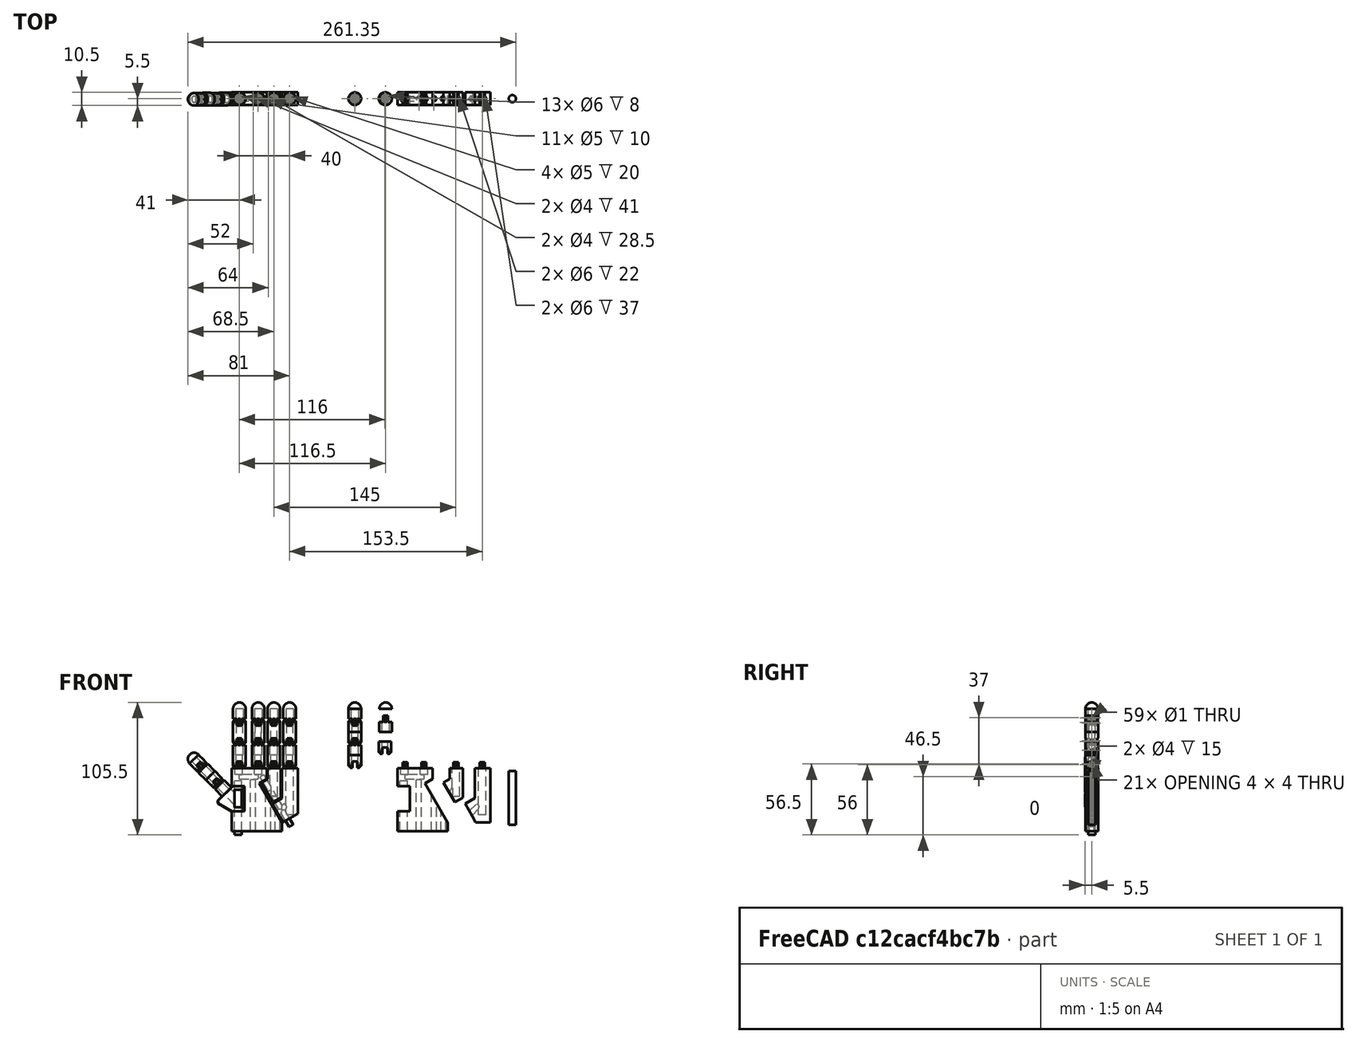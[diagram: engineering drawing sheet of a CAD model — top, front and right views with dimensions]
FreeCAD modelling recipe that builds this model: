
FCSTD DOCUMENT  (FreeCAD 0.19R)
Label: hand
License: All rights reserved
LicenseURL: http://en.wikipedia.org/wiki/All_rights_reserved
objects: Part::Cut×275, Part::Cylinder×259, Part::Box×139, Part::MultiFuse×82, TechDraw::DrawViewDimension×78, Part::Refine×60, Part::Sphere×50, Part::MultiCommon×43, TechDraw::DrawProjGroupItem×11, TechDraw::DrawProjGroup×11, Part::FeaturePython×5, App::DocumentObjectGroup×1, Part::Mirroring×1, TechDraw::DrawSVGTemplate×1, Part::Feature×1, TechDraw::DrawPage×1
note: 915 computed .brp shape members not serialized (recipe doc carries the construction recipe); baked Part::Feature solids carry a one-line shape summary decoded from their .brp

FEATURE [Part::Sphere] Sphere
  Angle1 = 0
  Angle2 = 90
  Angle3 = 360
  AttacherType = Attacher::AttachEngine3D
  Radius = 5
FEATURE [Part::Cylinder] Cylinder
  Angle = 360
  AttacherType = Attacher::AttachEngine3D
  Height = 10
  Placement = pos=(0,0,-10) rot=(0,0,1;0rad)
  Radius = 5
FEATURE [Part::Box] Box  label="Cube"
  AttacherType = Attacher::AttachEngine3D
  Height = 5
  Length = 4
  Placement = pos=(-2,-5,-10) rot=(0,0,1;0rad)
  Width = 10
FEATURE [Part::Cut] Cut
  Base = -> Cylinder
  Tool = -> Box
FEATURE [Part::Cylinder] Cylinder001
  Angle = 360
  AttacherType = Attacher::AttachEngine3D
  Height = 10
  Placement = pos=(0,0,-10) rot=(0,0,1;0rad)
  Radius = 2.5
FEATURE [Part::Cut] Cut001
  Base = -> Cut
  Tool = -> Cylinder001
FEATURE [Part::Cylinder] Cylinder002
  Angle = 360
  AttacherType = Attacher::AttachEngine3D
  Height = 10
  Placement = pos=(5,0,-7) rot=(0,1,0;4.71239rad)
  Radius = 0.5
FEATURE [Part::Cut] Cut002
  Base = -> Cut001
  Tool = -> Cylinder002
FEATURE [Part::Sphere] Sphere001
  Angle1 = -90
  Angle2 = 90
  Angle3 = 360
  AttacherType = Attacher::AttachEngine3D
  Placement = pos=(0,0,-5) rot=(0,0,1;0rad)
  Radius = 6
FEATURE [Part::MultiCommon] Common
  Shapes = -> [Cut002,Sphere001]
FEATURE [Part::Cylinder] Cylinder005
  Angle = 360
  AttacherType = Attacher::AttachEngine3D
  Height = 4
  Placement = pos=(18,0,-4) rot=(0,0,1;0rad)
  Radius = 5
FEATURE [Part::Cylinder] Cylinder006
  Angle = 360
  AttacherType = Attacher::AttachEngine3D
  Height = 10
  Placement = pos=(18,0,-6) rot=(0,0,1;0rad)
  Radius = 3
FEATURE [Part::Cut] Cut004
  Base = -> Cylinder005
  Placement = pos=(-18,0,0) rot=(0,0,1;0rad)
  Tool = -> Cylinder006
FEATURE [Part::MultiFuse] Fusion
  Shapes = -> [Common,Cut004]
FEATURE [Part::Refine] Fusion001
  Placement = pos=(0,0,-18.5) rot=(0,0,1;0rad)
  Source = -> Fusion
FEATURE [Part::Sphere] Sphere002
  Angle1 = -90
  Angle2 = 90
  Angle3 = 360
  AttacherType = Attacher::AttachEngine3D
  Placement = pos=(0,0,-5) rot=(0,0,1;0rad)
  Radius = 6
FEATURE [Part::Cylinder] Cylinder007
  Angle = 360
  AttacherType = Attacher::AttachEngine3D
  Height = 10
  Placement = pos=(0,0,-10) rot=(0,0,1;0rad)
  Radius = 2.5
FEATURE [Part::Box] Box001  label="Cube001"
  AttacherType = Attacher::AttachEngine3D
  Height = 5
  Length = 4
  Placement = pos=(-2,-5,-10) rot=(0,0,1;0rad)
  Width = 10
FEATURE [Part::Cylinder] Cylinder008
  Angle = 360
  AttacherType = Attacher::AttachEngine3D
  Height = 10
  Placement = pos=(0,0,-10) rot=(0,0,1;0rad)
  Radius = 5
FEATURE [Part::Cut] Cut005
  Base = -> Cylinder008
  Tool = -> Box001
FEATURE [Part::Cylinder] Cylinder009
  Angle = 360
  AttacherType = Attacher::AttachEngine3D
  Height = 10
  Placement = pos=(5,0,-7) rot=(0,-1,0;1.5708rad)
  Radius = 0.5
FEATURE [Part::Cylinder] Cylinder010
  Angle = 360
  AttacherType = Attacher::AttachEngine3D
  Height = 4
  Placement = pos=(18,0,-4) rot=(0,0,1;0rad)
  Radius = 5
FEATURE [Part::Cut] Cut008
  Base = -> Cut005
  Tool = -> Cylinder007
FEATURE [Part::Cut] Cut007
  Base = -> Cut008
  Tool = -> Cylinder009
FEATURE [Part::Cylinder] Cylinder011
  Angle = 360
  AttacherType = Attacher::AttachEngine3D
  Height = 10
  Placement = pos=(18,0,-6) rot=(0,0,1;0rad)
  Radius = 3
FEATURE [Part::Cut] Cut006
  Base = -> Cylinder010
  Placement = pos=(-18,0,0) rot=(0,0,1;0rad)
  Tool = -> Cylinder011
FEATURE [Part::MultiCommon] Common001
  Shapes = -> [Cut007,Sphere002]
FEATURE [Part::MultiFuse] Fusion003
  Shapes = -> [Common001,Cut006]
FEATURE [Part::Refine] Fusion002
  Placement = pos=(24,0,-26) rot=(0,0,1;0rad)
  Source = -> Fusion003
FEATURE [Part::Sphere] Sphere003
  Angle1 = 0
  Angle2 = 90
  Angle3 = 360
  AttacherType = Attacher::AttachEngine3D
  Placement = pos=(24.5,0,0) rot=(0,0,1;0rad)
  Radius = 5
FEATURE [Part::Cylinder] Cylinder012
  Angle = 360
  AttacherType = Attacher::AttachEngine3D
  Height = 10
  Placement = pos=(0,-50,-7) rot=(0,0,1;0rad)
  Radius = 5
FEATURE [Part::Sphere] Sphere004
  Angle1 = 0
  Angle2 = 90
  Angle3 = 360
  AttacherType = Attacher::AttachEngine3D
  Placement = pos=(0,-50,0) rot=(0,0,1;0rad)
  Radius = 5
FEATURE [Part::MultiCommon] Common002
  Shapes = -> [Cylinder012,Sphere004]
FEATURE [Part::Cylinder] Cylinder013
  Angle = 360
  AttacherType = Attacher::AttachEngine3D
  Height = 10
  Placement = pos=(0,-50,-10) rot=(0,0,1;0rad)
  Radius = 5
FEATURE [Part::MultiFuse] Fusion004
  Shapes = -> [Common002,Cylinder013]
FEATURE [Part::Box] Box002  label="Cube002"
  AttacherType = Attacher::AttachEngine3D
  Height = 10
  Length = 10
  Placement = pos=(2,-55,-2) rot=(0,0,1;0rad)
  Width = 10
FEATURE [Part::Box] Box003  label="Cube003"
  AttacherType = Attacher::AttachEngine3D
  Height = 10
  Length = 10
  Placement = pos=(-12,-55,-2) rot=(0,0,1;0rad)
  Width = 10
FEATURE [Part::Box] Box004  label="Cube004"
  AttacherType = Attacher::AttachEngine3D
  Height = 10
  Length = 2
  Placement = pos=(-1,-55,-2) rot=(0,0,1;0rad)
  Width = 10
FEATURE [Part::Cut] Cut009
  Base = -> Fusion004
  Tool = -> Box002
FEATURE [Part::Cut] Cut010
  Base = -> Cut009
  Tool = -> Box004
FEATURE [Part::Cut] Cut011
  Base = -> Cut010
  Tool = -> Box003
FEATURE [Part::Cylinder] Cylinder014
  Angle = 360
  AttacherType = Attacher::AttachEngine3D
  Height = 4
  Placement = pos=(-2,-50,1) rot=(0,1,0;1.5708rad)
  Radius = 2
FEATURE [Part::Cylinder] Cylinder015
  Angle = 360
  AttacherType = Attacher::AttachEngine3D
  Height = 10
  Placement = pos=(0,-50,-12) rot=(0,0,1;0rad)
  Radius = 3
FEATURE [Part::Cut] Cut012
  Base = -> Cut011
  Tool = -> Cylinder015
FEATURE [Part::MultiFuse] Fusion005
  Shapes = -> [Cut012,Cylinder014]
FEATURE [Part::Refine] Fusion005001
  Placement = pos=(0,50,-8.5) rot=(0,0,1;0rad)
  Source = -> Fusion005
FEATURE [Part::Cylinder] Cylinder016
  Angle = 360
  AttacherType = Attacher::AttachEngine3D
  Height = 10
  Placement = pos=(-5,0,-7) rot=(0,1,0;1.5708rad)
  Radius = 0.5
FEATURE [Part::Cut] Cut013
  Base = -> Fusion005001
  Placement = pos=(0,0,-18.5) rot=(0,0,1;0rad)
  Tool = -> Cylinder016
FEATURE [Part::Box] Box005  label="Cube005"
  AttacherType = Attacher::AttachEngine3D
  Height = 10
  Length = 2
  Placement = pos=(-1,-55,-2) rot=(0,0,1;0rad)
  Width = 10
FEATURE [Part::Cylinder] Cylinder018
  Angle = 360
  AttacherType = Attacher::AttachEngine3D
  Height = 4
  Placement = pos=(-2,-50,1) rot=(0,1,0;1.5708rad)
  Radius = 2
FEATURE [Part::Cylinder] Cylinder019
  Angle = 360
  AttacherType = Attacher::AttachEngine3D
  Height = 10
  Placement = pos=(0,-50,-7) rot=(0,0,1;0rad)
  Radius = 5
FEATURE [Part::Sphere] Sphere005
  Angle1 = 0
  Angle2 = 90
  Angle3 = 360
  AttacherType = Attacher::AttachEngine3D
  Placement = pos=(0,-50,0) rot=(0,0,1;0rad)
  Radius = 5
FEATURE [Part::MultiCommon] Common003
  Shapes = -> [Cylinder019,Sphere005]
FEATURE [Part::Cylinder] Cylinder020
  Angle = 360
  AttacherType = Attacher::AttachEngine3D
  Height = 10
  Placement = pos=(0,-50,-10) rot=(0,0,1;0rad)
  Radius = 5
FEATURE [Part::MultiFuse] Fusion005003
  Shapes = -> [Common003,Cylinder020]
FEATURE [Part::Box] Box006  label="Cube006"
  AttacherType = Attacher::AttachEngine3D
  Height = 10
  Length = 10
  Placement = pos=(2,-55,-2) rot=(0,0,1;0rad)
  Width = 10
FEATURE [Part::Box] Box007  label="Cube007"
  AttacherType = Attacher::AttachEngine3D
  Height = 10
  Length = 10
  Placement = pos=(-12,-55,-2) rot=(0,0,1;0rad)
  Width = 10
FEATURE [Part::Cut] Cut015
  Base = -> Fusion005003
  Tool = -> Box006
FEATURE [Part::Cylinder] Cylinder021
  Angle = 360
  AttacherType = Attacher::AttachEngine3D
  Height = 10
  Placement = pos=(-5,0,-7) rot=(0,1,0;1.5708rad)
  Radius = 0.5
FEATURE [Part::Cut] Cut017
  Base = -> Cut015
  Tool = -> Box005
FEATURE [Part::Cut] Cut018
  Base = -> Cut017
  Tool = -> Box007
FEATURE [Part::Cylinder] Cylinder022
  Angle = 360
  AttacherType = Attacher::AttachEngine3D
  Height = 10
  Placement = pos=(0,-50,-12) rot=(0,0,1;0rad)
  Radius = 3
FEATURE [Part::Cut] Cut014
  Base = -> Cut018
  Tool = -> Cylinder022
FEATURE [Part::MultiFuse] Fusion005002
  Shapes = -> [Cut014,Cylinder018]
FEATURE [Part::Refine] Fusion005004
  Placement = pos=(0,50,-8.5) rot=(0,0,1;0rad)
  Source = -> Fusion005002
FEATURE [Part::Cut] Cut016
  Base = -> Fusion005004
  Placement = pos=(24.5,0,0) rot=(0,0,1;0rad)
  Tool = -> Cylinder021
FEATURE [Part::Box] Box008  label="Cube008"
  AttacherType = Attacher::AttachEngine3D
  Height = 10
  Length = 2
  Placement = pos=(-1,-55,-2) rot=(0,0,1;0rad)
  Width = 10
FEATURE [Part::Cylinder] Cylinder023
  Angle = 360
  AttacherType = Attacher::AttachEngine3D
  Height = 4
  Placement = pos=(-2,-50,1) rot=(0,1,0;1.5708rad)
  Radius = 2
FEATURE [Part::Cylinder] Cylinder024
  Angle = 360
  AttacherType = Attacher::AttachEngine3D
  Height = 10
  Placement = pos=(0,-50,-7) rot=(0,0,1;0rad)
  Radius = 5
FEATURE [Part::Sphere] Sphere006
  Angle1 = 0
  Angle2 = 90
  Angle3 = 360
  AttacherType = Attacher::AttachEngine3D
  Placement = pos=(0,-50,0) rot=(0,0,1;0rad)
  Radius = 5
FEATURE [Part::MultiCommon] Common004
  Shapes = -> [Cylinder024,Sphere006]
FEATURE [Part::Cylinder] Cylinder025
  Angle = 360
  AttacherType = Attacher::AttachEngine3D
  Height = 10
  Placement = pos=(0,-50,-10) rot=(0,0,1;0rad)
  Radius = 5
FEATURE [Part::MultiFuse] Fusion005006
  Shapes = -> [Common004,Cylinder025]
FEATURE [Part::Box] Box009  label="Cube009"
  AttacherType = Attacher::AttachEngine3D
  Height = 10
  Length = 10
  Placement = pos=(2,-55,-2) rot=(0,0,1;0rad)
  Width = 10
FEATURE [Part::Box] Box010  label="Cube010"
  AttacherType = Attacher::AttachEngine3D
  Height = 10
  Length = 10
  Placement = pos=(-12,-55,-2) rot=(0,0,1;0rad)
  Width = 10
FEATURE [Part::Cut] Cut020
  Base = -> Fusion005006
  Tool = -> Box009
FEATURE [Part::Cylinder] Cylinder026
  Angle = 360
  AttacherType = Attacher::AttachEngine3D
  Height = 10
  Placement = pos=(-5,0,-7) rot=(0,1,0;1.5708rad)
  Radius = 0.5
FEATURE [Part::Cut] Cut022
  Base = -> Cut020
  Tool = -> Box008
FEATURE [Part::Cut] Cut023
  Base = -> Cut022
  Tool = -> Box010
FEATURE [Part::Cylinder] Cylinder027
  Angle = 360
  AttacherType = Attacher::AttachEngine3D
  Height = 10
  Placement = pos=(0,-50,-12) rot=(0,0,1;0rad)
  Radius = 3
FEATURE [Part::Cut] Cut019
  Base = -> Cut023
  Tool = -> Cylinder027
FEATURE [Part::MultiFuse] Fusion005005
  Shapes = -> [Cut019,Cylinder023]
FEATURE [Part::Refine] Fusion005007
  Placement = pos=(0,50,-8.5) rot=(0,0,1;0rad)
  Source = -> Fusion005005
FEATURE [Part::Cut] Cut021
  Base = -> Fusion005007
  Placement = pos=(0,-2.3e-15,-18.5) rot=(1,0,0;3.14159rad)
  Tool = -> Cylinder026
FEATURE [Part::Cylinder] Cylinder028
  Angle = 360
  AttacherType = Attacher::AttachEngine3D
  Height = 10
  Placement = pos=(0,0,-10) rot=(0,0,1;0rad)
  Radius = 5
FEATURE [Part::Box] Box011  label="Cube011"
  AttacherType = Attacher::AttachEngine3D
  Height = 5
  Length = 4
  Placement = pos=(-2,-5,-10) rot=(0,0,1;0rad)
  Width = 10
FEATURE [Part::Cut] Cut024
  Base = -> Cylinder028
  Tool = -> Box011
FEATURE [Part::Cylinder] Cylinder029
  Angle = 360
  AttacherType = Attacher::AttachEngine3D
  Height = 10
  Placement = pos=(0,0,-10) rot=(0,0,1;0rad)
  Radius = 2.5
FEATURE [Part::Cut] Cut025
  Base = -> Cut024
  Tool = -> Cylinder029
FEATURE [Part::Cylinder] Cylinder030
  Angle = 360
  AttacherType = Attacher::AttachEngine3D
  Height = 10
  Placement = pos=(5,0,-7) rot=(0,-1,0;1.5708rad)
  Radius = 0.5
FEATURE [Part::Cut] Cut026
  Base = -> Cut025
  Tool = -> Cylinder030
FEATURE [Part::Sphere] Sphere007
  Angle1 = -90
  Angle2 = 90
  Angle3 = 360
  AttacherType = Attacher::AttachEngine3D
  Placement = pos=(0,0,-5) rot=(0,0,1;0rad)
  Radius = 6
FEATURE [Part::MultiCommon] Common005
  Shapes = -> [Cut026,Sphere007]
FEATURE [Part::Cylinder] Cylinder031
  Angle = 360
  AttacherType = Attacher::AttachEngine3D
  Height = 4
  Placement = pos=(18,0,-4) rot=(0,0,1;0rad)
  Radius = 5
FEATURE [Part::Cylinder] Cylinder032
  Angle = 360
  AttacherType = Attacher::AttachEngine3D
  Height = 10
  Placement = pos=(18,0,-6) rot=(0,0,1;0rad)
  Radius = 3
FEATURE [Part::Cut] Cut027
  Base = -> Cylinder031
  Placement = pos=(-18,0,0) rot=(0,0,1;0rad)
  Tool = -> Cylinder032
FEATURE [Part::MultiFuse] Fusion005008
  Shapes = -> [Common005,Cut027]
FEATURE [Part::Refine] Fusion005009
  Placement = pos=(0,2e-15,-18.5) rot=(1,0,0;3.14159rad)
  Source = -> Fusion005008
FEATURE [Part::Cylinder] Cylinder033
  Angle = 360
  AttacherType = Attacher::AttachEngine3D
  Height = 10
  Placement = pos=(0,0,-10) rot=(0,0,1;0rad)
  Radius = 5
FEATURE [Part::Box] Box012  label="Cube012"
  AttacherType = Attacher::AttachEngine3D
  Height = 5
  Length = 4
  Placement = pos=(-2,-5,-10) rot=(0,0,1;0rad)
  Width = 10
FEATURE [Part::Cut] Cut028
  Base = -> Cylinder033
  Tool = -> Box012
FEATURE [Part::Cylinder] Cylinder034
  Angle = 360
  AttacherType = Attacher::AttachEngine3D
  Height = 10
  Placement = pos=(0,0,-10) rot=(0,0,1;0rad)
  Radius = 2.5
FEATURE [Part::Cut] Cut029
  Base = -> Cut028
  Tool = -> Cylinder034
FEATURE [Part::Cylinder] Cylinder035
  Angle = 360
  AttacherType = Attacher::AttachEngine3D
  Height = 10
  Placement = pos=(5,0,-7) rot=(0,-1,0;1.5708rad)
  Radius = 0.5
FEATURE [Part::Cut] Cut030
  Base = -> Cut029
  Tool = -> Cylinder035
FEATURE [Part::Sphere] Sphere008
  Angle1 = -90
  Angle2 = 90
  Angle3 = 360
  AttacherType = Attacher::AttachEngine3D
  Placement = pos=(0,0,-5) rot=(0,0,1;0rad)
  Radius = 6
FEATURE [Part::MultiCommon] Common006
  Shapes = -> [Cut030,Sphere008]
FEATURE [Part::Cylinder] Cylinder036
  Angle = 360
  AttacherType = Attacher::AttachEngine3D
  Height = 4
  Placement = pos=(18,0,-4) rot=(0,0,1;0rad)
  Radius = 5
FEATURE [Part::Cylinder] Cylinder037
  Angle = 360
  AttacherType = Attacher::AttachEngine3D
  Height = 10
  Placement = pos=(18,0,-6) rot=(0,0,1;0rad)
  Radius = 3
FEATURE [Part::Cut] Cut031
  Base = -> Cylinder036
  Placement = pos=(-18,0,0) rot=(0,0,1;0rad)
  Tool = -> Cylinder037
FEATURE [Part::MultiFuse] Fusion005010
  Shapes = -> [Common006,Cut031]
FEATURE [Part::Refine] Fusion005011
  Placement = pos=(0,0,-37) rot=(0,0,1;0rad)
  Source = -> Fusion005010
FEATURE [App::DocumentObjectGroup] Group  label="dedo"
  Group = -> [Sphere,Cut021,Fusion001,Fusion005009,Cut013,Fusion005011]
FEATURE [Part::Box] Box013  label="Cube013"
  AttacherType = Attacher::AttachEngine3D
  Height = 10
  Length = 2
  Placement = pos=(-1,-55,-2) rot=(0,0,1;0rad)
  Width = 10
FEATURE [Part::Cylinder] Cylinder038
  Angle = 360
  AttacherType = Attacher::AttachEngine3D
  Height = 4
  Placement = pos=(-2,-50,1) rot=(0,1,0;1.5708rad)
  Radius = 2
FEATURE [Part::Sphere] Sphere009
  Angle1 = 0
  Angle2 = 90
  Angle3 = 360
  AttacherType = Attacher::AttachEngine3D
  Radius = 5
FEATURE [Part::Cylinder] Cylinder039
  Angle = 360
  AttacherType = Attacher::AttachEngine3D
  Height = 10
  Placement = pos=(0,0,-10) rot=(0,0,1;0rad)
  Radius = 5
FEATURE [Part::Box] Box014  label="Cube014"
  AttacherType = Attacher::AttachEngine3D
  Height = 5
  Length = 4
  Placement = pos=(-2,-5,-10) rot=(0,0,1;0rad)
  Width = 10
FEATURE [Part::Cut] Cut032
  Base = -> Cylinder039
  Tool = -> Box014
FEATURE [Part::Cylinder] Cylinder040
  Angle = 360
  AttacherType = Attacher::AttachEngine3D
  Height = 10
  Placement = pos=(0,0,-10) rot=(0,0,1;0rad)
  Radius = 2.5
FEATURE [Part::Cut] Cut033
  Base = -> Cut032
  Tool = -> Cylinder040
FEATURE [Part::Cylinder] Cylinder041
  Angle = 360
  AttacherType = Attacher::AttachEngine3D
  Height = 10
  Placement = pos=(5,0,-7) rot=(0,-1,0;1.5708rad)
  Radius = 0.5
FEATURE [Part::Cut] Cut034
  Base = -> Cut033
  Tool = -> Cylinder041
FEATURE [Part::Sphere] Sphere010
  Angle1 = -90
  Angle2 = 90
  Angle3 = 360
  AttacherType = Attacher::AttachEngine3D
  Placement = pos=(0,0,-5) rot=(0,0,1;0rad)
  Radius = 6
FEATURE [Part::MultiCommon] Common007
  Shapes = -> [Cut034,Sphere010]
FEATURE [Part::Cylinder] Cylinder042
  Angle = 360
  AttacherType = Attacher::AttachEngine3D
  Height = 4
  Placement = pos=(18,0,-4) rot=(0,0,1;0rad)
  Radius = 5
FEATURE [Part::Cylinder] Cylinder043
  Angle = 360
  AttacherType = Attacher::AttachEngine3D
  Height = 10
  Placement = pos=(18,0,-6) rot=(0,0,1;0rad)
  Radius = 3
FEATURE [Part::Cut] Cut035
  Base = -> Cylinder042
  Placement = pos=(-18,0,0) rot=(0,0,1;0rad)
  Tool = -> Cylinder043
FEATURE [Part::MultiFuse] Fusion005013
  Shapes = -> [Common007,Cut035]
FEATURE [Part::Refine] Fusion005014
  Placement = pos=(0,0,-18.5) rot=(0,0,1;0rad)
  Source = -> Fusion005013
FEATURE [Part::Cylinder] Cylinder044
  Angle = 360
  AttacherType = Attacher::AttachEngine3D
  Height = 10
  Placement = pos=(0,-50,-7) rot=(0,0,1;0rad)
  Radius = 5
FEATURE [Part::Sphere] Sphere011
  Angle1 = 0
  Angle2 = 90
  Angle3 = 360
  AttacherType = Attacher::AttachEngine3D
  Placement = pos=(0,-50,0) rot=(0,0,1;0rad)
  Radius = 5
FEATURE [Part::MultiCommon] Common008
  Shapes = -> [Cylinder044,Sphere011]
FEATURE [Part::Cylinder] Cylinder045
  Angle = 360
  AttacherType = Attacher::AttachEngine3D
  Height = 10
  Placement = pos=(0,-50,-10) rot=(0,0,1;0rad)
  Radius = 5
FEATURE [Part::MultiFuse] Fusion005015
  Shapes = -> [Common008,Cylinder045]
FEATURE [Part::Box] Box015  label="Cube015"
  AttacherType = Attacher::AttachEngine3D
  Height = 10
  Length = 10
  Placement = pos=(2,-55,-2) rot=(0,0,1;0rad)
  Width = 10
FEATURE [Part::Box] Box016  label="Cube016"
  AttacherType = Attacher::AttachEngine3D
  Height = 10
  Length = 10
  Placement = pos=(-12,-55,-2) rot=(0,0,1;0rad)
  Width = 10
FEATURE [Part::Cut] Cut037
  Base = -> Fusion005015
  Tool = -> Box015
FEATURE [Part::Cylinder] Cylinder046
  Angle = 360
  AttacherType = Attacher::AttachEngine3D
  Height = 10
  Placement = pos=(-5,0,-7) rot=(0,1,0;1.5708rad)
  Radius = 0.5
FEATURE [Part::Cut] Cut039
  Base = -> Cut037
  Tool = -> Box013
FEATURE [Part::Cut] Cut040
  Base = -> Cut039
  Tool = -> Box016
FEATURE [Part::Cylinder] Cylinder047
  Angle = 360
  AttacherType = Attacher::AttachEngine3D
  Height = 10
  Placement = pos=(0,-50,-12) rot=(0,0,1;0rad)
  Radius = 3
FEATURE [Part::Cut] Cut036
  Base = -> Cut040
  Tool = -> Cylinder047
FEATURE [Part::MultiFuse] Fusion005012
  Shapes = -> [Cut036,Cylinder038]
FEATURE [Part::Refine] Fusion005016
  Placement = pos=(0,50,-8.5) rot=(0,0,1;0rad)
  Source = -> Fusion005012
FEATURE [Part::Cut] Cut038
  Base = -> Fusion005016
  Placement = pos=(0,0,-18.5) rot=(0,0,1;0rad)
  Tool = -> Cylinder046
FEATURE [Part::Cylinder] Cylinder048
  Angle = 360
  AttacherType = Attacher::AttachEngine3D
  Height = 10
  Placement = pos=(0,0,-10) rot=(0,0,1;0rad)
  Radius = 2.5
FEATURE [Part::Sphere] Sphere012
  Angle1 = 0
  Angle2 = 90
  Angle3 = 360
  AttacherType = Attacher::AttachEngine3D
  Placement = pos=(0,-50,0) rot=(0,0,1;0rad)
  Radius = 5
FEATURE [Part::Cylinder] Cylinder049
  Angle = 360
  AttacherType = Attacher::AttachEngine3D
  Height = 10
  Placement = pos=(0,0,-10) rot=(0,0,1;0rad)
  Radius = 5
FEATURE [Part::Sphere] Sphere013
  Angle1 = -90
  Angle2 = 90
  Angle3 = 360
  AttacherType = Attacher::AttachEngine3D
  Placement = pos=(0,0,-5) rot=(0,0,1;0rad)
  Radius = 6
FEATURE [Part::Cylinder] Cylinder050
  Angle = 360
  AttacherType = Attacher::AttachEngine3D
  Height = 4
  Placement = pos=(18,0,-4) rot=(0,0,1;0rad)
  Radius = 5
FEATURE [Part::Cylinder] Cylinder051
  Angle = 360
  AttacherType = Attacher::AttachEngine3D
  Height = 10
  Placement = pos=(0,-50,-7) rot=(0,0,1;0rad)
  Radius = 5
FEATURE [Part::Cylinder] Cylinder052
  Angle = 360
  AttacherType = Attacher::AttachEngine3D
  Height = 4
  Placement = pos=(-2,-50,1) rot=(0,1,0;1.5708rad)
  Radius = 2
FEATURE [Part::Box] Box017  label="Cube017"
  AttacherType = Attacher::AttachEngine3D
  Height = 10
  Length = 10
  Placement = pos=(2,-55,-2) rot=(0,0,1;0rad)
  Width = 10
FEATURE [Part::Box] Box018  label="Cube018"
  AttacherType = Attacher::AttachEngine3D
  Height = 10
  Length = 10
  Placement = pos=(-12,-55,-2) rot=(0,0,1;0rad)
  Width = 10
FEATURE [Part::Box] Box019  label="Cube019"
  AttacherType = Attacher::AttachEngine3D
  Height = 10
  Length = 2
  Placement = pos=(-1,-55,-2) rot=(0,0,1;0rad)
  Width = 10
FEATURE [Part::MultiCommon] Common010
  Shapes = -> [Cylinder051,Sphere012]
FEATURE [Part::Cylinder] Cylinder053
  Angle = 360
  AttacherType = Attacher::AttachEngine3D
  Height = 10
  Placement = pos=(0,-50,-10) rot=(0,0,1;0rad)
  Radius = 5
FEATURE [Part::MultiFuse] Fusion005018
  Shapes = -> [Common010,Cylinder053]
FEATURE [Part::Cut] Cut044
  Base = -> Fusion005018
  Tool = -> Box017
FEATURE [Part::Cylinder] Cylinder054
  Angle = 360
  AttacherType = Attacher::AttachEngine3D
  Height = 10
  Placement = pos=(-5,0,-7) rot=(0,1,0;1.5708rad)
  Radius = 0.5
FEATURE [Part::Cut] Cut046
  Base = -> Cut044
  Tool = -> Box019
FEATURE [Part::Cut] Cut047
  Base = -> Cut046
  Tool = -> Box018
FEATURE [Part::Cylinder] Cylinder055
  Angle = 360
  AttacherType = Attacher::AttachEngine3D
  Height = 10
  Placement = pos=(0,-50,-12) rot=(0,0,1;0rad)
  Radius = 3
FEATURE [Part::Cut] Cut043
  Base = -> Cut047
  Tool = -> Cylinder055
FEATURE [Part::MultiFuse] Fusion005017
  Shapes = -> [Cut043,Cylinder052]
FEATURE [Part::Refine] Fusion005019
  Placement = pos=(0,50,-8.5) rot=(0,0,1;0rad)
  Source = -> Fusion005017
FEATURE [Part::Cut] Cut045
  Base = -> Fusion005019
  Placement = pos=(0,-2e-15,-18.5) rot=(1,0,0;3.14159rad)
  Tool = -> Cylinder054
FEATURE [Part::Cylinder] Cylinder056
  Angle = 360
  AttacherType = Attacher::AttachEngine3D
  Height = 10
  Placement = pos=(5,0,-7) rot=(0,-1,0;1.5708rad)
  Radius = 0.5
FEATURE [Part::Cylinder] Cylinder057
  Angle = 360
  AttacherType = Attacher::AttachEngine3D
  Height = 10
  Placement = pos=(5,0,-7) rot=(0,-1,0;1.5708rad)
  Radius = 0.5
FEATURE [Part::Box] Box020  label="Cube020"
  AttacherType = Attacher::AttachEngine3D
  Height = 5
  Length = 4
  Placement = pos=(-2,-5,-10) rot=(0,0,1;0rad)
  Width = 10
FEATURE [Part::Cylinder] Cylinder058
  Angle = 360
  AttacherType = Attacher::AttachEngine3D
  Height = 10
  Placement = pos=(0,0,-10) rot=(0,0,1;0rad)
  Radius = 5
FEATURE [Part::Cut] Cut048
  Base = -> Cylinder058
  Tool = -> Box020
FEATURE [Part::Cut] Cut051
  Base = -> Cut048
  Tool = -> Cylinder048
FEATURE [Part::Cut] Cut042
  Base = -> Cut051
  Tool = -> Cylinder057
FEATURE [Part::MultiCommon] Common009
  Shapes = -> [Cut042,Sphere013]
FEATURE [Part::Cylinder] Cylinder059
  Angle = 360
  AttacherType = Attacher::AttachEngine3D
  Height = 10
  Placement = pos=(18,0,-6) rot=(0,0,1;0rad)
  Radius = 3
FEATURE [Part::Cut] Cut052
  Base = -> Cylinder050
  Placement = pos=(-18,0,0) rot=(0,0,1;0rad)
  Tool = -> Cylinder059
FEATURE [Part::MultiFuse] Fusion005020
  Shapes = -> [Common009,Cut052]
FEATURE [Part::Refine] Fusion005021
  Placement = pos=(0,2e-15,-18.5) rot=(1,0,0;3.14159rad)
  Source = -> Fusion005020
FEATURE [Part::Box] Box021  label="Cube021"
  AttacherType = Attacher::AttachEngine3D
  Height = 5
  Length = 4
  Placement = pos=(-2,-5,-10) rot=(0,0,1;0rad)
  Width = 10
FEATURE [Part::Cut] Cut041
  Base = -> Cylinder049
  Tool = -> Box021
FEATURE [Part::Sphere] Sphere014
  Angle1 = -90
  Angle2 = 90
  Angle3 = 360
  AttacherType = Attacher::AttachEngine3D
  Placement = pos=(0,0,-5) rot=(0,0,1;0rad)
  Radius = 6
FEATURE [Part::Cylinder] Cylinder060
  Angle = 360
  AttacherType = Attacher::AttachEngine3D
  Height = 4
  Placement = pos=(18,0,-4) rot=(0,0,1;0rad)
  Radius = 5
FEATURE [Part::Cylinder] Cylinder061
  Angle = 360
  AttacherType = Attacher::AttachEngine3D
  Height = 10
  Placement = pos=(18,0,-6) rot=(0,0,1;0rad)
  Radius = 3
FEATURE [Part::Cut] Cut053
  Base = -> Cylinder060
  Placement = pos=(-18,0,0) rot=(0,0,1;0rad)
  Tool = -> Cylinder061
FEATURE [Part::Cylinder] Cylinder062
  Angle = 360
  AttacherType = Attacher::AttachEngine3D
  Height = 10
  Placement = pos=(0,0,-10) rot=(0,0,1;0rad)
  Radius = 2.5
FEATURE [Part::Cut] Cut049
  Base = -> Cut041
  Tool = -> Cylinder062
FEATURE [Part::Cut] Cut050
  Base = -> Cut049
  Tool = -> Cylinder056
FEATURE [Part::MultiCommon] Common011
  Shapes = -> [Cut050,Sphere014]
FEATURE [Part::MultiFuse] Fusion005022
  Shapes = -> [Common011,Cut053]
FEATURE [Part::Refine] Fusion005023
  Placement = pos=(0,0,-37) rot=(0,0,1;0rad)
  Source = -> Fusion005022
FEATURE [Part::FeaturePython] Connect  # WARN: FeaturePython — macro-defined, semantics opaque (R4)
  Objects = -> [Sphere009,Fusion005014,Cut038,Cut045,Fusion005021,Fusion005023]
  Placement = pos=(-77,0,0) rot=(0,0,1;0rad)
  Tolerance = 0
FEATURE [Part::Sphere] Sphere015
  Angle1 = -90
  Angle2 = 90
  Angle3 = 360
  AttacherType = Attacher::AttachEngine3D
  Placement = pos=(0,0,-5) rot=(0,0,1;0rad)
  Radius = 6
FEATURE [Part::Cylinder] Cylinder063
  Angle = 360
  AttacherType = Attacher::AttachEngine3D
  Height = 10
  Placement = pos=(-5,0,-7) rot=(0,1,0;1.5708rad)
  Radius = 0.5
FEATURE [Part::Cylinder] Cylinder064
  Angle = 360
  AttacherType = Attacher::AttachEngine3D
  Height = 10
  Placement = pos=(0,0,-10) rot=(0,0,1;0rad)
  Radius = 2.5
FEATURE [Part::Cylinder] Cylinder065
  Angle = 360
  AttacherType = Attacher::AttachEngine3D
  Height = 4
  Placement = pos=(-2,-50,1) rot=(0,1,0;1.5708rad)
  Radius = 2
FEATURE [Part::Cylinder] Cylinder066
  Angle = 360
  AttacherType = Attacher::AttachEngine3D
  Height = 10
  Placement = pos=(5,0,-7) rot=(0,-1,0;1.5708rad)
  Radius = 0.5
FEATURE [Part::Cylinder] Cylinder067
  Angle = 360
  AttacherType = Attacher::AttachEngine3D
  Height = 10
  Placement = pos=(18,0,-6) rot=(0,0,1;0rad)
  Radius = 3
FEATURE [Part::Sphere] Sphere016
  Angle1 = -90
  Angle2 = 90
  Angle3 = 360
  AttacherType = Attacher::AttachEngine3D
  Placement = pos=(0,0,-5) rot=(0,0,1;0rad)
  Radius = 6
FEATURE [Part::Cylinder] Cylinder068
  Angle = 360
  AttacherType = Attacher::AttachEngine3D
  Height = 4
  Placement = pos=(-2,-50,1) rot=(0,1,0;1.5708rad)
  Radius = 2
FEATURE [Part::Box] Box022  label="Cube022"
  AttacherType = Attacher::AttachEngine3D
  Height = 10
  Length = 10
  Placement = pos=(2,-55,-2) rot=(0,0,1;0rad)
  Width = 10
FEATURE [Part::Sphere] Sphere017
  Angle1 = 0
  Angle2 = 90
  Angle3 = 360
  AttacherType = Attacher::AttachEngine3D
  Placement = pos=(0,-50,0) rot=(0,0,1;0rad)
  Radius = 5
FEATURE [Part::Sphere] Sphere018
  Angle1 = 0
  Angle2 = 90
  Angle3 = 360
  AttacherType = Attacher::AttachEngine3D
  Radius = 5
FEATURE [Part::Sphere] Sphere019
  Angle1 = 0
  Angle2 = 90
  Angle3 = 360
  AttacherType = Attacher::AttachEngine3D
  Placement = pos=(0,-50,0) rot=(0,0,1;0rad)
  Radius = 5
FEATURE [Part::Box] Box023  label="Cube023"
  AttacherType = Attacher::AttachEngine3D
  Height = 10
  Length = 2
  Placement = pos=(-1,-55,-2) rot=(0,0,1;0rad)
  Width = 10
FEATURE [Part::Cylinder] Cylinder069
  Angle = 360
  AttacherType = Attacher::AttachEngine3D
  Height = 10
  Placement = pos=(0,-50,-12) rot=(0,0,1;0rad)
  Radius = 3
FEATURE [Part::Cylinder] Cylinder070
  Angle = 360
  AttacherType = Attacher::AttachEngine3D
  Height = 4
  Placement = pos=(18,0,-4) rot=(0,0,1;0rad)
  Radius = 5
FEATURE [Part::Box] Box024  label="Cube024"
  AttacherType = Attacher::AttachEngine3D
  Height = 10
  Length = 10
  Placement = pos=(2,-55,-2) rot=(0,0,1;0rad)
  Width = 10
FEATURE [Part::Cylinder] Cylinder071
  Angle = 360
  AttacherType = Attacher::AttachEngine3D
  Height = 4
  Placement = pos=(18,0,-4) rot=(0,0,1;0rad)
  Radius = 5
FEATURE [Part::Box] Box025  label="Cube025"
  AttacherType = Attacher::AttachEngine3D
  Height = 5
  Length = 4
  Placement = pos=(-2,-5,-10) rot=(0,0,1;0rad)
  Width = 10
FEATURE [Part::Cylinder] Cylinder072
  Angle = 360
  AttacherType = Attacher::AttachEngine3D
  Height = 10
  Placement = pos=(0,-50,-7) rot=(0,0,1;0rad)
  Radius = 5
FEATURE [Part::Cylinder] Cylinder073
  Angle = 360
  AttacherType = Attacher::AttachEngine3D
  Height = 10
  Placement = pos=(0,0,-10) rot=(0,0,1;0rad)
  Radius = 5
FEATURE [Part::Cylinder] Cylinder074
  Angle = 360
  AttacherType = Attacher::AttachEngine3D
  Height = 10
  Placement = pos=(0,0,-10) rot=(0,0,1;0rad)
  Radius = 5
FEATURE [Part::Cut] Cut063
  Base = -> Cylinder074
  Tool = -> Box025
FEATURE [Part::Cut] Cut064
  Base = -> Cylinder071
  Placement = pos=(-18,0,0) rot=(0,0,1;0rad)
  Tool = -> Cylinder067
FEATURE [Part::MultiCommon] Common014
  Shapes = -> [Cylinder072,Sphere017]
FEATURE [Part::Box] Box026  label="Cube026"
  AttacherType = Attacher::AttachEngine3D
  Height = 10
  Length = 10
  Placement = pos=(-12,-55,-2) rot=(0,0,1;0rad)
  Width = 10
FEATURE [Part::Cylinder] Cylinder075
  Angle = 360
  AttacherType = Attacher::AttachEngine3D
  Height = 10
  Placement = pos=(0,0,-10) rot=(0,0,1;0rad)
  Radius = 2.5
FEATURE [Part::Cut] Cut062
  Base = -> Cut063
  Tool = -> Cylinder075
FEATURE [Part::Cut] Cut056
  Base = -> Cut062
  Tool = -> Cylinder066
FEATURE [Part::MultiCommon] Common012
  Shapes = -> [Cut056,Sphere016]
FEATURE [Part::MultiFuse] Fusion005030
  Shapes = -> [Common012,Cut064]
FEATURE [Part::Refine] Fusion005028
  Placement = pos=(0,0,-18.5) rot=(0,0,1;0rad)
  Source = -> Fusion005030
FEATURE [Part::Cylinder] Cylinder076
  Angle = 360
  AttacherType = Attacher::AttachEngine3D
  Height = 10
  Placement = pos=(0,-50,-10) rot=(0,0,1;0rad)
  Radius = 5
FEATURE [Part::MultiFuse] Fusion005024
  Shapes = -> [Common014,Cylinder076]
FEATURE [Part::Cut] Cut061
  Base = -> Fusion005024
  Tool = -> Box024
FEATURE [Part::Cut] Cut059
  Base = -> Cut061
  Tool = -> Box023
FEATURE [Part::Cut] Cut058
  Base = -> Cut059
  Tool = -> Box026
FEATURE [Part::Cut] Cut055
  Base = -> Cut058
  Tool = -> Cylinder069
FEATURE [Part::MultiFuse] Fusion005027
  Shapes = -> [Cut055,Cylinder065]
FEATURE [Part::Refine] Fusion005029
  Placement = pos=(0,50,-8.5) rot=(0,0,1;0rad)
  Source = -> Fusion005027
FEATURE [Part::Cut] Cut060
  Base = -> Fusion005029
  Placement = pos=(0,0,-18.5) rot=(0,0,1;0rad)
  Tool = -> Cylinder063
FEATURE [Part::Cylinder] Cylinder077
  Angle = 360
  AttacherType = Attacher::AttachEngine3D
  Height = 10
  Placement = pos=(0,-50,-7) rot=(0,0,1;0rad)
  Radius = 5
FEATURE [Part::Box] Box027  label="Cube027"
  AttacherType = Attacher::AttachEngine3D
  Height = 10
  Length = 10
  Placement = pos=(-12,-55,-2) rot=(0,0,1;0rad)
  Width = 10
FEATURE [Part::Box] Box028  label="Cube028"
  AttacherType = Attacher::AttachEngine3D
  Height = 10
  Length = 2
  Placement = pos=(-1,-55,-2) rot=(0,0,1;0rad)
  Width = 10
FEATURE [Part::MultiCommon] Common015
  Shapes = -> [Cylinder077,Sphere019]
FEATURE [Part::Cylinder] Cylinder078
  Angle = 360
  AttacherType = Attacher::AttachEngine3D
  Height = 10
  Placement = pos=(0,-50,-10) rot=(0,0,1;0rad)
  Radius = 5
FEATURE [Part::MultiFuse] Fusion005026
  Shapes = -> [Common015,Cylinder078]
FEATURE [Part::Cut] Cut066
  Base = -> Fusion005026
  Tool = -> Box022
FEATURE [Part::Cylinder] Cylinder079
  Angle = 360
  AttacherType = Attacher::AttachEngine3D
  Height = 10
  Placement = pos=(-5,0,-7) rot=(0,1,0;1.5708rad)
  Radius = 0.5
FEATURE [Part::Cut] Cut068
  Base = -> Cut066
  Tool = -> Box028
FEATURE [Part::Cut] Cut069
  Base = -> Cut068
  Tool = -> Box027
FEATURE [Part::Cylinder] Cylinder080
  Angle = 360
  AttacherType = Attacher::AttachEngine3D
  Height = 10
  Placement = pos=(0,-50,-12) rot=(0,0,1;0rad)
  Radius = 3
FEATURE [Part::Cut] Cut065
  Base = -> Cut069
  Tool = -> Cylinder080
FEATURE [Part::MultiFuse] Fusion005025
  Shapes = -> [Cut065,Cylinder068]
FEATURE [Part::Refine] Fusion005031
  Placement = pos=(0,50,-8.5) rot=(0,0,1;0rad)
  Source = -> Fusion005025
FEATURE [Part::Cut] Cut067
  Base = -> Fusion005031
  Placement = pos=(0,-2e-15,-18.5) rot=(1,0,0;3.14159rad)
  Tool = -> Cylinder079
FEATURE [Part::Cylinder] Cylinder081
  Angle = 360
  AttacherType = Attacher::AttachEngine3D
  Height = 10
  Placement = pos=(5,0,-7) rot=(0,-1,0;1.5708rad)
  Radius = 0.5
FEATURE [Part::Cylinder] Cylinder082
  Angle = 360
  AttacherType = Attacher::AttachEngine3D
  Height = 10
  Placement = pos=(5,0,-7) rot=(0,-1,0;1.5708rad)
  Radius = 0.5
FEATURE [Part::Box] Box029  label="Cube029"
  AttacherType = Attacher::AttachEngine3D
  Height = 5
  Length = 4
  Placement = pos=(-2,-5,-10) rot=(0,0,1;0rad)
  Width = 10
FEATURE [Part::Cylinder] Cylinder083
  Angle = 360
  AttacherType = Attacher::AttachEngine3D
  Height = 10
  Placement = pos=(0,0,-10) rot=(0,0,1;0rad)
  Radius = 5
FEATURE [Part::Cut] Cut070
  Base = -> Cylinder083
  Tool = -> Box029
FEATURE [Part::Cut] Cut073
  Base = -> Cut070
  Tool = -> Cylinder064
FEATURE [Part::Cut] Cut054
  Base = -> Cut073
  Tool = -> Cylinder082
FEATURE [Part::MultiCommon] Common013
  Shapes = -> [Cut054,Sphere015]
FEATURE [Part::Cylinder] Cylinder084
  Angle = 360
  AttacherType = Attacher::AttachEngine3D
  Height = 10
  Placement = pos=(18,0,-6) rot=(0,0,1;0rad)
  Radius = 3
FEATURE [Part::Cut] Cut074
  Base = -> Cylinder070
  Placement = pos=(-18,0,0) rot=(0,0,1;0rad)
  Tool = -> Cylinder084
FEATURE [Part::MultiFuse] Fusion005032
  Shapes = -> [Common013,Cut074]
FEATURE [Part::Refine] Fusion005033
  Placement = pos=(0,2e-15,-18.5) rot=(1,0,0;3.14159rad)
  Source = -> Fusion005032
FEATURE [Part::Box] Box030  label="Cube030"
  AttacherType = Attacher::AttachEngine3D
  Height = 5
  Length = 4
  Placement = pos=(-2,-5,-10) rot=(0,0,1;0rad)
  Width = 10
FEATURE [Part::Cut] Cut057
  Base = -> Cylinder073
  Tool = -> Box030
FEATURE [Part::Sphere] Sphere020
  Angle1 = -90
  Angle2 = 90
  Angle3 = 360
  AttacherType = Attacher::AttachEngine3D
  Placement = pos=(0,0,-5) rot=(0,0,1;0rad)
  Radius = 6
FEATURE [Part::Cylinder] Cylinder085
  Angle = 360
  AttacherType = Attacher::AttachEngine3D
  Height = 4
  Placement = pos=(18,0,-4) rot=(0,0,1;0rad)
  Radius = 5
FEATURE [Part::Cylinder] Cylinder086
  Angle = 360
  AttacherType = Attacher::AttachEngine3D
  Height = 10
  Placement = pos=(18,0,-6) rot=(0,0,1;0rad)
  Radius = 3
FEATURE [Part::Cut] Cut075
  Base = -> Cylinder085
  Placement = pos=(-18,0,0) rot=(0,0,1;0rad)
  Tool = -> Cylinder086
FEATURE [Part::Cylinder] Cylinder087
  Angle = 360
  AttacherType = Attacher::AttachEngine3D
  Height = 10
  Placement = pos=(0,0,-10) rot=(0,0,1;0rad)
  Radius = 2.5
FEATURE [Part::Cut] Cut071
  Base = -> Cut057
  Tool = -> Cylinder087
FEATURE [Part::Cut] Cut072
  Base = -> Cut071
  Tool = -> Cylinder081
FEATURE [Part::MultiCommon] Common016
  Shapes = -> [Cut072,Sphere020]
FEATURE [Part::MultiFuse] Fusion005034
  Shapes = -> [Common016,Cut075]
FEATURE [Part::Refine] Fusion005035
  Placement = pos=(0,0,-37) rot=(0,0,1;0rad)
  Source = -> Fusion005034
FEATURE [Part::FeaturePython] Connect001  # WARN: FeaturePython — macro-defined, semantics opaque (R4)
  Objects = -> [Sphere018,Fusion005028,Cut060,Cut067,Fusion005033,Fusion005035]
  Placement = pos=(-92,0,0) rot=(0,0,1;0rad)
  Tolerance = 0
FEATURE [Part::Sphere] Sphere021
  Angle1 = 0
  Angle2 = 90
  Angle3 = 360
  AttacherType = Attacher::AttachEngine3D
  Placement = pos=(0,-50,0) rot=(0,0,1;0rad)
  Radius = 5
FEATURE [Part::Box] Box031  label="Cube031"
  AttacherType = Attacher::AttachEngine3D
  Height = 10
  Length = 2
  Placement = pos=(-1,-55,-2) rot=(0,0,1;0rad)
  Width = 10
FEATURE [Part::Cylinder] Cylinder088
  Angle = 360
  AttacherType = Attacher::AttachEngine3D
  Height = 10
  Placement = pos=(0,-50,-12) rot=(0,0,1;0rad)
  Radius = 3
FEATURE [Part::Cylinder] Cylinder089
  Angle = 360
  AttacherType = Attacher::AttachEngine3D
  Height = 4
  Placement = pos=(18,0,-4) rot=(0,0,1;0rad)
  Radius = 5
FEATURE [Part::Box] Box032  label="Cube032"
  AttacherType = Attacher::AttachEngine3D
  Height = 10
  Length = 10
  Placement = pos=(2,-55,-2) rot=(0,0,1;0rad)
  Width = 10
FEATURE [Part::Cylinder] Cylinder090
  Angle = 360
  AttacherType = Attacher::AttachEngine3D
  Height = 4
  Placement = pos=(18,0,-4) rot=(0,0,1;0rad)
  Radius = 5
FEATURE [Part::Box] Box033  label="Cube033"
  AttacherType = Attacher::AttachEngine3D
  Height = 5
  Length = 4
  Placement = pos=(-2,-5,-10) rot=(0,0,1;0rad)
  Width = 10
FEATURE [Part::Cylinder] Cylinder091
  Angle = 360
  AttacherType = Attacher::AttachEngine3D
  Height = 10
  Placement = pos=(0,-50,-7) rot=(0,0,1;0rad)
  Radius = 5
FEATURE [Part::Cylinder] Cylinder092
  Angle = 360
  AttacherType = Attacher::AttachEngine3D
  Height = 10
  Placement = pos=(0,0,-10) rot=(0,0,1;0rad)
  Radius = 5
FEATURE [Part::Cylinder] Cylinder093
  Angle = 360
  AttacherType = Attacher::AttachEngine3D
  Height = 10
  Placement = pos=(0,0,-10) rot=(0,0,1;0rad)
  Radius = 5
FEATURE [Part::Cut] Cut083
  Base = -> Cylinder093
  Tool = -> Box033
FEATURE [Part::Box] Box034  label="Cube034"
  AttacherType = Attacher::AttachEngine3D
  Height = 10
  Length = 10
  Placement = pos=(-12,-55,-2) rot=(0,0,1;0rad)
  Width = 10
FEATURE [Part::Cylinder] Cylinder094
  Angle = 360
  AttacherType = Attacher::AttachEngine3D
  Height = 10
  Placement = pos=(0,0,-10) rot=(0,0,1;0rad)
  Radius = 2.5
FEATURE [Part::Cut] Cut082
  Base = -> Cut083
  Tool = -> Cylinder094
FEATURE [Part::Cylinder] Cylinder095
  Angle = 360
  AttacherType = Attacher::AttachEngine3D
  Height = 10
  Placement = pos=(18,0,-6) rot=(0,0,1;0rad)
  Radius = 3
FEATURE [Part::Cut] Cut084
  Base = -> Cylinder090
  Placement = pos=(-18,0,0) rot=(0,0,1;0rad)
  Tool = -> Cylinder095
FEATURE [Part::Sphere] Sphere022
  Angle1 = -90
  Angle2 = 90
  Angle3 = 360
  AttacherType = Attacher::AttachEngine3D
  Placement = pos=(0,0,-5) rot=(0,0,1;0rad)
  Radius = 6
FEATURE [Part::Box] Box035  label="Cube035"
  AttacherType = Attacher::AttachEngine3D
  Height = 10
  Length = 10
  Placement = pos=(2,-55,-2) rot=(0,0,1;0rad)
  Width = 10
FEATURE [Part::Cylinder] Cylinder096
  Angle = 360
  AttacherType = Attacher::AttachEngine3D
  Height = 10
  Placement = pos=(5,0,-7) rot=(0,-1,0;1.5708rad)
  Radius = 0.5
FEATURE [Part::Cut] Cut076
  Base = -> Cut082
  Tool = -> Cylinder096
FEATURE [Part::Cylinder] Cylinder097
  Angle = 360
  AttacherType = Attacher::AttachEngine3D
  Height = 10
  Placement = pos=(-5,0,-7) rot=(0,1,0;1.5708rad)
  Radius = 0.5
FEATURE [Part::Cylinder] Cylinder098
  Angle = 360
  AttacherType = Attacher::AttachEngine3D
  Height = 4
  Placement = pos=(-2,-50,1) rot=(0,1,0;1.5708rad)
  Radius = 2
FEATURE [Part::Sphere] Sphere023
  Angle1 = -90
  Angle2 = 90
  Angle3 = 360
  AttacherType = Attacher::AttachEngine3D
  Placement = pos=(0,0,-5) rot=(0,0,1;0rad)
  Radius = 6
FEATURE [Part::Sphere] Sphere024
  Angle1 = 0
  Angle2 = 90
  Angle3 = 360
  AttacherType = Attacher::AttachEngine3D
  Placement = pos=(0,-50,0) rot=(0,0,1;0rad)
  Radius = 5
FEATURE [Part::MultiCommon] Common017
  Shapes = -> [Cylinder091,Sphere024]
FEATURE [Part::Sphere] Sphere025
  Angle1 = 0
  Angle2 = 90
  Angle3 = 360
  AttacherType = Attacher::AttachEngine3D
  Radius = 5
FEATURE [Part::Cylinder] Cylinder099
  Angle = 360
  AttacherType = Attacher::AttachEngine3D
  Height = 4
  Placement = pos=(-2,-50,1) rot=(0,1,0;1.5708rad)
  Radius = 2
FEATURE [Part::MultiCommon] Common019
  Shapes = -> [Cut076,Sphere023]
FEATURE [Part::MultiFuse] Fusion005040
  Shapes = -> [Common019,Cut084]
FEATURE [Part::Refine] Fusion005038
  Placement = pos=(0,0,-18.5) rot=(0,0,1;0rad)
  Source = -> Fusion005040
FEATURE [Part::Cylinder] Cylinder100
  Angle = 360
  AttacherType = Attacher::AttachEngine3D
  Height = 10
  Placement = pos=(0,0,-10) rot=(0,0,1;0rad)
  Radius = 2.5
FEATURE [Part::Cylinder] Cylinder101
  Angle = 360
  AttacherType = Attacher::AttachEngine3D
  Height = 10
  Placement = pos=(0,-50,-10) rot=(0,0,1;0rad)
  Radius = 5
FEATURE [Part::MultiFuse] Fusion005041
  Shapes = -> [Common017,Cylinder101]
FEATURE [Part::Cut] Cut081
  Base = -> Fusion005041
  Tool = -> Box032
FEATURE [Part::Cut] Cut079
  Base = -> Cut081
  Tool = -> Box031
FEATURE [Part::Cut] Cut078
  Base = -> Cut079
  Tool = -> Box034
FEATURE [Part::Cut] Cut086
  Base = -> Cut078
  Tool = -> Cylinder088
FEATURE [Part::MultiFuse] Fusion005037
  Shapes = -> [Cut086,Cylinder099]
FEATURE [Part::Refine] Fusion005039
  Placement = pos=(0,50,-8.5) rot=(0,0,1;0rad)
  Source = -> Fusion005037
FEATURE [Part::Cut] Cut080
  Base = -> Fusion005039
  Placement = pos=(0,0,-18.5) rot=(0,0,1;0rad)
  Tool = -> Cylinder097
FEATURE [Part::Cylinder] Cylinder102
  Angle = 360
  AttacherType = Attacher::AttachEngine3D
  Height = 10
  Placement = pos=(0,-50,-7) rot=(0,0,1;0rad)
  Radius = 5
FEATURE [Part::Box] Box036  label="Cube036"
  AttacherType = Attacher::AttachEngine3D
  Height = 10
  Length = 10
  Placement = pos=(-12,-55,-2) rot=(0,0,1;0rad)
  Width = 10
FEATURE [Part::Box] Box037  label="Cube037"
  AttacherType = Attacher::AttachEngine3D
  Height = 10
  Length = 2
  Placement = pos=(-1,-55,-2) rot=(0,0,1;0rad)
  Width = 10
FEATURE [Part::MultiCommon] Common020
  Shapes = -> [Cylinder102,Sphere021]
FEATURE [Part::Cylinder] Cylinder103
  Angle = 360
  AttacherType = Attacher::AttachEngine3D
  Height = 10
  Placement = pos=(0,-50,-10) rot=(0,0,1;0rad)
  Radius = 5
FEATURE [Part::MultiFuse] Fusion005042
  Shapes = -> [Common020,Cylinder103]
FEATURE [Part::Cut] Cut088
  Base = -> Fusion005042
  Tool = -> Box035
FEATURE [Part::Cylinder] Cylinder104
  Angle = 360
  AttacherType = Attacher::AttachEngine3D
  Height = 10
  Placement = pos=(-5,0,-7) rot=(0,1,0;1.5708rad)
  Radius = 0.5
FEATURE [Part::Cut] Cut090
  Base = -> Cut088
  Tool = -> Box037
FEATURE [Part::Cut] Cut091
  Base = -> Cut090
  Tool = -> Box036
FEATURE [Part::Cylinder] Cylinder105
  Angle = 360
  AttacherType = Attacher::AttachEngine3D
  Height = 10
  Placement = pos=(0,-50,-12) rot=(0,0,1;0rad)
  Radius = 3
FEATURE [Part::Cut] Cut087
  Base = -> Cut091
  Tool = -> Cylinder105
FEATURE [Part::MultiFuse] Fusion005043
  Shapes = -> [Cut087,Cylinder098]
FEATURE [Part::Refine] Fusion005036
  Placement = pos=(0,50,-8.5) rot=(0,0,1;0rad)
  Source = -> Fusion005043
FEATURE [Part::Cut] Cut089
  Base = -> Fusion005036
  Placement = pos=(0,-2e-15,-18.5) rot=(1,0,0;3.14159rad)
  Tool = -> Cylinder104
FEATURE [Part::Cylinder] Cylinder106
  Angle = 360
  AttacherType = Attacher::AttachEngine3D
  Height = 10
  Placement = pos=(5,0,-7) rot=(0,-1,0;1.5708rad)
  Radius = 0.5
FEATURE [Part::Cylinder] Cylinder107
  Angle = 360
  AttacherType = Attacher::AttachEngine3D
  Height = 10
  Placement = pos=(5,0,-7) rot=(0,-1,0;1.5708rad)
  Radius = 0.5
FEATURE [Part::Box] Box038  label="Cube038"
  AttacherType = Attacher::AttachEngine3D
  Height = 5
  Length = 4
  Placement = pos=(-2,-5,-10) rot=(0,0,1;0rad)
  Width = 10
FEATURE [Part::Cylinder] Cylinder108
  Angle = 360
  AttacherType = Attacher::AttachEngine3D
  Height = 10
  Placement = pos=(0,0,-10) rot=(0,0,1;0rad)
  Radius = 5
FEATURE [Part::Cut] Cut092
  Base = -> Cylinder108
  Tool = -> Box038
FEATURE [Part::Cut] Cut095
  Base = -> Cut092
  Tool = -> Cylinder100
FEATURE [Part::Cut] Cut085
  Base = -> Cut095
  Tool = -> Cylinder107
FEATURE [Part::MultiCommon] Common018
  Shapes = -> [Cut085,Sphere022]
FEATURE [Part::Cylinder] Cylinder109
  Angle = 360
  AttacherType = Attacher::AttachEngine3D
  Height = 10
  Placement = pos=(18,0,-6) rot=(0,0,1;0rad)
  Radius = 3
FEATURE [Part::Cut] Cut096
  Base = -> Cylinder089
  Placement = pos=(-18,0,0) rot=(0,0,1;0rad)
  Tool = -> Cylinder109
FEATURE [Part::MultiFuse] Fusion005044
  Shapes = -> [Common018,Cut096]
FEATURE [Part::Refine] Fusion005045
  Placement = pos=(0,2e-15,-18.5) rot=(1,0,0;3.14159rad)
  Source = -> Fusion005044
FEATURE [Part::Box] Box039  label="Cube039"
  AttacherType = Attacher::AttachEngine3D
  Height = 5
  Length = 4
  Placement = pos=(-2,-5,-10) rot=(0,0,1;0rad)
  Width = 10
FEATURE [Part::Cut] Cut077
  Base = -> Cylinder092
  Tool = -> Box039
FEATURE [Part::Sphere] Sphere026
  Angle1 = -90
  Angle2 = 90
  Angle3 = 360
  AttacherType = Attacher::AttachEngine3D
  Placement = pos=(0,0,-5) rot=(0,0,1;0rad)
  Radius = 6
FEATURE [Part::Cylinder] Cylinder110
  Angle = 360
  AttacherType = Attacher::AttachEngine3D
  Height = 4
  Placement = pos=(18,0,-4) rot=(0,0,1;0rad)
  Radius = 5
FEATURE [Part::Cylinder] Cylinder111
  Angle = 360
  AttacherType = Attacher::AttachEngine3D
  Height = 10
  Placement = pos=(18,0,-6) rot=(0,0,1;0rad)
  Radius = 3
FEATURE [Part::Cut] Cut097
  Base = -> Cylinder110
  Placement = pos=(-18,0,0) rot=(0,0,1;0rad)
  Tool = -> Cylinder111
FEATURE [Part::Cylinder] Cylinder112
  Angle = 360
  AttacherType = Attacher::AttachEngine3D
  Height = 10
  Placement = pos=(0,0,-10) rot=(0,0,1;0rad)
  Radius = 2.5
FEATURE [Part::Cut] Cut093
  Base = -> Cut077
  Tool = -> Cylinder112
FEATURE [Part::Cut] Cut094
  Base = -> Cut093
  Tool = -> Cylinder106
FEATURE [Part::MultiCommon] Common021
  Shapes = -> [Cut094,Sphere026]
FEATURE [Part::MultiFuse] Fusion005046
  Shapes = -> [Common021,Cut097]
FEATURE [Part::Refine] Fusion005047
  Placement = pos=(0,0,-37) rot=(0,0,1;0rad)
  Source = -> Fusion005046
FEATURE [Part::FeaturePython] Connect002  # WARN: FeaturePython — macro-defined, semantics opaque (R4)
  Objects = -> [Sphere025,Fusion005038,Cut080,Cut089,Fusion005045,Fusion005047]
  Placement = pos=(-52,0,0) rot=(0,0,1;0rad)
  Tolerance = 0
FEATURE [Part::Sphere] Sphere027
  Angle1 = 0
  Angle2 = 90
  Angle3 = 360
  AttacherType = Attacher::AttachEngine3D
  Placement = pos=(0,-50,0) rot=(0,0,1;0rad)
  Radius = 5
FEATURE [Part::Box] Box040  label="Cube040"
  AttacherType = Attacher::AttachEngine3D
  Height = 10
  Length = 2
  Placement = pos=(-1,-55,-2) rot=(0,0,1;0rad)
  Width = 10
FEATURE [Part::Cylinder] Cylinder113
  Angle = 360
  AttacherType = Attacher::AttachEngine3D
  Height = 10
  Placement = pos=(0,-50,-12) rot=(0,0,1;0rad)
  Radius = 3
FEATURE [Part::Cylinder] Cylinder114
  Angle = 360
  AttacherType = Attacher::AttachEngine3D
  Height = 4
  Placement = pos=(18,0,-4) rot=(0,0,1;0rad)
  Radius = 5
FEATURE [Part::Box] Box041  label="Cube041"
  AttacherType = Attacher::AttachEngine3D
  Height = 10
  Length = 10
  Placement = pos=(2,-55,-2) rot=(0,0,1;0rad)
  Width = 10
FEATURE [Part::Cylinder] Cylinder115
  Angle = 360
  AttacherType = Attacher::AttachEngine3D
  Height = 4
  Placement = pos=(18,0,-4) rot=(0,0,1;0rad)
  Radius = 5
FEATURE [Part::Box] Box042  label="Cube042"
  AttacherType = Attacher::AttachEngine3D
  Height = 5
  Length = 4
  Placement = pos=(-2,-5,-10) rot=(0,0,1;0rad)
  Width = 10
FEATURE [Part::Cylinder] Cylinder116
  Angle = 360
  AttacherType = Attacher::AttachEngine3D
  Height = 10
  Placement = pos=(0,-50,-7) rot=(0,0,1;0rad)
  Radius = 5
FEATURE [Part::Cylinder] Cylinder117
  Angle = 360
  AttacherType = Attacher::AttachEngine3D
  Height = 10
  Placement = pos=(0,0,-10) rot=(0,0,1;0rad)
  Radius = 5
FEATURE [Part::Cylinder] Cylinder118
  Angle = 360
  AttacherType = Attacher::AttachEngine3D
  Height = 10
  Placement = pos=(0,0,-10) rot=(0,0,1;0rad)
  Radius = 5
FEATURE [Part::Cut] Cut105
  Base = -> Cylinder118
  Tool = -> Box042
FEATURE [Part::Box] Box043  label="Cube043"
  AttacherType = Attacher::AttachEngine3D
  Height = 10
  Length = 10
  Placement = pos=(-12,-55,-2) rot=(0,0,1;0rad)
  Width = 10
FEATURE [Part::Cylinder] Cylinder119
  Angle = 360
  AttacherType = Attacher::AttachEngine3D
  Height = 10
  Placement = pos=(0,0,-10) rot=(0,0,1;0rad)
  Radius = 2.5
FEATURE [Part::Cut] Cut104
  Base = -> Cut105
  Tool = -> Cylinder119
FEATURE [Part::Cylinder] Cylinder120
  Angle = 360
  AttacherType = Attacher::AttachEngine3D
  Height = 10
  Placement = pos=(18,0,-6) rot=(0,0,1;0rad)
  Radius = 3
FEATURE [Part::Cut] Cut106
  Base = -> Cylinder115
  Placement = pos=(-18,0,0) rot=(0,0,1;0rad)
  Tool = -> Cylinder120
FEATURE [Part::Sphere] Sphere028
  Angle1 = -90
  Angle2 = 90
  Angle3 = 360
  AttacherType = Attacher::AttachEngine3D
  Placement = pos=(0,0,-5) rot=(0,0,1;0rad)
  Radius = 6
FEATURE [Part::Box] Box044  label="Cube044"
  AttacherType = Attacher::AttachEngine3D
  Height = 10
  Length = 10
  Placement = pos=(2,-55,-2) rot=(0,0,1;0rad)
  Width = 10
FEATURE [Part::Cylinder] Cylinder121
  Angle = 360
  AttacherType = Attacher::AttachEngine3D
  Height = 10
  Placement = pos=(5,0,-7) rot=(0,-1,0;1.5708rad)
  Radius = 0.5
FEATURE [Part::Cut] Cut098
  Base = -> Cut104
  Tool = -> Cylinder121
FEATURE [Part::Cylinder] Cylinder122
  Angle = 360
  AttacherType = Attacher::AttachEngine3D
  Height = 10
  Placement = pos=(-5,0,-7) rot=(0,1,0;1.5708rad)
  Radius = 0.5
FEATURE [Part::Cylinder] Cylinder123
  Angle = 360
  AttacherType = Attacher::AttachEngine3D
  Height = 4
  Placement = pos=(-2,-50,1) rot=(0,1,0;1.5708rad)
  Radius = 2
FEATURE [Part::Sphere] Sphere029
  Angle1 = -90
  Angle2 = 90
  Angle3 = 360
  AttacherType = Attacher::AttachEngine3D
  Placement = pos=(0,0,-5) rot=(0,0,1;0rad)
  Radius = 6
FEATURE [Part::Sphere] Sphere030
  Angle1 = 0
  Angle2 = 90
  Angle3 = 360
  AttacherType = Attacher::AttachEngine3D
  Placement = pos=(0,-50,0) rot=(0,0,1;0rad)
  Radius = 5
FEATURE [Part::MultiCommon] Common022
  Shapes = -> [Cylinder116,Sphere030]
FEATURE [Part::Sphere] Sphere031
  Angle1 = 0
  Angle2 = 90
  Angle3 = 360
  AttacherType = Attacher::AttachEngine3D
  Radius = 5
FEATURE [Part::Cylinder] Cylinder124
  Angle = 360
  AttacherType = Attacher::AttachEngine3D
  Height = 4
  Placement = pos=(-2,-50,1) rot=(0,1,0;1.5708rad)
  Radius = 2
FEATURE [Part::MultiCommon] Common024
  Shapes = -> [Cut098,Sphere029]
FEATURE [Part::MultiFuse] Fusion005052
  Shapes = -> [Common024,Cut106]
FEATURE [Part::Refine] Fusion005050
  Placement = pos=(0,0,-18.5) rot=(0,0,1;0rad)
  Source = -> Fusion005052
FEATURE [Part::Cylinder] Cylinder125
  Angle = 360
  AttacherType = Attacher::AttachEngine3D
  Height = 10
  Placement = pos=(0,0,-10) rot=(0,0,1;0rad)
  Radius = 2.5
FEATURE [Part::Cylinder] Cylinder126
  Angle = 360
  AttacherType = Attacher::AttachEngine3D
  Height = 10
  Placement = pos=(0,-50,-10) rot=(0,0,1;0rad)
  Radius = 5
FEATURE [Part::MultiFuse] Fusion005053
  Shapes = -> [Common022,Cylinder126]
FEATURE [Part::Cut] Cut103
  Base = -> Fusion005053
  Tool = -> Box041
FEATURE [Part::Cut] Cut101
  Base = -> Cut103
  Tool = -> Box040
FEATURE [Part::Cut] Cut100
  Base = -> Cut101
  Tool = -> Box043
FEATURE [Part::Cut] Cut108
  Base = -> Cut100
  Tool = -> Cylinder113
FEATURE [Part::MultiFuse] Fusion005049
  Shapes = -> [Cut108,Cylinder124]
FEATURE [Part::Refine] Fusion005051
  Placement = pos=(0,50,-8.5) rot=(0,0,1;0rad)
  Source = -> Fusion005049
FEATURE [Part::Cut] Cut102
  Base = -> Fusion005051
  Placement = pos=(0,0,-18.5) rot=(0,0,1;0rad)
  Tool = -> Cylinder122
FEATURE [Part::Cylinder] Cylinder127
  Angle = 360
  AttacherType = Attacher::AttachEngine3D
  Height = 10
  Placement = pos=(0,-50,-7) rot=(0,0,1;0rad)
  Radius = 5
FEATURE [Part::Box] Box045  label="Cube045"
  AttacherType = Attacher::AttachEngine3D
  Height = 10
  Length = 10
  Placement = pos=(-12,-55,-2) rot=(0,0,1;0rad)
  Width = 10
FEATURE [Part::Box] Box046  label="Cube046"
  AttacherType = Attacher::AttachEngine3D
  Height = 10
  Length = 2
  Placement = pos=(-1,-55,-2) rot=(0,0,1;0rad)
  Width = 10
FEATURE [Part::MultiCommon] Common025
  Shapes = -> [Cylinder127,Sphere027]
FEATURE [Part::Cylinder] Cylinder128
  Angle = 360
  AttacherType = Attacher::AttachEngine3D
  Height = 10
  Placement = pos=(0,-50,-10) rot=(0,0,1;0rad)
  Radius = 5
FEATURE [Part::MultiFuse] Fusion005054
  Shapes = -> [Common025,Cylinder128]
FEATURE [Part::Cut] Cut110
  Base = -> Fusion005054
  Tool = -> Box044
FEATURE [Part::Cylinder] Cylinder129
  Angle = 360
  AttacherType = Attacher::AttachEngine3D
  Height = 10
  Placement = pos=(-5,0,-7) rot=(0,1,0;1.5708rad)
  Radius = 0.5
FEATURE [Part::Cut] Cut112
  Base = -> Cut110
  Tool = -> Box046
FEATURE [Part::Cut] Cut113
  Base = -> Cut112
  Tool = -> Box045
FEATURE [Part::Cylinder] Cylinder130
  Angle = 360
  AttacherType = Attacher::AttachEngine3D
  Height = 10
  Placement = pos=(0,-50,-12) rot=(0,0,1;0rad)
  Radius = 3
FEATURE [Part::Cut] Cut109
  Base = -> Cut113
  Tool = -> Cylinder130
FEATURE [Part::MultiFuse] Fusion005055
  Shapes = -> [Cut109,Cylinder123]
FEATURE [Part::Refine] Fusion005048
  Placement = pos=(0,50,-8.5) rot=(0,0,1;0rad)
  Source = -> Fusion005055
FEATURE [Part::Cut] Cut111
  Base = -> Fusion005048
  Placement = pos=(0,-2e-15,-18.5) rot=(1,0,0;3.14159rad)
  Tool = -> Cylinder129
FEATURE [Part::Cylinder] Cylinder131
  Angle = 360
  AttacherType = Attacher::AttachEngine3D
  Height = 10
  Placement = pos=(5,0,-7) rot=(0,-1,0;1.5708rad)
  Radius = 0.5
FEATURE [Part::Cylinder] Cylinder132
  Angle = 360
  AttacherType = Attacher::AttachEngine3D
  Height = 10
  Placement = pos=(5,0,-7) rot=(0,-1,0;1.5708rad)
  Radius = 0.5
FEATURE [Part::Box] Box047  label="Cube047"
  AttacherType = Attacher::AttachEngine3D
  Height = 5
  Length = 4
  Placement = pos=(-2,-5,-10) rot=(0,0,1;0rad)
  Width = 10
FEATURE [Part::Cylinder] Cylinder133
  Angle = 360
  AttacherType = Attacher::AttachEngine3D
  Height = 10
  Placement = pos=(0,0,-10) rot=(0,0,1;0rad)
  Radius = 5
FEATURE [Part::Cut] Cut114
  Base = -> Cylinder133
  Tool = -> Box047
FEATURE [Part::Cut] Cut117
  Base = -> Cut114
  Tool = -> Cylinder125
FEATURE [Part::Cut] Cut107
  Base = -> Cut117
  Tool = -> Cylinder132
FEATURE [Part::MultiCommon] Common023
  Shapes = -> [Cut107,Sphere028]
FEATURE [Part::Cylinder] Cylinder134
  Angle = 360
  AttacherType = Attacher::AttachEngine3D
  Height = 10
  Placement = pos=(18,0,-6) rot=(0,0,1;0rad)
  Radius = 3
FEATURE [Part::Cut] Cut118
  Base = -> Cylinder114
  Placement = pos=(-18,0,0) rot=(0,0,1;0rad)
  Tool = -> Cylinder134
FEATURE [Part::MultiFuse] Fusion005056
  Shapes = -> [Common023,Cut118]
FEATURE [Part::Refine] Fusion005057
  Placement = pos=(0,2e-15,-18.5) rot=(1,0,0;3.14159rad)
  Source = -> Fusion005056
FEATURE [Part::Box] Box048  label="Cube048"
  AttacherType = Attacher::AttachEngine3D
  Height = 5
  Length = 4
  Placement = pos=(-2,-5,-10) rot=(0,0,1;0rad)
  Width = 10
FEATURE [Part::Cut] Cut099
  Base = -> Cylinder117
  Tool = -> Box048
FEATURE [Part::Sphere] Sphere032
  Angle1 = -90
  Angle2 = 90
  Angle3 = 360
  AttacherType = Attacher::AttachEngine3D
  Placement = pos=(0,0,-5) rot=(0,0,1;0rad)
  Radius = 6
FEATURE [Part::Cylinder] Cylinder135
  Angle = 360
  AttacherType = Attacher::AttachEngine3D
  Height = 4
  Placement = pos=(18,0,-4) rot=(0,0,1;0rad)
  Radius = 5
FEATURE [Part::Cylinder] Cylinder136
  Angle = 360
  AttacherType = Attacher::AttachEngine3D
  Height = 10
  Placement = pos=(18,0,-6) rot=(0,0,1;0rad)
  Radius = 3
FEATURE [Part::Cut] Cut119
  Base = -> Cylinder135
  Placement = pos=(-18,0,0) rot=(0,0,1;0rad)
  Tool = -> Cylinder136
FEATURE [Part::Cylinder] Cylinder137
  Angle = 360
  AttacherType = Attacher::AttachEngine3D
  Height = 10
  Placement = pos=(0,0,-10) rot=(0,0,1;0rad)
  Radius = 2.5
FEATURE [Part::Cut] Cut115
  Base = -> Cut099
  Tool = -> Cylinder137
FEATURE [Part::Cut] Cut116
  Base = -> Cut115
  Tool = -> Cylinder131
FEATURE [Part::MultiCommon] Common026
  Shapes = -> [Cut116,Sphere032]
FEATURE [Part::MultiFuse] Fusion005058
  Shapes = -> [Common026,Cut119]
FEATURE [Part::Refine] Fusion005059
  Placement = pos=(0,0,-37) rot=(0,0,1;0rad)
  Source = -> Fusion005058
FEATURE [Part::FeaturePython] Connect003  # WARN: FeaturePython — macro-defined, semantics opaque (R4)
  Objects = -> [Sphere031,Fusion005050,Cut102,Cut111,Fusion005057,Fusion005059]
  Placement = pos=(-64.5,0,0) rot=(0,0,1;0rad)
  Tolerance = 0
FEATURE [Part::Box] Box049  label="Cube049"
  AttacherType = Attacher::AttachEngine3D
  Height = 20
  Length = 20
  Placement = pos=(0,0,-90.5) rot=(0,0,1;0rad)
  Width = 10
FEATURE [Part::Box] Box050  label="Cube050"
  AttacherType = Attacher::AttachEngine3D
  Height = 20
  Length = 20
  Placement = pos=(20.9492,0,-83.162) rot=(0,-1,0;0.785398rad)
  Width = 10
FEATURE [Part::Box] Box051  label="Cube051"
  AttacherType = Attacher::AttachEngine3D
  Height = 20
  Length = 20
  Placement = pos=(7.77579,0,-91.345) rot=(0,1,0;1.0472rad)
  Width = 10
FEATURE [Part::Cut] Cut120
  Base = -> Box049
  Tool = -> Box050
FEATURE [Part::Cut] Cut121
  Base = -> Cut120
  Tool = -> Box051
FEATURE [Part::Box] Box052  label="Cube052"
  AttacherType = Attacher::AttachEngine3D
  Height = 14
  Length = 10
  Placement = pos=(-3,0,-87.5) rot=(0,0,1;0rad)
  Width = 10
FEATURE [Part::Box] Box053  label="Cube053"
  AttacherType = Attacher::AttachEngine3D
  Height = 16
  Length = 7
  Placement = pos=(1.16726,2,-81.4896) rot=(0,1,0;0.785398rad)
  Width = 6
FEATURE [Part::Cut] Cut122
  Base = -> Cut121
  Tool = -> Box052
FEATURE [Part::Cut] Cut123
  Base = -> Cut122
  Tool = -> Box053
FEATURE [Part::Cylinder] Cylinder138
  Angle = 360
  AttacherType = Attacher::AttachEngine3D
  Height = 27
  Placement = pos=(4,5,-94) rot=(0,0,1;0rad)
  Radius = 3
FEATURE [Part::Cut] Cut124
  Base = -> Cut123
  Placement = pos=(12,0,10) rot=(0,0,1;0rad)
  Tool = -> Cylinder138
FEATURE [Part::Mirroring] Part__Mirroring  label="Cut124 (Mirror #1)"
  Base = (0.033699,1.2003,-70.5)
  Normal = (-0.999961,-0.00886039,1.19209e-07)
  Placement = pos=(-89,-4.5,10) rot=(0,0,1;0rad)
  Source = -> Cut124
FEATURE [Part::Box] Box054  label="Cube054"
  AttacherType = Attacher::AttachEngine3D
  Height = 10
  Length = 10
  Placement = pos=(-12,-55,-2) rot=(0,0,1;0rad)
  Width = 10
FEATURE [Part::Cylinder] Cylinder139
  Angle = 360
  AttacherType = Attacher::AttachEngine3D
  Height = 10
  Placement = pos=(0,-50,-7) rot=(0,0,1;0rad)
  Radius = 5
FEATURE [Part::Cylinder] Cylinder140
  Angle = 360
  AttacherType = Attacher::AttachEngine3D
  Height = 10
  Placement = pos=(-5,0,-7) rot=(0,1,0;1.5708rad)
  Radius = 0.5
FEATURE [Part::Box] Box055  label="Cube055"
  AttacherType = Attacher::AttachEngine3D
  Height = 10
  Length = 2
  Placement = pos=(-1,-55,-2) rot=(0,0,1;0rad)
  Width = 10
FEATURE [Part::Cylinder] Cylinder141
  Angle = 360
  AttacherType = Attacher::AttachEngine3D
  Height = 10
  Placement = pos=(0,-50,-10) rot=(0,0,1;0rad)
  Radius = 5
FEATURE [Part::Box] Box056  label="Cube056"
  AttacherType = Attacher::AttachEngine3D
  Height = 10
  Length = 10
  Placement = pos=(2,-55,-2) rot=(0,0,1;0rad)
  Width = 10
FEATURE [Part::Cylinder] Cylinder142
  Angle = 360
  AttacherType = Attacher::AttachEngine3D
  Height = 4
  Placement = pos=(-2,-50,1) rot=(0,1,0;1.5708rad)
  Radius = 2
FEATURE [Part::Cylinder] Cylinder143
  Angle = 360
  AttacherType = Attacher::AttachEngine3D
  Height = 10
  Placement = pos=(0,-50,-12) rot=(0,0,1;0rad)
  Radius = 3
FEATURE [Part::Sphere] Sphere033
  Angle1 = 0
  Angle2 = 90
  Angle3 = 360
  AttacherType = Attacher::AttachEngine3D
  Placement = pos=(0,-50,0) rot=(0,0,1;0rad)
  Radius = 5
FEATURE [Part::MultiCommon] Common027
  Shapes = -> [Cylinder139,Sphere033]
FEATURE [Part::MultiFuse] Fusion005061
  Shapes = -> [Common027,Cylinder141]
FEATURE [Part::Cut] Cut125
  Base = -> Fusion005061
  Tool = -> Box056
FEATURE [Part::Cut] Cut127
  Base = -> Cut125
  Tool = -> Box055
FEATURE [Part::Cut] Cut128
  Base = -> Cut127
  Tool = -> Box054
FEATURE [Part::Cut] Cut129
  Base = -> Cut128
  Tool = -> Cylinder143
FEATURE [Part::MultiFuse] Fusion005062
  Shapes = -> [Cut129,Cylinder142]
FEATURE [Part::Refine] Fusion005060
  Placement = pos=(0,50,-8.5) rot=(0,0,1;0rad)
  Source = -> Fusion005062
FEATURE [Part::Cut] Cut126
  Base = -> Fusion005060
  Placement = pos=(-115.123,0.188267,-52.1435) rot=(-0.382683,0,0.92388;3.14159rad)
  Tool = -> Cylinder140
FEATURE [Part::Sphere] Sphere034
  Angle1 = -90
  Angle2 = 90
  Angle3 = 360
  AttacherType = Attacher::AttachEngine3D
  Placement = pos=(0,0,-5) rot=(0,0,1;0rad)
  Radius = 6
FEATURE [Part::Cylinder] Cylinder144
  Angle = 360
  AttacherType = Attacher::AttachEngine3D
  Height = 10
  Placement = pos=(0,0,-10) rot=(0,0,1;0rad)
  Radius = 2.5
FEATURE [Part::Box] Box057  label="Cube057"
  AttacherType = Attacher::AttachEngine3D
  Height = 5
  Length = 4
  Placement = pos=(-2,-5,-10) rot=(0,0,1;0rad)
  Width = 10
FEATURE [Part::Cylinder] Cylinder145
  Angle = 360
  AttacherType = Attacher::AttachEngine3D
  Height = 10
  Placement = pos=(0,0,-10) rot=(0,0,1;0rad)
  Radius = 5
FEATURE [Part::Cut] Cut130
  Base = -> Cylinder145
  Tool = -> Box057
FEATURE [Part::Cylinder] Cylinder146
  Angle = 360
  AttacherType = Attacher::AttachEngine3D
  Height = 10
  Placement = pos=(5,0,-7) rot=(0,-1,0;1.5708rad)
  Radius = 0.5
FEATURE [Part::Cylinder] Cylinder147
  Angle = 360
  AttacherType = Attacher::AttachEngine3D
  Height = 4
  Placement = pos=(18,0,-4) rot=(0,0,1;0rad)
  Radius = 5
FEATURE [Part::Cut] Cut133
  Base = -> Cut130
  Tool = -> Cylinder144
FEATURE [Part::Cut] Cut132
  Base = -> Cut133
  Tool = -> Cylinder146
FEATURE [Part::Cylinder] Cylinder148
  Angle = 360
  AttacherType = Attacher::AttachEngine3D
  Height = 10
  Placement = pos=(18,0,-6) rot=(0,0,1;0rad)
  Radius = 3
FEATURE [Part::Cut] Cut131
  Base = -> Cylinder147
  Placement = pos=(-18,0,0) rot=(0,0,1;0rad)
  Tool = -> Cylinder148
FEATURE [Part::MultiCommon] Common028
  Shapes = -> [Cut132,Sphere034]
FEATURE [Part::MultiFuse] Fusion005064
  Shapes = -> [Common028,Cut131]
FEATURE [Part::Refine] Fusion005063
  Placement = pos=(-115.096,-6.4e-15,-52.182) rot=(-0.382683,0,0.92388;3.14159rad)
  Source = -> Fusion005064
FEATURE [Part::Box] Box058  label="Cube058"
  AttacherType = Attacher::AttachEngine3D
  Height = 10
  Length = 10
  Placement = pos=(2,-55,-2) rot=(0,0,1;0rad)
  Width = 10
FEATURE [Part::Box] Box059  label="Cube059"
  AttacherType = Attacher::AttachEngine3D
  Height = 10
  Length = 2
  Placement = pos=(-1,-55,-2) rot=(0,0,1;0rad)
  Width = 10
FEATURE [Part::Cylinder] Cylinder149
  Angle = 360
  AttacherType = Attacher::AttachEngine3D
  Height = 10
  Placement = pos=(0,-50,-10) rot=(0,0,1;0rad)
  Radius = 5
FEATURE [Part::Cylinder] Cylinder150
  Angle = 360
  AttacherType = Attacher::AttachEngine3D
  Height = 10
  Placement = pos=(0,-50,-7) rot=(0,0,1;0rad)
  Radius = 5
FEATURE [Part::Cylinder] Cylinder151
  Angle = 360
  AttacherType = Attacher::AttachEngine3D
  Height = 10
  Placement = pos=(0,-50,-12) rot=(0,0,1;0rad)
  Radius = 3
FEATURE [Part::Cylinder] Cylinder152
  Angle = 360
  AttacherType = Attacher::AttachEngine3D
  Height = 10
  Placement = pos=(-5,0,-7) rot=(0,1,0;1.5708rad)
  Radius = 0.5
FEATURE [Part::Box] Box060  label="Cube060"
  AttacherType = Attacher::AttachEngine3D
  Height = 10
  Length = 10
  Placement = pos=(-12,-55,-2) rot=(0,0,1;0rad)
  Width = 10
FEATURE [Part::Sphere] Sphere035
  Angle1 = 0
  Angle2 = 90
  Angle3 = 360
  AttacherType = Attacher::AttachEngine3D
  Placement = pos=(0,-50,0) rot=(0,0,1;0rad)
  Radius = 5
FEATURE [Part::MultiCommon] Common029
  Shapes = -> [Cylinder150,Sphere035]
FEATURE [Part::MultiFuse] Fusion005067
  Shapes = -> [Common029,Cylinder149]
FEATURE [Part::Cut] Cut135
  Base = -> Fusion005067
  Tool = -> Box058
FEATURE [Part::Cut] Cut136
  Base = -> Cut135
  Tool = -> Box059
FEATURE [Part::Cut] Cut137
  Base = -> Cut136
  Tool = -> Box060
FEATURE [Part::Cut] Cut134
  Base = -> Cut137
  Tool = -> Cylinder151
FEATURE [Part::Cylinder] Cylinder153
  Angle = 360
  AttacherType = Attacher::AttachEngine3D
  Height = 4
  Placement = pos=(-2,-50,1) rot=(0,1,0;1.5708rad)
  Radius = 2
FEATURE [Part::MultiFuse] Fusion005065
  Shapes = -> [Cut134,Cylinder153]
FEATURE [Part::Refine] Fusion005066
  Placement = pos=(0,50,-8.5) rot=(0,0,1;0rad)
  Source = -> Fusion005065
FEATURE [Part::Cut] Cut138
  Base = -> Fusion005066
  Placement = pos=(-128.204,0.188267,-39.0621) rot=(-0.382683,0,0.92388;3.14159rad)
  Tool = -> Cylinder152
FEATURE [Part::Sphere] Sphere036
  Angle1 = -90
  Angle2 = 90
  Angle3 = 360
  AttacherType = Attacher::AttachEngine3D
  Placement = pos=(0,0,-5) rot=(0,0,1;0rad)
  Radius = 6
FEATURE [Part::Cylinder] Cylinder154
  Angle = 360
  AttacherType = Attacher::AttachEngine3D
  Height = 10
  Placement = pos=(5,0,-7) rot=(0,-1,0;1.5708rad)
  Radius = 0.5
FEATURE [Part::Cylinder] Cylinder155
  Angle = 360
  AttacherType = Attacher::AttachEngine3D
  Height = 10
  Placement = pos=(18,0,-6) rot=(0,0,1;0rad)
  Radius = 3
FEATURE [Part::Cylinder] Cylinder156
  Angle = 360
  AttacherType = Attacher::AttachEngine3D
  Height = 4
  Placement = pos=(18,0,-4) rot=(0,0,1;0rad)
  Radius = 5
FEATURE [Part::Cut] Cut141
  Base = -> Cylinder156
  Placement = pos=(-18,0,0) rot=(0,0,1;0rad)
  Tool = -> Cylinder155
FEATURE [Part::Cylinder] Cylinder157
  Angle = 360
  AttacherType = Attacher::AttachEngine3D
  Height = 10
  Placement = pos=(0,0,-10) rot=(0,0,1;0rad)
  Radius = 5
FEATURE [Part::Cylinder] Cylinder158
  Angle = 360
  AttacherType = Attacher::AttachEngine3D
  Height = 10
  Placement = pos=(0,0,-10) rot=(0,0,1;0rad)
  Radius = 2.5
FEATURE [Part::Box] Box061  label="Cube061"
  AttacherType = Attacher::AttachEngine3D
  Height = 5
  Length = 4
  Placement = pos=(-2,-5,-10) rot=(0,0,1;0rad)
  Width = 10
FEATURE [Part::Cut] Cut139
  Base = -> Cylinder157
  Tool = -> Box061
FEATURE [Part::Cut] Cut142
  Base = -> Cut139
  Tool = -> Cylinder158
FEATURE [Part::Cut] Cut140
  Base = -> Cut142
  Tool = -> Cylinder154
FEATURE [Part::MultiCommon] Common030
  Shapes = -> [Cut140,Sphere036]
FEATURE [Part::MultiFuse] Fusion005068
  Shapes = -> [Common030,Cut141]
FEATURE [Part::Refine] Fusion005069
  Placement = pos=(-128.178,9.4e-15,-39.1005) rot=(-0.382683,0,0.92388;3.14159rad)
  Source = -> Fusion005068
FEATURE [Part::Sphere] Sphere037
  Angle1 = 0
  Angle2 = 90
  Angle3 = 360
  AttacherType = Attacher::AttachEngine3D
  Placement = pos=(-128,0,-39) rot=(0,1,0;5.49779rad)
  Radius = 5
FEATURE [Part::FeaturePython] Connect004  # WARN: FeaturePython — macro-defined, semantics opaque (R4)
  Objects = -> [Sphere037,Fusion005069,Cut138,Fusion005063,Cut126,Part__Mirroring]
  Placement = pos=(0,-0.5,-1) rot=(0,0,1;0rad)
  Tolerance = 0
FEATURE [Part::Box] Box062  label="Cube062"
  AttacherType = Attacher::AttachEngine3D
  Height = 50
  Length = 40
  Placement = pos=(-98,-5,-134.5) rot=(0,0,1;0rad)
  Width = 10
FEATURE [Part::Box] Box063  label="Cube063"
  AttacherType = Attacher::AttachEngine3D
  Height = 50
  Length = 40
  Placement = pos=(-51.1589,-5,-139.768) rot=(0,-1,0;0.523599rad)
  Width = 10
FEATURE [Part::Box] Box064  label="Cube064"
  AttacherType = Attacher::AttachEngine3D
  Height = 20
  Length = 10
  Placement = pos=(-98,-5,-118.5) rot=(0,0,1;0rad)
  Width = 10
FEATURE [Part::Box] Box065  label="Cube065"
  AttacherType = Attacher::AttachEngine3D
  Height = 24
  Length = 1
  Placement = pos=(-169,-5,-70.5) rot=(0,0,1;0rad)
  Width = 10
FEATURE [Part::Cut] Cut143
  Base = -> Box062
  Tool = -> Box063
FEATURE [Part::Cut] Cut144
  Base = -> Cut143
  Tool = -> Box064
FEATURE [Part::Box] Box066  label="Cube066"
  AttacherType = Attacher::AttachEngine3D
  Height = 20
  Length = 10
  Placement = pos=(-70,-5,-83.5) rot=(0,1,0;1.5708rad)
  Width = 10
FEATURE [Part::Cut] Cut145
  Base = -> Cut144
  Tool = -> Box066
FEATURE [Part::Box] Box067  label="Cube067"
  AttacherType = Attacher::AttachEngine3D
  Height = 10
  Length = 10
  Placement = pos=(-12,-55,-2) rot=(0,0,1;0rad)
  Width = 10
FEATURE [Part::Cylinder] Cylinder159
  Angle = 360
  AttacherType = Attacher::AttachEngine3D
  Height = 10
  Placement = pos=(0,-50,-7) rot=(0,0,1;0rad)
  Radius = 5
FEATURE [Part::Cylinder] Cylinder160
  Angle = 360
  AttacherType = Attacher::AttachEngine3D
  Height = 10
  Placement = pos=(-5,0,-7) rot=(0,1,0;1.5708rad)
  Radius = 0.5
FEATURE [Part::Box] Box068  label="Cube068"
  AttacherType = Attacher::AttachEngine3D
  Height = 10
  Length = 2
  Placement = pos=(-1,-55,-2) rot=(0,0,1;0rad)
  Width = 10
FEATURE [Part::Cylinder] Cylinder161
  Angle = 360
  AttacherType = Attacher::AttachEngine3D
  Height = 10
  Placement = pos=(0,-50,-10) rot=(0,0,1;0rad)
  Radius = 5
FEATURE [Part::Box] Box069  label="Cube069"
  AttacherType = Attacher::AttachEngine3D
  Height = 10
  Length = 10
  Placement = pos=(2,-55,-2) rot=(0,0,1;0rad)
  Width = 10
FEATURE [Part::Cylinder] Cylinder162
  Angle = 360
  AttacherType = Attacher::AttachEngine3D
  Height = 4
  Placement = pos=(-2,-50,1) rot=(0,1,0;1.5708rad)
  Radius = 2
FEATURE [Part::Cylinder] Cylinder163
  Angle = 360
  AttacherType = Attacher::AttachEngine3D
  Height = 10
  Placement = pos=(0,-50,-12) rot=(0,0,1;0rad)
  Radius = 3
FEATURE [Part::Sphere] Sphere038
  Angle1 = 0
  Angle2 = 90
  Angle3 = 360
  AttacherType = Attacher::AttachEngine3D
  Placement = pos=(0,-50,0) rot=(0,0,1;0rad)
  Radius = 5
FEATURE [Part::MultiCommon] Common031
  Shapes = -> [Cylinder159,Sphere038]
FEATURE [Part::MultiFuse] Fusion005071
  Shapes = -> [Common031,Cylinder161]
FEATURE [Part::Cut] Cut146
  Base = -> Fusion005071
  Tool = -> Box069
FEATURE [Part::Cut] Cut148
  Base = -> Cut146
  Tool = -> Box068
FEATURE [Part::Cut] Cut149
  Base = -> Cut148
  Tool = -> Box067
FEATURE [Part::Cut] Cut150
  Base = -> Cut149
  Tool = -> Cylinder163
FEATURE [Part::MultiFuse] Fusion005072
  Shapes = -> [Cut150,Cylinder162]
FEATURE [Part::Refine] Fusion005070
  Placement = pos=(0,50,-8.5) rot=(0,0,1;0rad)
  Source = -> Fusion005072
FEATURE [Part::Cut] Cut147
  Base = -> Fusion005070
  Placement = pos=(-92,0,-74) rot=(0,0,1;0rad)
  Tool = -> Cylinder160
FEATURE [Part::Box] Box070  label="Cube070"
  AttacherType = Attacher::AttachEngine3D
  Height = 10
  Length = 10
  Placement = pos=(-12,-55,-2) rot=(0,0,1;0rad)
  Width = 10
FEATURE [Part::Cylinder] Cylinder164
  Angle = 360
  AttacherType = Attacher::AttachEngine3D
  Height = 10
  Placement = pos=(0,-50,-7) rot=(0,0,1;0rad)
  Radius = 5
FEATURE [Part::Cylinder] Cylinder165
  Angle = 360
  AttacherType = Attacher::AttachEngine3D
  Height = 10
  Placement = pos=(-5,0,-7) rot=(0,1,0;1.5708rad)
  Radius = 0.5
FEATURE [Part::Box] Box071  label="Cube071"
  AttacherType = Attacher::AttachEngine3D
  Height = 10
  Length = 2
  Placement = pos=(-1,-55,-2) rot=(0,0,1;0rad)
  Width = 10
FEATURE [Part::Cylinder] Cylinder166
  Angle = 360
  AttacherType = Attacher::AttachEngine3D
  Height = 10
  Placement = pos=(0,-50,-10) rot=(0,0,1;0rad)
  Radius = 5
FEATURE [Part::Box] Box072  label="Cube072"
  AttacherType = Attacher::AttachEngine3D
  Height = 10
  Length = 10
  Placement = pos=(2,-55,-2) rot=(0,0,1;0rad)
  Width = 10
FEATURE [Part::Cylinder] Cylinder167
  Angle = 360
  AttacherType = Attacher::AttachEngine3D
  Height = 4
  Placement = pos=(-2,-50,1) rot=(0,1,0;1.5708rad)
  Radius = 2
FEATURE [Part::Cylinder] Cylinder168
  Angle = 360
  AttacherType = Attacher::AttachEngine3D
  Height = 10
  Placement = pos=(0,-50,-12) rot=(0,0,1;0rad)
  Radius = 3
FEATURE [Part::Sphere] Sphere039
  Angle1 = 0
  Angle2 = 90
  Angle3 = 360
  AttacherType = Attacher::AttachEngine3D
  Placement = pos=(0,-50,0) rot=(0,0,1;0rad)
  Radius = 5
FEATURE [Part::MultiCommon] Common032
  Shapes = -> [Cylinder164,Sphere039]
FEATURE [Part::MultiFuse] Fusion005074
  Shapes = -> [Common032,Cylinder166]
FEATURE [Part::Cut] Cut151
  Base = -> Fusion005074
  Tool = -> Box072
FEATURE [Part::Cut] Cut153
  Base = -> Cut151
  Tool = -> Box071
FEATURE [Part::Cut] Cut154
  Base = -> Cut153
  Tool = -> Box070
FEATURE [Part::Cut] Cut155
  Base = -> Cut154
  Tool = -> Cylinder168
FEATURE [Part::MultiFuse] Fusion005075
  Shapes = -> [Cut155,Cylinder167]
FEATURE [Part::Refine] Fusion005073
  Placement = pos=(0,50,-8.5) rot=(0,0,1;0rad)
  Source = -> Fusion005075
FEATURE [Part::Cut] Cut152
  Base = -> Fusion005073
  Placement = pos=(-77,0,-74) rot=(0,0,1;0rad)
  Tool = -> Cylinder165
FEATURE [Part::MultiFuse] Fusion005076
  Shapes = -> [Cut145,Cut147]
FEATURE [Part::MultiFuse] Fusion005077
  Shapes = -> [Fusion005076,Cut152]
FEATURE [Part::Refine] Fusion005077001
  Source = -> Fusion005077
FEATURE [Part::Cylinder] Cylinder169
  Angle = 360
  AttacherType = Attacher::AttachEngine3D
  Height = 5
  Placement = pos=(-92.5,0,-89.5) rot=(0,0,1;0rad)
  Radius = 3
FEATURE [Part::Cylinder] Cylinder170
  Angle = 360
  AttacherType = Attacher::AttachEngine3D
  Height = 5
  Placement = pos=(-77,0,-89.5) rot=(0,0,1;0rad)
  Radius = 3
FEATURE [Part::Cut] Cut156
  Base = -> Fusion005077001
  Tool = -> Cylinder169
FEATURE [Part::Cut] Cut157
  Base = -> Cut156
  Tool = -> Cylinder170
FEATURE [Part::Cylinder] Cylinder171
  Angle = 360
  AttacherType = Attacher::AttachEngine3D
  Height = 15
  Placement = pos=(-92,0,-91) rot=(0,1,0;1.5708rad)
  Radius = 2
FEATURE [Part::Cylinder] Cylinder172
  Angle = 360
  AttacherType = Attacher::AttachEngine3D
  Height = 50
  Placement = pos=(-81,0,-143.5) rot=(0,0,1;0rad)
  Radius = 2
FEATURE [Part::Cut] Cut158
  Base = -> Cut157
  Tool = -> Cylinder171
FEATURE [Part::Cut] Cut159
  Base = -> Cut158
  Tool = -> Cylinder172
FEATURE [Part::Cylinder] Cylinder173
  Angle = 360
  AttacherType = Attacher::AttachEngine3D
  Height = 30
  Placement = pos=(-69,0,-136) rot=(0,0,1;0rad)
  Radius = 2
FEATURE [Part::Cylinder] Cylinder174
  Angle = 360
  AttacherType = Attacher::AttachEngine3D
  Height = 30
  Placement = pos=(-61.5,0,-136) rot=(0,0,1;0rad)
  Radius = 2
FEATURE [Part::Cut] Cut160
  Base = -> Cut159
  Tool = -> Cylinder173
FEATURE [Part::Cut] Cut161
  Base = -> Cut160
  Placement = pos=(0,0,37) rot=(0,0,1;0rad)
  Tool = -> Cylinder174
FEATURE [Part::Cylinder] Cylinder175
  Angle = 360
  AttacherType = Attacher::AttachEngine3D
  Height = 43
  Placement = pos=(-93,0,-100.5) rot=(0,0,1;0rad)
  Radius = 3
FEATURE [Part::Cylinder] Cylinder176
  Angle = 360
  AttacherType = Attacher::AttachEngine3D
  Height = 43
  Placement = pos=(-93,0,-100.5) rot=(0,0,1;0rad)
  Radius = 2.85
FEATURE [Part::Cut] Cut162
  Base = -> Cut161
  Tool = -> Cylinder175
FEATURE [Part::Cylinder] Cylinder177
  Angle = 360
  AttacherType = Attacher::AttachEngine3D
  Height = 10
  Placement = pos=(0,-50,-7) rot=(0,0,1;0rad)
  Radius = 5
FEATURE [Part::Box] Box073  label="Cube073"
  AttacherType = Attacher::AttachEngine3D
  Height = 10
  Length = 10
  Placement = pos=(2,-55,-2) rot=(0,0,1;0rad)
  Width = 10
FEATURE [Part::Sphere] Sphere040
  Angle1 = 0
  Angle2 = 90
  Angle3 = 360
  AttacherType = Attacher::AttachEngine3D
  Placement = pos=(0,-50,0) rot=(0,0,1;0rad)
  Radius = 5
FEATURE [Part::Box] Box074  label="Cube074"
  AttacherType = Attacher::AttachEngine3D
  Height = 10
  Length = 2
  Placement = pos=(-1,-55,-2) rot=(0,0,1;0rad)
  Width = 10
FEATURE [Part::Box] Box075  label="Cube075"
  AttacherType = Attacher::AttachEngine3D
  Height = 20
  Length = 10
  Placement = pos=(-70,-5,-83.5) rot=(0,1,0;1.5708rad)
  Width = 10
FEATURE [Part::Box] Box076  label="Cube076"
  AttacherType = Attacher::AttachEngine3D
  Height = 10
  Length = 10
  Placement = pos=(-12,-55,-2) rot=(0,0,1;0rad)
  Width = 10
FEATURE [Part::Cylinder] Cylinder178
  Angle = 360
  AttacherType = Attacher::AttachEngine3D
  Height = 10
  Placement = pos=(0,-50,-12) rot=(0,0,1;0rad)
  Radius = 3
FEATURE [Part::Box] Box077  label="Cube077"
  AttacherType = Attacher::AttachEngine3D
  Height = 50
  Length = 40
  Placement = pos=(-98,-5,-134.5) rot=(0,0,1;0rad)
  Width = 10
FEATURE [Part::Cylinder] Cylinder179
  Angle = 360
  AttacherType = Attacher::AttachEngine3D
  Height = 10
  Placement = pos=(0,-50,-10) rot=(0,0,1;0rad)
  Radius = 5
FEATURE [Part::Box] Box078  label="Cube078"
  AttacherType = Attacher::AttachEngine3D
  Height = 20
  Length = 10
  Placement = pos=(-98,-5,-118.5) rot=(0,0,1;0rad)
  Width = 10
FEATURE [Part::Cylinder] Cylinder180
  Angle = 360
  AttacherType = Attacher::AttachEngine3D
  Height = 4
  Placement = pos=(-2,-50,1) rot=(0,1,0;1.5708rad)
  Radius = 2
FEATURE [Part::Box] Box079  label="Cube079"
  AttacherType = Attacher::AttachEngine3D
  Height = 50
  Length = 40
  Placement = pos=(-51.1589,-5,-139.768) rot=(0,-1,0;0.523599rad)
  Width = 10
FEATURE [Part::Cut] Cut165
  Base = -> Box077
  Tool = -> Box079
FEATURE [Part::Cylinder] Cylinder181
  Angle = 360
  AttacherType = Attacher::AttachEngine3D
  Height = 10
  Placement = pos=(-5,0,-7) rot=(0,1,0;1.5708rad)
  Radius = 0.5
FEATURE [Part::Cut] Cut170
  Base = -> Cut165
  Tool = -> Box078
FEATURE [Part::Cut] Cut168
  Base = -> Cut170
  Tool = -> Box075
FEATURE [Part::MultiCommon] Common033
  Shapes = -> [Cylinder177,Sphere040]
FEATURE [Part::MultiFuse] Fusion005077003
  Shapes = -> [Common033,Cylinder179]
FEATURE [Part::Cut] Cut169
  Base = -> Fusion005077003
  Tool = -> Box073
FEATURE [Part::Cut] Cut167
  Base = -> Cut169
  Tool = -> Box074
FEATURE [Part::Cut] Cut163
  Base = -> Cut167
  Tool = -> Box076
FEATURE [Part::Cut] Cut164
  Base = -> Cut163
  Tool = -> Cylinder178
FEATURE [Part::MultiFuse] Fusion005077002
  Shapes = -> [Cut164,Cylinder180]
FEATURE [Part::Refine] Fusion005077004
  Placement = pos=(0,50,-8.5) rot=(0,0,1;0rad)
  Source = -> Fusion005077002
FEATURE [Part::Cut] Cut166
  Base = -> Fusion005077004
  Placement = pos=(-92,0,-74) rot=(0,0,1;0rad)
  Tool = -> Cylinder181
FEATURE [Part::Cylinder] Cylinder182
  Angle = 360
  AttacherType = Attacher::AttachEngine3D
  Height = 30
  Placement = pos=(-61.5,0,-136) rot=(0,0,1;0rad)
  Radius = 2
FEATURE [Part::Cylinder] Cylinder183
  Angle = 360
  AttacherType = Attacher::AttachEngine3D
  Height = 10
  Placement = pos=(-5,0,-7) rot=(0,1,0;1.5708rad)
  Radius = 0.5
FEATURE [Part::Box] Box080  label="Cube080"
  AttacherType = Attacher::AttachEngine3D
  Height = 10
  Length = 2
  Placement = pos=(-1,-55,-2) rot=(0,0,1;0rad)
  Width = 10
FEATURE [Part::Cylinder] Cylinder184
  Angle = 360
  AttacherType = Attacher::AttachEngine3D
  Height = 10
  Placement = pos=(0,-50,-10) rot=(0,0,1;0rad)
  Radius = 5
FEATURE [Part::Box] Box081  label="Cube081"
  AttacherType = Attacher::AttachEngine3D
  Height = 10
  Length = 10
  Placement = pos=(2,-55,-2) rot=(0,0,1;0rad)
  Width = 10
FEATURE [Part::Cylinder] Cylinder185
  Angle = 360
  AttacherType = Attacher::AttachEngine3D
  Height = 4
  Placement = pos=(-2,-50,1) rot=(0,1,0;1.5708rad)
  Radius = 2
FEATURE [Part::Box] Box082  label="Cube082"
  AttacherType = Attacher::AttachEngine3D
  Height = 10
  Length = 10
  Placement = pos=(-12,-55,-2) rot=(0,0,1;0rad)
  Width = 10
FEATURE [Part::Cylinder] Cylinder186
  Angle = 360
  AttacherType = Attacher::AttachEngine3D
  Height = 10
  Placement = pos=(0,-50,-7) rot=(0,0,1;0rad)
  Radius = 5
FEATURE [Part::Cylinder] Cylinder187
  Angle = 360
  AttacherType = Attacher::AttachEngine3D
  Height = 10
  Placement = pos=(0,-50,-12) rot=(0,0,1;0rad)
  Radius = 3
FEATURE [Part::Sphere] Sphere041
  Angle1 = 0
  Angle2 = 90
  Angle3 = 360
  AttacherType = Attacher::AttachEngine3D
  Placement = pos=(0,-50,0) rot=(0,0,1;0rad)
  Radius = 5
FEATURE [Part::MultiCommon] Common034
  Shapes = -> [Cylinder186,Sphere041]
FEATURE [Part::MultiFuse] Fusion005077006
  Shapes = -> [Common034,Cylinder184]
FEATURE [Part::Cut] Cut172
  Base = -> Fusion005077006
  Tool = -> Box081
FEATURE [Part::Cut] Cut174
  Base = -> Cut172
  Tool = -> Box080
FEATURE [Part::Cut] Cut175
  Base = -> Cut174
  Tool = -> Box082
FEATURE [Part::Cut] Cut176
  Base = -> Cut175
  Tool = -> Cylinder187
FEATURE [Part::MultiFuse] Fusion005077007
  Shapes = -> [Cut176,Cylinder185]
FEATURE [Part::Refine] Fusion005077005
  Placement = pos=(0,50,-8.5) rot=(0,0,1;0rad)
  Source = -> Fusion005077007
FEATURE [Part::Cut] Cut173
  Base = -> Fusion005077005
  Placement = pos=(-77,0,-74) rot=(0,0,1;0rad)
  Tool = -> Cylinder183
FEATURE [Part::MultiFuse] Fusion005077008
  Shapes = -> [Cut168,Cut166]
FEATURE [Part::MultiFuse] Fusion005077010
  Shapes = -> [Fusion005077008,Cut173]
FEATURE [Part::Refine] Fusion005077009
  Source = -> Fusion005077010
FEATURE [Part::Cylinder] Cylinder188
  Angle = 360
  AttacherType = Attacher::AttachEngine3D
  Height = 30
  Placement = pos=(-69,0,-136) rot=(0,0,1;0rad)
  Radius = 2
FEATURE [Part::Cylinder] Cylinder189
  Angle = 360
  AttacherType = Attacher::AttachEngine3D
  Height = 5
  Placement = pos=(-92.5,0,-89.5) rot=(0,0,1;0rad)
  Radius = 3
FEATURE [Part::Cylinder] Cylinder190
  Angle = 360
  AttacherType = Attacher::AttachEngine3D
  Height = 50
  Placement = pos=(-81,0,-143.5) rot=(0,0,1;0rad)
  Radius = 2
FEATURE [Part::Cylinder] Cylinder191
  Angle = 360
  AttacherType = Attacher::AttachEngine3D
  Height = 15
  Placement = pos=(-92,0,-91) rot=(0,1,0;1.5708rad)
  Radius = 2
FEATURE [Part::Cut] Cut178
  Base = -> Fusion005077009
  Tool = -> Cylinder189
FEATURE [Part::Cylinder] Cylinder192
  Angle = 360
  AttacherType = Attacher::AttachEngine3D
  Height = 5
  Placement = pos=(-77,0,-89.5) rot=(0,0,1;0rad)
  Radius = 3
FEATURE [Part::Cut] Cut179
  Base = -> Cut178
  Tool = -> Cylinder192
FEATURE [Part::Cut] Cut177
  Base = -> Cut179
  Tool = -> Cylinder191
FEATURE [Part::Cut] Cut181
  Base = -> Cut177
  Tool = -> Cylinder190
FEATURE [Part::Cut] Cut180
  Base = -> Cut181
  Tool = -> Cylinder188
FEATURE [Part::Cut] Cut171
  Base = -> Cut180
  Placement = pos=(0,0,37) rot=(0,0,1;0rad)
  Tool = -> Cylinder182
FEATURE [Part::Cylinder] Cylinder193
  Angle = 360
  AttacherType = Attacher::AttachEngine3D
  Height = 43
  Placement = pos=(-93,0,-100.5) rot=(0,0,1;0rad)
  Radius = 3
FEATURE [Part::Cut] Cut182
  Base = -> Cut171
  Placement = pos=(132,0,0) rot=(0,0,1;0rad)
  Tool = -> Cylinder193
FEATURE [Part::Cylinder] Cylinder194
  Angle = 360
  AttacherType = Attacher::AttachEngine3D
  Height = 43
  Placement = pos=(125.5,0,-92.5) rot=(0,0,1;0rad)
  Radius = 2.85
FEATURE [Part::Cylinder] Cylinder195
  Angle = 360
  AttacherType = Attacher::AttachEngine3D
  Height = 10
  Placement = pos=(0,-50,-7) rot=(0,0,1;0rad)
  Radius = 5
FEATURE [Part::Box] Box084  label="Cube084"
  AttacherType = Attacher::AttachEngine3D
  Height = 10
  Length = 10
  Placement = pos=(2,-55,-2) rot=(0,0,1;0rad)
  Width = 10
FEATURE [Part::Sphere] Sphere042
  Angle1 = 0
  Angle2 = 90
  Angle3 = 360
  AttacherType = Attacher::AttachEngine3D
  Placement = pos=(0,-50,0) rot=(0,0,1;0rad)
  Radius = 5
FEATURE [Part::Box] Box085  label="Cube085"
  AttacherType = Attacher::AttachEngine3D
  Height = 10
  Length = 2
  Placement = pos=(-1,-55,-2) rot=(0,0,1;0rad)
  Width = 10
FEATURE [Part::Box] Box086  label="Cube086"
  AttacherType = Attacher::AttachEngine3D
  Height = 20
  Length = 10
  Placement = pos=(-70,-5,-83.5) rot=(0,1,0;1.5708rad)
  Width = 10
FEATURE [Part::Box] Box087  label="Cube087"
  AttacherType = Attacher::AttachEngine3D
  Height = 10
  Length = 10
  Placement = pos=(-12,-55,-2) rot=(0,0,1;0rad)
  Width = 10
FEATURE [Part::Cylinder] Cylinder196
  Angle = 360
  AttacherType = Attacher::AttachEngine3D
  Height = 10
  Placement = pos=(0,-50,-12) rot=(0,0,1;0rad)
  Radius = 3
FEATURE [Part::Box] Box088  label="Cube088"
  AttacherType = Attacher::AttachEngine3D
  Height = 50
  Length = 40
  Placement = pos=(-98,-5,-134.5) rot=(0,0,1;0rad)
  Width = 10
FEATURE [Part::Cylinder] Cylinder197
  Angle = 360
  AttacherType = Attacher::AttachEngine3D
  Height = 10
  Placement = pos=(0,-50,-10) rot=(0,0,1;0rad)
  Radius = 5
FEATURE [Part::Box] Box089  label="Cube089"
  AttacherType = Attacher::AttachEngine3D
  Height = 20
  Length = 10
  Placement = pos=(-98,-5,-118.5) rot=(0,0,1;0rad)
  Width = 10
FEATURE [Part::Cylinder] Cylinder198
  Angle = 360
  AttacherType = Attacher::AttachEngine3D
  Height = 4
  Placement = pos=(-2,-50,1) rot=(0,1,0;1.5708rad)
  Radius = 2
FEATURE [Part::Box] Box090  label="Cube090"
  AttacherType = Attacher::AttachEngine3D
  Height = 50
  Length = 40
  Placement = pos=(-51.1589,-5,-139.768) rot=(0,-1,0;0.523599rad)
  Width = 10
FEATURE [Part::Cut] Cut185
  Base = -> Box088
  Tool = -> Box090
FEATURE [Part::Cylinder] Cylinder199
  Angle = 360
  AttacherType = Attacher::AttachEngine3D
  Height = 10
  Placement = pos=(-5,0,-7) rot=(0,1,0;1.5708rad)
  Radius = 0.5
FEATURE [Part::Cut] Cut190
  Base = -> Cut185
  Tool = -> Box089
FEATURE [Part::Cut] Cut188
  Base = -> Cut190
  Tool = -> Box086
FEATURE [Part::MultiCommon] Common035
  Shapes = -> [Cylinder195,Sphere042]
FEATURE [Part::MultiFuse] Fusion005077012
  Shapes = -> [Common035,Cylinder197]
FEATURE [Part::Cut] Cut189
  Base = -> Fusion005077012
  Tool = -> Box084
FEATURE [Part::Cut] Cut187
  Base = -> Cut189
  Tool = -> Box085
FEATURE [Part::Cut] Cut183
  Base = -> Cut187
  Tool = -> Box087
FEATURE [Part::Cut] Cut184
  Base = -> Cut183
  Tool = -> Cylinder196
FEATURE [Part::MultiFuse] Fusion005077011
  Shapes = -> [Cut184,Cylinder198]
FEATURE [Part::Refine] Fusion005077013
  Placement = pos=(0,50,-8.5) rot=(0,0,1;0rad)
  Source = -> Fusion005077011
FEATURE [Part::Cut] Cut186
  Base = -> Fusion005077013
  Placement = pos=(-92,0,-74) rot=(0,0,1;0rad)
  Tool = -> Cylinder199
FEATURE [Part::Cylinder] Cylinder200
  Angle = 360
  AttacherType = Attacher::AttachEngine3D
  Height = 30
  Placement = pos=(-61.5,0,-136) rot=(0,0,1;0rad)
  Radius = 2
FEATURE [Part::Cylinder] Cylinder201
  Angle = 360
  AttacherType = Attacher::AttachEngine3D
  Height = 10
  Placement = pos=(-5,0,-7) rot=(0,1,0;1.5708rad)
  Radius = 0.5
FEATURE [Part::Box] Box091  label="Cube091"
  AttacherType = Attacher::AttachEngine3D
  Height = 10
  Length = 2
  Placement = pos=(-1,-55,-2) rot=(0,0,1;0rad)
  Width = 10
FEATURE [Part::Cylinder] Cylinder202
  Angle = 360
  AttacherType = Attacher::AttachEngine3D
  Height = 10
  Placement = pos=(0,-50,-10) rot=(0,0,1;0rad)
  Radius = 5
FEATURE [Part::Box] Box092  label="Cube092"
  AttacherType = Attacher::AttachEngine3D
  Height = 10
  Length = 10
  Placement = pos=(2,-55,-2) rot=(0,0,1;0rad)
  Width = 10
FEATURE [Part::Cylinder] Cylinder203
  Angle = 360
  AttacherType = Attacher::AttachEngine3D
  Height = 4
  Placement = pos=(-2,-50,1) rot=(0,1,0;1.5708rad)
  Radius = 2
FEATURE [Part::Box] Box093  label="Cube093"
  AttacherType = Attacher::AttachEngine3D
  Height = 10
  Length = 10
  Placement = pos=(-12,-55,-2) rot=(0,0,1;0rad)
  Width = 10
FEATURE [Part::Cylinder] Cylinder204
  Angle = 360
  AttacherType = Attacher::AttachEngine3D
  Height = 10
  Placement = pos=(0,-50,-7) rot=(0,0,1;0rad)
  Radius = 5
FEATURE [Part::Cylinder] Cylinder205
  Angle = 360
  AttacherType = Attacher::AttachEngine3D
  Height = 10
  Placement = pos=(0,-50,-12) rot=(0,0,1;0rad)
  Radius = 3
FEATURE [Part::Sphere] Sphere043
  Angle1 = 0
  Angle2 = 90
  Angle3 = 360
  AttacherType = Attacher::AttachEngine3D
  Placement = pos=(0,-50,0) rot=(0,0,1;0rad)
  Radius = 5
FEATURE [Part::MultiCommon] Common036
  Shapes = -> [Cylinder204,Sphere043]
FEATURE [Part::MultiFuse] Fusion005077015
  Shapes = -> [Common036,Cylinder202]
FEATURE [Part::Cut] Cut192
  Base = -> Fusion005077015
  Tool = -> Box092
FEATURE [Part::Cut] Cut194
  Base = -> Cut192
  Tool = -> Box091
FEATURE [Part::Cut] Cut195
  Base = -> Cut194
  Tool = -> Box093
FEATURE [Part::Cut] Cut196
  Base = -> Cut195
  Tool = -> Cylinder205
FEATURE [Part::MultiFuse] Fusion005077016
  Shapes = -> [Cut196,Cylinder203]
FEATURE [Part::Refine] Fusion005077014
  Placement = pos=(0,50,-8.5) rot=(0,0,1;0rad)
  Source = -> Fusion005077016
FEATURE [Part::Cut] Cut193
  Base = -> Fusion005077014
  Placement = pos=(-77,0,-74) rot=(0,0,1;0rad)
  Tool = -> Cylinder201
FEATURE [Part::MultiFuse] Fusion005077017
  Shapes = -> [Cut188,Cut186]
FEATURE [Part::MultiFuse] Fusion005077019
  Shapes = -> [Fusion005077017,Cut193]
FEATURE [Part::Refine] Fusion005077018
  Source = -> Fusion005077019
FEATURE [Part::Cylinder] Cylinder206
  Angle = 360
  AttacherType = Attacher::AttachEngine3D
  Height = 30
  Placement = pos=(-69,0,-136) rot=(0,0,1;0rad)
  Radius = 2
FEATURE [Part::Cylinder] Cylinder207
  Angle = 360
  AttacherType = Attacher::AttachEngine3D
  Height = 5
  Placement = pos=(-92.5,0,-89.5) rot=(0,0,1;0rad)
  Radius = 3
FEATURE [Part::Cylinder] Cylinder208
  Angle = 360
  AttacherType = Attacher::AttachEngine3D
  Height = 50
  Placement = pos=(-81,0,-143.5) rot=(0,0,1;0rad)
  Radius = 2
FEATURE [Part::Cylinder] Cylinder209
  Angle = 360
  AttacherType = Attacher::AttachEngine3D
  Height = 15
  Placement = pos=(-92,0,-91) rot=(0,1,0;1.5708rad)
  Radius = 2
FEATURE [Part::Cut] Cut198
  Base = -> Fusion005077018
  Tool = -> Cylinder207
FEATURE [Part::Cylinder] Cylinder210
  Angle = 360
  AttacherType = Attacher::AttachEngine3D
  Height = 5
  Placement = pos=(-77,0,-89.5) rot=(0,0,1;0rad)
  Radius = 3
FEATURE [Part::Cut] Cut199
  Base = -> Cut198
  Tool = -> Cylinder210
FEATURE [Part::Cut] Cut197
  Base = -> Cut199
  Tool = -> Cylinder209
FEATURE [Part::Cut] Cut201
  Base = -> Cut197
  Tool = -> Cylinder208
FEATURE [Part::Cut] Cut200
  Base = -> Cut201
  Tool = -> Cylinder206
FEATURE [Part::Cut] Cut191
  Base = -> Cut200
  Placement = pos=(0,0,37) rot=(0,0,1;0rad)
  Tool = -> Cylinder200
FEATURE [Part::Cylinder] Cylinder211
  Angle = 360
  AttacherType = Attacher::AttachEngine3D
  Height = 43
  Placement = pos=(-93,0,-100.5) rot=(0,0,1;0rad)
  Radius = 3
FEATURE [Part::Cut] Cut202
  Base = -> Cut191
  Placement = pos=(132,0,0) rot=(0,0,1;0rad)
  Tool = -> Cylinder211
FEATURE [Part::Box] Box094  label="Cube094"
  AttacherType = Attacher::AttachEngine3D
  Height = 43
  Length = 32
  Placement = pos=(55,-5,-90.5) rot=(0,0,1;0rad)
  Width = 10
FEATURE [Part::Cut] Cut203
  Base = -> Box094
  Placement = pos=(-101,0,0) rot=(0,0,1;0rad)
  Tool = -> Cut202
FEATURE [Part::Box] Box095  label="Cube095"
  AttacherType = Attacher::AttachEngine3D
  Height = 32
  Length = 13
  Placement = pos=(-37.8921,-7.5,-98.12) rot=(0,1,0;5.75959rad)
  Width = 16
FEATURE [Part::Cut] Cut204
  Base = -> Cut203
  Tool = -> Box095
FEATURE [Part::Refine] Cut204001
  Source = -> Cut204
FEATURE [Part::Cylinder] Cylinder212
  Angle = 360
  AttacherType = Attacher::AttachEngine3D
  Height = 10
  Placement = pos=(-45.5,-1,-56.5) rot=(0,0,1;0rad)
  Radius = 4.85
FEATURE [Part::Cut] Cut204002
  Base = -> Cut204001
  Placement = pos=(-141.5,0,0) rot=(0,0,1;0rad)
  Tool = -> Cylinder212
FEATURE [Part::Box] Box096  label="Cube096"
  AttacherType = Attacher::AttachEngine3D
  Height = 43
  Length = 32
  Placement = pos=(-192.84,-5,-109.749) rot=(0,1,0;5.75959rad)
  Width = 10
FEATURE [Part::Cut] Cut204003
  Base = -> Cut204002
  Tool = -> Box096
FEATURE [Part::Box] Box097  label="Cube097"
  AttacherType = Attacher::AttachEngine3D
  Height = 43
  Length = 12.5
  Placement = pos=(-168,-5,-90.5) rot=(0,0,1;0rad)
  Width = 10
FEATURE [Part::Box] Box098  label="Cube098"
  AttacherType = Attacher::AttachEngine3D
  Height = 43
  Length = 12.5
  Placement = pos=(-168,-5,-90.5) rot=(0,0,1;0rad)
  Width = 10
FEATURE [Part::Cut] Cut204004
  Base = -> Cut204003
  Tool = -> Box097
FEATURE [Part::Box] Box099  label="Cube099"
  AttacherType = Attacher::AttachEngine3D
  Height = 17
  Length = 12
  Placement = pos=(-167.14,-5,-90.45) rot=(0,1,0;5.75959rad)
  Width = 10
FEATURE [Part::Box] Box100  label="Cube100"
  AttacherType = Attacher::AttachEngine3D
  Height = 17
  Length = 12
  Placement = pos=(-167.14,-5,-90.45) rot=(0,-1,0;0.523599rad)
  Width = 10
FEATURE [Part::Cut] Cut204005
  Base = -> Cut204004
  Tool = -> Box099
FEATURE [Part::MultiFuse] Fusion005077020
  Shapes = -> [Box098,Box100]
FEATURE [Part::Refine] Fusion005077020001
  Source = -> Fusion005077020
FEATURE [Part::Box] Box101  label="Cube101"
  AttacherType = Attacher::AttachEngine3D
  Height = 20
  Length = 10
  Placement = pos=(-168.492,-5,-108.103) rot=(0,1,0;5.75959rad)
  Width = 10
FEATURE [Part::Cut] Cut204006
  Base = -> Fusion005077020001
  Tool = -> Box101
FEATURE [Part::Refine] Cut204006001
  Placement = pos=(110,0,0) rot=(0,0,1;0rad)
  Source = -> Cut204006
FEATURE [Part::Box] Box102  label="Cube102"
  AttacherType = Attacher::AttachEngine3D
  Height = 24
  Length = 1.5
  Placement = pos=(-189.24,-5,-81.947) rot=(0,1,0;1.0472rad)
  Width = 10
FEATURE [Part::Cut] Cut204006002
  Base = -> Cut204005
  Tool = -> Box065
FEATURE [Part::Cut] Cut204006003
  Base = -> Cut204006002
  Placement = pos=(111,0,0) rot=(0,0,1;0rad)
  Tool = -> Box102
FEATURE [Part::Box] Box103  label="Cube103"
  AttacherType = Attacher::AttachEngine3D
  Height = 10
  Length = 2
  Placement = pos=(-57.5,-5,-72) rot=(0,0,1;0rad)
  Width = 10
FEATURE [Part::Cut] Cut204006004
  Base = -> Cut204006003
  Tool = -> Box103
FEATURE [Part::Cylinder] Cylinder213
  Angle = 360
  AttacherType = Attacher::AttachEngine3D
  Height = 22
  Placement = pos=(-64.5,0,-69.5) rot=(0,0,1;0rad)
  Radius = 3
FEATURE [Part::Box] Box104  label="Cube104"
  AttacherType = Attacher::AttachEngine3D
  Height = 25
  Length = 2
  Placement = pos=(-59,-5,-72) rot=(0,0,1;0rad)
  Width = 10
FEATURE [Part::Cut] Cut204006005
  Base = -> Cut204006004
  Tool = -> Box104
FEATURE [Part::Box] Box105  label="Cube105"
  AttacherType = Attacher::AttachEngine3D
  Height = 10
  Length = 2
  Placement = pos=(-1,-55,-2) rot=(0,0,1;0rad)
  Width = 10
FEATURE [Part::Cylinder] Cylinder214
  Angle = 360
  AttacherType = Attacher::AttachEngine3D
  Height = 4
  Placement = pos=(-2,-50,1) rot=(0,1,0;1.5708rad)
  Radius = 2
FEATURE [Part::Cylinder] Cylinder215
  Angle = 360
  AttacherType = Attacher::AttachEngine3D
  Height = 10
  Placement = pos=(0,-50,-7) rot=(0,0,1;0rad)
  Radius = 5
FEATURE [Part::Sphere] Sphere044
  Angle1 = 0
  Angle2 = 90
  Angle3 = 360
  AttacherType = Attacher::AttachEngine3D
  Placement = pos=(0,-50,0) rot=(0,0,1;0rad)
  Radius = 5
FEATURE [Part::MultiCommon] Common037
  Shapes = -> [Cylinder215,Sphere044]
FEATURE [Part::Cylinder] Cylinder216
  Angle = 360
  AttacherType = Attacher::AttachEngine3D
  Height = 10
  Placement = pos=(0,-50,-10) rot=(0,0,1;0rad)
  Radius = 5
FEATURE [Part::MultiFuse] Fusion005077020003
  Shapes = -> [Common037,Cylinder216]
FEATURE [Part::Box] Box106  label="Cube106"
  AttacherType = Attacher::AttachEngine3D
  Height = 10
  Length = 10
  Placement = pos=(2,-55,-2) rot=(0,0,1;0rad)
  Width = 10
FEATURE [Part::Box] Box107  label="Cube107"
  AttacherType = Attacher::AttachEngine3D
  Height = 10
  Length = 10
  Placement = pos=(-12,-55,-2) rot=(0,0,1;0rad)
  Width = 10
FEATURE [Part::Cut] Cut204006007
  Base = -> Fusion005077020003
  Tool = -> Box106
FEATURE [Part::Cylinder] Cylinder217
  Angle = 360
  AttacherType = Attacher::AttachEngine3D
  Height = 10
  Placement = pos=(-5,0,-7) rot=(0,1,0;1.5708rad)
  Radius = 0.5
FEATURE [Part::Cut] Cut204006009
  Base = -> Cut204006007
  Tool = -> Box105
FEATURE [Part::Cut] Cut204006010
  Base = -> Cut204006009
  Tool = -> Box107
FEATURE [Part::Cylinder] Cylinder218
  Angle = 360
  AttacherType = Attacher::AttachEngine3D
  Height = 10
  Placement = pos=(0,-50,-12) rot=(0,0,1;0rad)
  Radius = 3
FEATURE [Part::Cut] Cut204006006
  Base = -> Cut204006010
  Tool = -> Cylinder218
FEATURE [Part::MultiFuse] Fusion005077020002
  Shapes = -> [Cut204006006,Cylinder214]
FEATURE [Part::Refine] Fusion005077020004
  Placement = pos=(0,50,-8.5) rot=(0,0,1;0rad)
  Source = -> Fusion005077020002
FEATURE [Part::Cut] Cut204006008
  Base = -> Fusion005077020004
  Placement = pos=(-64.5,0,-37) rot=(0,0,1;0rad)
  Tool = -> Cylinder217
FEATURE [Part::Box] Box108  label="Cube108"
  AttacherType = Attacher::AttachEngine3D
  Height = 10
  Length = 2
  Placement = pos=(-1,-55,-2) rot=(0,0,1;0rad)
  Width = 10
FEATURE [Part::Cylinder] Cylinder219
  Angle = 360
  AttacherType = Attacher::AttachEngine3D
  Height = 4
  Placement = pos=(-2,-50,1) rot=(0,1,0;1.5708rad)
  Radius = 2
FEATURE [Part::Cylinder] Cylinder220
  Angle = 360
  AttacherType = Attacher::AttachEngine3D
  Height = 10
  Placement = pos=(0,-50,-7) rot=(0,0,1;0rad)
  Radius = 5
FEATURE [Part::Sphere] Sphere045
  Angle1 = 0
  Angle2 = 90
  Angle3 = 360
  AttacherType = Attacher::AttachEngine3D
  Placement = pos=(0,-50,0) rot=(0,0,1;0rad)
  Radius = 5
FEATURE [Part::MultiCommon] Common038
  Shapes = -> [Cylinder220,Sphere045]
FEATURE [Part::Cylinder] Cylinder221
  Angle = 360
  AttacherType = Attacher::AttachEngine3D
  Height = 10
  Placement = pos=(0,-50,-10) rot=(0,0,1;0rad)
  Radius = 5
FEATURE [Part::MultiFuse] Fusion005077020006
  Shapes = -> [Common038,Cylinder221]
FEATURE [Part::Box] Box109  label="Cube109"
  AttacherType = Attacher::AttachEngine3D
  Height = 10
  Length = 10
  Placement = pos=(2,-55,-2) rot=(0,0,1;0rad)
  Width = 10
FEATURE [Part::Box] Box110  label="Cube110"
  AttacherType = Attacher::AttachEngine3D
  Height = 10
  Length = 10
  Placement = pos=(-12,-55,-2) rot=(0,0,1;0rad)
  Width = 10
FEATURE [Part::Cut] Cut204006012
  Base = -> Fusion005077020006
  Tool = -> Box109
FEATURE [Part::Cylinder] Cylinder222
  Angle = 360
  AttacherType = Attacher::AttachEngine3D
  Height = 10
  Placement = pos=(-5,0,-7) rot=(0,1,0;1.5708rad)
  Radius = 0.5
FEATURE [Part::Cut] Cut204006014
  Base = -> Cut204006012
  Tool = -> Box108
FEATURE [Part::Cut] Cut204006015
  Base = -> Cut204006014
  Tool = -> Box110
FEATURE [Part::Cylinder] Cylinder223
  Angle = 360
  AttacherType = Attacher::AttachEngine3D
  Height = 10
  Placement = pos=(0,-50,-12) rot=(0,0,1;0rad)
  Radius = 3
FEATURE [Part::Cut] Cut204006011
  Base = -> Cut204006015
  Tool = -> Cylinder223
FEATURE [Part::MultiFuse] Fusion005077020005
  Shapes = -> [Cut204006011,Cylinder219]
FEATURE [Part::Refine] Fusion005077020007
  Placement = pos=(0,50,-8.5) rot=(0,0,1;0rad)
  Source = -> Fusion005077020005
FEATURE [Part::Cut] Cut204006013
  Base = -> Fusion005077020007
  Placement = pos=(-52,0,-37) rot=(0,0,1;0rad)
  Tool = -> Cylinder222
FEATURE [Part::MultiFuse] Fusion005077020008
  Shapes = -> [Cut204006005,Cut204006008]
FEATURE [Part::Cylinder] Cylinder224
  Angle = 360
  AttacherType = Attacher::AttachEngine3D
  Height = 37
  Placement = pos=(-52,0,-84.5) rot=(0,0,1;0rad)
  Radius = 3
FEATURE [Part::Cut] Cut204006016
  Base = -> Fusion005077020008
  Tool = -> Cylinder213
FEATURE [Part::Cylinder] Cylinder225
  Angle = 360
  AttacherType = Attacher::AttachEngine3D
  Height = 10
  Placement = pos=(-69.9365,0,-70.8157) rot=(0,1,0;0.523599rad)
  Radius = 2
FEATURE [Part::Cut] Cut204006017
  Base = -> Cut204006016
  Tool = -> Cylinder225
FEATURE [Part::MultiFuse] Fusion005077020009
  Shapes = -> [Cut204006001,Cut204006013]
FEATURE [Part::Cut] Cut204006018
  Base = -> Fusion005077020009
  Tool = -> Cylinder224
FEATURE [Part::Cylinder] Cylinder227
  Angle = 360
  AttacherType = Attacher::AttachEngine3D
  Height = 10
  Placement = pos=(-62.0416,0,-84.0208) rot=(0,1,0;0.785398rad)
  Radius = 2
FEATURE [Part::Cut] Cut204006019
  Base = -> Cut204006018
  Tool = -> Cylinder227
FEATURE [Part::Box] Box111  label="Cube111"
  AttacherType = Attacher::AttachEngine3D
  Height = 43
  Length = 32
  Placement = pos=(-192.84,-5,-109.749) rot=(0,-1,0;0.523599rad)
  Width = 10
FEATURE [Part::Box] Box112  label="Cube112"
  AttacherType = Attacher::AttachEngine3D
  Height = 10
  Length = 2
  Placement = pos=(-1,-55,-2) rot=(0,0,1;0rad)
  Width = 10
FEATURE [Part::Box] Box113  label="Cube113"
  AttacherType = Attacher::AttachEngine3D
  Height = 50
  Length = 40
  Placement = pos=(-51.1589,-5,-139.768) rot=(0,-1,0;0.523599rad)
  Width = 10
FEATURE [Part::Cylinder] Cylinder228
  Angle = 360
  AttacherType = Attacher::AttachEngine3D
  Height = 30
  Placement = pos=(-61.5,0,-136) rot=(0,0,1;0rad)
  Radius = 2
FEATURE [Part::Box] Box114  label="Cube114"
  AttacherType = Attacher::AttachEngine3D
  Height = 24
  Length = 1
  Placement = pos=(-169,-5,-70.5) rot=(0,0,1;0rad)
  Width = 10
FEATURE [Part::Box] Box115  label="Cube115"
  AttacherType = Attacher::AttachEngine3D
  Height = 10
  Length = 2
  Placement = pos=(-1,-55,-2) rot=(0,0,1;0rad)
  Width = 10
FEATURE [Part::Cylinder] Cylinder229
  Angle = 360
  AttacherType = Attacher::AttachEngine3D
  Height = 10
  Placement = pos=(-45.5,-1,-56.5) rot=(0,0,1;0rad)
  Radius = 4.85
FEATURE [Part::Box] Box116  label="Cube116"
  AttacherType = Attacher::AttachEngine3D
  Height = 43
  Length = 32
  Placement = pos=(55,-5,-90.5) rot=(0,0,1;0rad)
  Width = 10
FEATURE [Part::Box] Box117  label="Cube117"
  AttacherType = Attacher::AttachEngine3D
  Height = 10
  Length = 10
  Placement = pos=(2,-55,-2) rot=(0,0,1;0rad)
  Width = 10
FEATURE [Part::Box] Box118  label="Cube118"
  AttacherType = Attacher::AttachEngine3D
  Height = 10
  Length = 10
  Placement = pos=(-12,-55,-2) rot=(0,0,1;0rad)
  Width = 10
FEATURE [Part::Box] Box119  label="Cube119"
  AttacherType = Attacher::AttachEngine3D
  Height = 20
  Length = 10
  Placement = pos=(-70,-5,-83.5) rot=(0,1,0;1.5708rad)
  Width = 10
FEATURE [Part::Box] Box120  label="Cube120"
  AttacherType = Attacher::AttachEngine3D
  Height = 50
  Length = 40
  Placement = pos=(-98,-5,-134.5) rot=(0,0,1;0rad)
  Width = 10
FEATURE [Part::Cylinder] Cylinder230
  Angle = 360
  AttacherType = Attacher::AttachEngine3D
  Height = 10
  Placement = pos=(-5,0,-7) rot=(0,1,0;1.5708rad)
  Radius = 0.5
FEATURE [Part::Box] Box121  label="Cube121"
  AttacherType = Attacher::AttachEngine3D
  Height = 10
  Length = 10
  Placement = pos=(2,-55,-2) rot=(0,0,1;0rad)
  Width = 10
FEATURE [Part::Cylinder] Cylinder231
  Angle = 360
  AttacherType = Attacher::AttachEngine3D
  Height = 10
  Placement = pos=(0,-50,-10) rot=(0,0,1;0rad)
  Radius = 5
FEATURE [Part::Cylinder] Cylinder232
  Angle = 360
  AttacherType = Attacher::AttachEngine3D
  Height = 10
  Placement = pos=(-5,0,-7) rot=(0,1,0;1.5708rad)
  Radius = 0.5
FEATURE [Part::Cylinder] Cylinder233
  Angle = 360
  AttacherType = Attacher::AttachEngine3D
  Height = 4
  Placement = pos=(-2,-50,1) rot=(0,1,0;1.5708rad)
  Radius = 2
FEATURE [Part::Box] Box122  label="Cube122"
  AttacherType = Attacher::AttachEngine3D
  Height = 10
  Length = 10
  Placement = pos=(2,-55,-2) rot=(0,0,1;0rad)
  Width = 10
FEATURE [Part::Cylinder] Cylinder234
  Angle = 360
  AttacherType = Attacher::AttachEngine3D
  Height = 10
  Placement = pos=(0,-50,-7) rot=(0,0,1;0rad)
  Radius = 5
FEATURE [Part::Cylinder] Cylinder235
  Angle = 360
  AttacherType = Attacher::AttachEngine3D
  Height = 4
  Placement = pos=(-2,-50,1) rot=(0,1,0;1.5708rad)
  Radius = 2
FEATURE [Part::Cylinder] Cylinder236
  Angle = 360
  AttacherType = Attacher::AttachEngine3D
  Height = 10
  Placement = pos=(-5,0,-7) rot=(0,1,0;1.5708rad)
  Radius = 0.5
FEATURE [Part::Cut] Cut204006025
  Base = -> Box120
  Tool = -> Box113
FEATURE [Part::Cylinder] Cylinder237
  Angle = 360
  AttacherType = Attacher::AttachEngine3D
  Height = 10
  Placement = pos=(0,-50,-10) rot=(0,0,1;0rad)
  Radius = 5
FEATURE [Part::Box] Box123  label="Cube123"
  AttacherType = Attacher::AttachEngine3D
  Height = 20
  Length = 10
  Placement = pos=(-98,-5,-118.5) rot=(0,0,1;0rad)
  Width = 10
FEATURE [Part::Cut] Cut204006024
  Base = -> Cut204006025
  Tool = -> Box123
FEATURE [Part::Cut] Cut204006022
  Base = -> Cut204006024
  Tool = -> Box119
FEATURE [Part::Cylinder] Cylinder238
  Angle = 360
  AttacherType = Attacher::AttachEngine3D
  Height = 10
  Placement = pos=(0,-50,-12) rot=(0,0,1;0rad)
  Radius = 3
FEATURE [Part::Sphere] Sphere046
  Angle1 = 0
  Angle2 = 90
  Angle3 = 360
  AttacherType = Attacher::AttachEngine3D
  Placement = pos=(0,-50,0) rot=(0,0,1;0rad)
  Radius = 5
FEATURE [Part::MultiCommon] Common040
  Shapes = -> [Cylinder234,Sphere046]
FEATURE [Part::MultiFuse] Fusion005077020012
  Shapes = -> [Common040,Cylinder231]
FEATURE [Part::Box] Box124  label="Cube124"
  AttacherType = Attacher::AttachEngine3D
  Height = 10
  Length = 10
  Placement = pos=(-12,-55,-2) rot=(0,0,1;0rad)
  Width = 10
FEATURE [Part::Cut] Cut204006030
  Base = -> Fusion005077020012
  Tool = -> Box117
FEATURE [Part::Cut] Cut204006023
  Base = -> Cut204006030
  Tool = -> Box112
FEATURE [Part::Cut] Cut204006029
  Base = -> Cut204006023
  Tool = -> Box124
FEATURE [Part::Cut] Cut204006020
  Base = -> Cut204006029
  Tool = -> Cylinder238
FEATURE [Part::MultiFuse] Fusion005077020011
  Shapes = -> [Cut204006020,Cylinder235]
FEATURE [Part::Refine] Fusion005077020010
  Placement = pos=(0,50,-8.5) rot=(0,0,1;0rad)
  Source = -> Fusion005077020011
FEATURE [Part::Cut] Cut204006026
  Base = -> Fusion005077020010
  Placement = pos=(-92,0,-74) rot=(0,0,1;0rad)
  Tool = -> Cylinder230
FEATURE [Part::Box] Box125  label="Cube125"
  AttacherType = Attacher::AttachEngine3D
  Height = 32
  Length = 13
  Placement = pos=(-37.8921,-7.5,-98.12) rot=(0,-1,0;0.523599rad)
  Width = 16
FEATURE [Part::Box] Box126  label="Cube126"
  AttacherType = Attacher::AttachEngine3D
  Height = 10
  Length = 2
  Placement = pos=(-57.5,-5,-72) rot=(0,0,1;0rad)
  Width = 10
FEATURE [Part::Cylinder] Cylinder239
  Angle = 360
  AttacherType = Attacher::AttachEngine3D
  Height = 10
  Placement = pos=(0,-50,-7) rot=(0,0,1;0rad)
  Radius = 5
FEATURE [Part::Cylinder] Cylinder240
  Angle = 360
  AttacherType = Attacher::AttachEngine3D
  Height = 10
  Placement = pos=(0,-50,-7) rot=(0,0,1;0rad)
  Radius = 5
FEATURE [Part::Cylinder] Cylinder241
  Angle = 360
  AttacherType = Attacher::AttachEngine3D
  Height = 10
  Placement = pos=(0,-50,-12) rot=(0,0,1;0rad)
  Radius = 3
FEATURE [Part::Sphere] Sphere047
  Angle1 = 0
  Angle2 = 90
  Angle3 = 360
  AttacherType = Attacher::AttachEngine3D
  Placement = pos=(0,-50,0) rot=(0,0,1;0rad)
  Radius = 5
FEATURE [Part::MultiCommon] Common039
  Shapes = -> [Cylinder240,Sphere047]
FEATURE [Part::MultiFuse] Fusion005077020014
  Shapes = -> [Common039,Cylinder237]
FEATURE [Part::Cut] Cut204006021
  Base = -> Fusion005077020014
  Tool = -> Box122
FEATURE [Part::Cut] Cut204006036
  Base = -> Cut204006021
  Tool = -> Box115
FEATURE [Part::Cut] Cut204006037
  Base = -> Cut204006036
  Tool = -> Box118
FEATURE [Part::Cut] Cut204006038
  Base = -> Cut204006037
  Tool = -> Cylinder241
FEATURE [Part::MultiFuse] Fusion005077020015
  Shapes = -> [Cut204006038,Cylinder233]
FEATURE [Part::Refine] Fusion005077020013
  Placement = pos=(0,50,-8.5) rot=(0,0,1;0rad)
  Source = -> Fusion005077020015
FEATURE [Part::Cut] Cut204006028
  Base = -> Fusion005077020013
  Placement = pos=(-77,0,-74) rot=(0,0,1;0rad)
  Tool = -> Cylinder236
FEATURE [Part::MultiFuse] Fusion005077020016
  Shapes = -> [Cut204006022,Cut204006026]
FEATURE [Part::MultiFuse] Fusion005077020018
  Shapes = -> [Fusion005077020016,Cut204006028]
FEATURE [Part::Refine] Fusion005077020017
  Source = -> Fusion005077020018
FEATURE [Part::Cylinder] Cylinder242
  Angle = 360
  AttacherType = Attacher::AttachEngine3D
  Height = 30
  Placement = pos=(-69,0,-136) rot=(0,0,1;0rad)
  Radius = 2
FEATURE [Part::Cylinder] Cylinder243
  Angle = 360
  AttacherType = Attacher::AttachEngine3D
  Height = 5
  Placement = pos=(-92.5,0,-89.5) rot=(0,0,1;0rad)
  Radius = 3
FEATURE [Part::Cylinder] Cylinder244
  Angle = 360
  AttacherType = Attacher::AttachEngine3D
  Height = 50
  Placement = pos=(-81,0,-143.5) rot=(0,0,1;0rad)
  Radius = 2
FEATURE [Part::Cylinder] Cylinder245
  Angle = 360
  AttacherType = Attacher::AttachEngine3D
  Height = 15
  Placement = pos=(-92,0,-91) rot=(0,1,0;1.5708rad)
  Radius = 2
FEATURE [Part::Cut] Cut204006040
  Base = -> Fusion005077020017
  Tool = -> Cylinder243
FEATURE [Part::Cylinder] Cylinder246
  Angle = 360
  AttacherType = Attacher::AttachEngine3D
  Height = 5
  Placement = pos=(-77,0,-89.5) rot=(0,0,1;0rad)
  Radius = 3
FEATURE [Part::Cut] Cut204006041
  Base = -> Cut204006040
  Tool = -> Cylinder246
FEATURE [Part::Cut] Cut204006039
  Base = -> Cut204006041
  Tool = -> Cylinder245
FEATURE [Part::Cut] Cut204006043
  Base = -> Cut204006039
  Tool = -> Cylinder244
FEATURE [Part::Cut] Cut204006042
  Base = -> Cut204006043
  Tool = -> Cylinder242
FEATURE [Part::Cut] Cut204006027
  Base = -> Cut204006042
  Placement = pos=(0,0,37) rot=(0,0,1;0rad)
  Tool = -> Cylinder228
FEATURE [Part::Cylinder] Cylinder247
  Angle = 360
  AttacherType = Attacher::AttachEngine3D
  Height = 43
  Placement = pos=(-93,0,-100.5) rot=(0,0,1;0rad)
  Radius = 3
FEATURE [Part::Cut] Cut204006044
  Base = -> Cut204006027
  Placement = pos=(132,0,0) rot=(0,0,1;0rad)
  Tool = -> Cylinder247
FEATURE [Part::Box] Box127  label="Cube127"
  AttacherType = Attacher::AttachEngine3D
  Height = 43
  Length = 12.5
  Placement = pos=(-168,-5,-90.5) rot=(0,0,1;0rad)
  Width = 10
FEATURE [Part::Cut] Cut204006045
  Base = -> Box116
  Placement = pos=(-101,0,0) rot=(0,0,1;0rad)
  Tool = -> Cut204006044
FEATURE [Part::Cut] Cut204006035
  Base = -> Cut204006045
  Tool = -> Box125
FEATURE [Part::Refine] Cut204006032
  Source = -> Cut204006035
FEATURE [Part::Cut] Cut204006034
  Base = -> Cut204006032
  Placement = pos=(-141.5,0,0) rot=(0,0,1;0rad)
  Tool = -> Cylinder229
FEATURE [Part::Cut] Cut204006033
  Base = -> Cut204006034
  Tool = -> Box111
FEATURE [Part::Cut] Cut204006031
  Base = -> Cut204006033
  Tool = -> Box127
FEATURE [Part::Cylinder] Cylinder248
  Angle = 360
  AttacherType = Attacher::AttachEngine3D
  Height = 10
  Placement = pos=(0,-50,-12) rot=(0,0,1;0rad)
  Radius = 3
FEATURE [Part::Box] Box128  label="Cube128"
  AttacherType = Attacher::AttachEngine3D
  Height = 24
  Length = 1.5
  Placement = pos=(-189.24,-5,-81.947) rot=(0,1,0;1.0472rad)
  Width = 10
FEATURE [Part::Box] Box129  label="Cube129"
  AttacherType = Attacher::AttachEngine3D
  Height = 25
  Length = 2
  Placement = pos=(-59,-5,-72) rot=(0,0,1;0rad)
  Width = 10
FEATURE [Part::Box] Box130  label="Cube130"
  AttacherType = Attacher::AttachEngine3D
  Height = 10
  Length = 2
  Placement = pos=(-1,-55,-2) rot=(0,0,1;0rad)
  Width = 10
FEATURE [Part::Cylinder] Cylinder249
  Angle = 360
  AttacherType = Attacher::AttachEngine3D
  Height = 22
  Placement = pos=(-64.5,0,-69.5) rot=(0,0,1;0rad)
  Radius = 3
FEATURE [Part::Cylinder] Cylinder250
  Angle = 360
  AttacherType = Attacher::AttachEngine3D
  Height = 4
  Placement = pos=(-2,-50,1) rot=(0,1,0;1.5708rad)
  Radius = 2
FEATURE [Part::Cylinder] Cylinder251
  Angle = 360
  AttacherType = Attacher::AttachEngine3D
  Height = 10
  Placement = pos=(0,-50,-10) rot=(0,0,1;0rad)
  Radius = 5
FEATURE [Part::Box] Box131  label="Cube131"
  AttacherType = Attacher::AttachEngine3D
  Height = 17
  Length = 12
  Placement = pos=(-167.14,-5,-90.45) rot=(0,-1,0;0.523599rad)
  Width = 10
FEATURE [Part::Cut] Cut204006048
  Base = -> Cut204006031
  Tool = -> Box131
FEATURE [Part::Cut] Cut204006049
  Base = -> Cut204006048
  Tool = -> Box114
FEATURE [Part::Cut] Cut204006053
  Base = -> Cut204006049
  Placement = pos=(111,0,0) rot=(0,0,1;0rad)
  Tool = -> Box128
FEATURE [Part::Cut] Cut204006054
  Base = -> Cut204006053
  Tool = -> Box126
FEATURE [Part::Cut] Cut204006050
  Base = -> Cut204006054
  Tool = -> Box129
FEATURE [Part::Box] Box132  label="Cube132"
  AttacherType = Attacher::AttachEngine3D
  Height = 10
  Length = 10
  Placement = pos=(-12,-55,-2) rot=(0,0,1;0rad)
  Width = 10
FEATURE [Part::Sphere] Sphere048
  Angle1 = 0
  Angle2 = 90
  Angle3 = 360
  AttacherType = Attacher::AttachEngine3D
  Placement = pos=(0,-50,0) rot=(0,0,1;0rad)
  Radius = 5
FEATURE [Part::MultiCommon] Common041
  Shapes = -> [Cylinder239,Sphere048]
FEATURE [Part::MultiFuse] Fusion005077020021
  Shapes = -> [Common041,Cylinder251]
FEATURE [Part::Cut] Cut204006052
  Base = -> Fusion005077020021
  Tool = -> Box121
FEATURE [Part::Cut] Cut204006046
  Base = -> Cut204006052
  Tool = -> Box130
FEATURE [Part::Cut] Cut204006051
  Base = -> Cut204006046
  Tool = -> Box132
FEATURE [Part::Cut] Cut204006047
  Base = -> Cut204006051
  Tool = -> Cylinder248
FEATURE [Part::MultiFuse] Fusion005077020020
  Shapes = -> [Cut204006047,Cylinder250]
FEATURE [Part::Refine] Fusion005077020019
  Placement = pos=(0,50,-8.5) rot=(0,0,1;0rad)
  Source = -> Fusion005077020020
FEATURE [Part::Cut] Cut204006055
  Base = -> Fusion005077020019
  Placement = pos=(-64.5,0,-37) rot=(0,0,1;0rad)
  Tool = -> Cylinder232
FEATURE [Part::MultiFuse] Fusion005077020022
  Shapes = -> [Cut204006050,Cut204006055]
FEATURE [Part::Cut] Cut204006056
  Base = -> Fusion005077020022
  Tool = -> Cylinder249
FEATURE [Part::Cylinder] Cylinder252
  Angle = 360
  AttacherType = Attacher::AttachEngine3D
  Height = 10
  Placement = pos=(-69.9365,0,-70.8157) rot=(0,1,0;0.523599rad)
  Radius = 2
FEATURE [Part::Cut] Cut204006057
  Base = -> Cut204006056
  Placement = pos=(145,0,0) rot=(0,0,1;0rad)
  Tool = -> Cylinder252
FEATURE [Part::Box] Box133  label="Cube133"
  AttacherType = Attacher::AttachEngine3D
  Height = 20
  Length = 10
  Placement = pos=(-168.492,-5,-108.103) rot=(0,-1,0;0.523599rad)
  Width = 10
FEATURE [Part::Box] Box134  label="Cube134"
  AttacherType = Attacher::AttachEngine3D
  Height = 17
  Length = 12
  Placement = pos=(-167.14,-5,-90.45) rot=(0,-1,0;0.523599rad)
  Width = 10
FEATURE [Part::Box] Box135  label="Cube135"
  AttacherType = Attacher::AttachEngine3D
  Height = 43
  Length = 12.5
  Placement = pos=(-168,-5,-90.5) rot=(0,0,1;0rad)
  Width = 10
FEATURE [Part::MultiFuse] Fusion005077020024
  Shapes = -> [Box135,Box134]
FEATURE [Part::Refine] Fusion005077020023
  Source = -> Fusion005077020024
FEATURE [Part::Cut] Cut204006058
  Base = -> Fusion005077020023
  Tool = -> Box133
FEATURE [Part::Refine] Cut204006059
  Placement = pos=(110,0,0) rot=(0,0,1;0rad)
  Source = -> Cut204006058
FEATURE [Part::Box] Box136  label="Cube136"
  AttacherType = Attacher::AttachEngine3D
  Height = 10
  Length = 2
  Placement = pos=(-1,-55,-2) rot=(0,0,1;0rad)
  Width = 10
FEATURE [Part::Cylinder] Cylinder253
  Angle = 360
  AttacherType = Attacher::AttachEngine3D
  Height = 4
  Placement = pos=(-2,-50,1) rot=(0,1,0;1.5708rad)
  Radius = 2
FEATURE [Part::Box] Box137  label="Cube137"
  AttacherType = Attacher::AttachEngine3D
  Height = 10
  Length = 10
  Placement = pos=(2,-55,-2) rot=(0,0,1;0rad)
  Width = 10
FEATURE [Part::Box] Box138  label="Cube138"
  AttacherType = Attacher::AttachEngine3D
  Height = 10
  Length = 10
  Placement = pos=(-12,-55,-2) rot=(0,0,1;0rad)
  Width = 10
FEATURE [Part::Cylinder] Cylinder254
  Angle = 360
  AttacherType = Attacher::AttachEngine3D
  Height = 10
  Placement = pos=(-5,0,-7) rot=(0,1,0;1.5708rad)
  Radius = 0.5
FEATURE [Part::Cylinder] Cylinder255
  Angle = 360
  AttacherType = Attacher::AttachEngine3D
  Height = 10
  Placement = pos=(0,-50,-7) rot=(0,0,1;0rad)
  Radius = 5
FEATURE [Part::Sphere] Sphere049
  Angle1 = 0
  Angle2 = 90
  Angle3 = 360
  AttacherType = Attacher::AttachEngine3D
  Placement = pos=(0,-50,0) rot=(0,0,1;0rad)
  Radius = 5
FEATURE [Part::MultiCommon] Common042
  Shapes = -> [Cylinder255,Sphere049]
FEATURE [Part::Cylinder] Cylinder256
  Angle = 360
  AttacherType = Attacher::AttachEngine3D
  Height = 10
  Placement = pos=(0,-50,-10) rot=(0,0,1;0rad)
  Radius = 5
FEATURE [Part::MultiFuse] Fusion005077020026
  Shapes = -> [Common042,Cylinder256]
FEATURE [Part::Cut] Cut204006061
  Base = -> Fusion005077020026
  Tool = -> Box137
FEATURE [Part::Cut] Cut204006063
  Base = -> Cut204006061
  Tool = -> Box136
FEATURE [Part::Cut] Cut204006064
  Base = -> Cut204006063
  Tool = -> Box138
FEATURE [Part::Cylinder] Cylinder257
  Angle = 360
  AttacherType = Attacher::AttachEngine3D
  Height = 10
  Placement = pos=(0,-50,-12) rot=(0,0,1;0rad)
  Radius = 3
FEATURE [Part::Cut] Cut204006060
  Base = -> Cut204006064
  Tool = -> Cylinder257
FEATURE [Part::MultiFuse] Fusion005077020025
  Shapes = -> [Cut204006060,Cylinder253]
FEATURE [Part::Refine] Fusion005077020027
  Placement = pos=(0,50,-8.5) rot=(0,0,1;0rad)
  Source = -> Fusion005077020025
FEATURE [Part::Cut] Cut204006062
  Base = -> Fusion005077020027
  Placement = pos=(-52,0,-37) rot=(0,0,1;0rad)
  Tool = -> Cylinder254
FEATURE [Part::Cylinder] Cylinder258
  Angle = 360
  AttacherType = Attacher::AttachEngine3D
  Height = 37
  Placement = pos=(-52,0,-84.5) rot=(0,0,1;0rad)
  Radius = 3
FEATURE [Part::MultiFuse] Fusion005077020028
  Shapes = -> [Cut204006059,Cut204006062]
FEATURE [Part::Cut] Cut204006065
  Base = -> Fusion005077020028
  Tool = -> Cylinder258
FEATURE [Part::Cylinder] Cylinder259
  Angle = 360
  AttacherType = Attacher::AttachEngine3D
  Height = 10
  Placement = pos=(-62.0416,0,-84.0208) rot=(0,1,0;0.785398rad)
  Radius = 2
FEATURE [Part::Cut] Cut204006066
  Base = -> Cut204006065
  Placement = pos=(153.5,0,0) rot=(0,0,1;0rad)
  Tool = -> Cylinder259
FEATURE [Part::Cylinder] Cylinder260
  Angle = 360
  AttacherType = Attacher::AttachEngine3D
  Height = 46
  Placement = pos=(-50.83,0,-93.18) rot=(0,1,0;5.75959rad)
  Radius = 2
FEATURE [Part::Cylinder] Cylinder261
  Angle = 360
  AttacherType = Attacher::AttachEngine3D
  Height = 46
  Placement = pos=(-50.83,0,-93.18) rot=(0,-1,0;0.523599rad)
  Radius = 2
FEATURE [Part::Cylinder] Cylinder262
  Angle = 360
  AttacherType = Attacher::AttachEngine3D
  Height = 46
  Placement = pos=(-50.83,0,-93.18) rot=(0,-1,0;0.523599rad)
  Radius = 1.85
FEATURE [Part::Cut] Cut204006067
  Base = -> Cut204006019
  Tool = -> Cylinder260
FEATURE [Part::Cut] Cut204006068
  Base = -> Cut204006017
  Tool = -> Cylinder261
FEATURE [Part::Box] Box139  label="Cube139"
  AttacherType = Attacher::AttachEngine3D
  Height = 23
  Length = 15
  Placement = pos=(-59.2,-11,-91.361) rot=(0,1,0;1.0472rad)
  Width = 21
FEATURE [Part::Cut] Cut204006069
  Base = -> Cut204006067
  Tool = -> Box139
FEATURE [TechDraw::DrawSVGTemplate] Template
  EditableTexts = Designed_by_Name=Designed by Name; Drawing_number=Drawing number; FC-Date=Date; FC-SC=Scale; FC-SH=Sheet; FC-Title=Title; Subtitle=Subtitle; Weight=Weight
  Height = 210
  Orientation = 1
  Width = 297
FEATURE [Part::Feature] Connect_solid  label="Connect (Solid)"
  shape: bbox 10 x 10 x 52 mm, 88 faces (baked)
FEATURE [Part::Refine] Connect005
  Source = -> Connect
FEATURE [Part::Refine] Connect001001
  Source = -> Connect001
FEATURE [Part::Refine] Connect002001
  Source = -> Connect002
FEATURE [Part::Refine] Connect003001
  Source = -> Connect003
FEATURE [Part::Refine] Connect004001
  Source = -> Connect004
FEATURE [Part::Refine] Cut204006069001
  Source = -> Cut204006069
FEATURE [Part::Refine] Cut204006068001
  Source = -> Cut204006068
FEATURE [TechDraw::DrawProjGroupItem] ProjItem  label="Front"
  CoarseView = false
  Direction = (0.044,-0.987,-0.152)
  Focus = 100
  HardHidden = false
  IsoCount = 0
  IsoHidden = false
  IsoVisible = false
  LockPosition = true
  Perspective = false
  Rotation = 0
  RotationVector = (0.999,0.043,0.008)
  ScaleType = 2
  SeamHidden = false
  SeamVisible = true
  SmoothHidden = false
  SmoothVisible = true
  Source = -> [Connect_solid]
  Type = 0
  X = 0
  XDirection = (0.999,0.043,0.008)
  Y = 0
FEATURE [TechDraw::DrawProjGroup] ProjGroup
  Anchor = -> ProjItem
  AutoDistribute = true
  LockPosition = false
  ProjectionType = 0
  Rotation = 0
  ScaleType = 0
  Source = -> [Connect_solid]
  Views = -> [ProjItem]
  X = 24.0309
  Y = 167.235
  spacingX = 15
  spacingY = 15
FEATURE [TechDraw::DrawViewDimension] Dimension
  Arbitrary = false
  ArbitraryTolerances = false
  EqualTolerance = true
  FormatSpec = %.2f
  FormatSpecOverTolerance = %+.2f
  FormatSpecUnderTolerance = %+.2f
  Inverted = false
  LockPosition = false
  MeasureType = 1
  OverTolerance = 0
  References2D = -> [ProjItem]
  Rotation = 0
  ScaleType = 0
  TheoreticalExact = false
  Type = 2
  UnderTolerance = 0
  X = 20.8254
  Y = 18.4632
FEATURE [TechDraw::DrawViewDimension] Dimension001
  Arbitrary = false
  ArbitraryTolerances = false
  EqualTolerance = true
  FormatSpec = %.2f
  FormatSpecOverTolerance = %+.2f
  FormatSpecUnderTolerance = %+.2f
  Inverted = false
  LockPosition = false
  MeasureType = 1
  OverTolerance = 0
  References2D = -> [ProjItem]
  Rotation = 0
  ScaleType = 0
  TheoreticalExact = false
  Type = 2
  UnderTolerance = 0
  X = 13.8537
  Y = 6.31081
FEATURE [TechDraw::DrawViewDimension] Dimension002
  Arbitrary = false
  ArbitraryTolerances = false
  EqualTolerance = true
  FormatSpec = %.2f
  FormatSpecOverTolerance = %+.2f
  FormatSpecUnderTolerance = %+.2f
  Inverted = false
  LockPosition = false
  MeasureType = 1
  OverTolerance = 0
  References2D = -> [ProjItem]
  Rotation = 0
  ScaleType = 0
  TheoreticalExact = false
  Type = 2
  UnderTolerance = 0
  X = 20.9261
  Y = -0.604638
FEATURE [TechDraw::DrawViewDimension] Dimension003
  Arbitrary = false
  ArbitraryTolerances = false
  EqualTolerance = true
  FormatSpec = %.2f
  FormatSpecOverTolerance = %+.2f
  FormatSpecUnderTolerance = %+.2f
  Inverted = false
  LockPosition = false
  MeasureType = 1
  OverTolerance = 0
  References2D = -> [ProjItem]
  Rotation = 0
  ScaleType = 0
  TheoreticalExact = false
  Type = 2
  UnderTolerance = 0
  X = 14.0355
  Y = -9.9627
FEATURE [TechDraw::DrawViewDimension] Dimension004
  Arbitrary = false
  ArbitraryTolerances = false
  EqualTolerance = true
  FormatSpec = %.2f
  FormatSpecOverTolerance = %+.2f
  FormatSpecUnderTolerance = %+.2f
  Inverted = false
  LockPosition = false
  MeasureType = 1
  OverTolerance = 0
  References2D = -> [ProjItem]
  Rotation = 0
  ScaleType = 0
  TheoreticalExact = false
  Type = 2
  UnderTolerance = 0
  X = 21.0447
  Y = -18.8889
FEATURE [TechDraw::DrawProjGroupItem] ProjItem001  label="Front001"
  CoarseView = false
  Direction = (0.018,-1,0)
  Focus = 100
  HardHidden = false
  IsoCount = 0
  IsoHidden = false
  IsoVisible = false
  LockPosition = true
  Perspective = false
  Rotation = 0
  RotationVector = (-0.988,-0.018,-0.004)
  ScaleType = 2
  SeamHidden = false
  SeamVisible = true
  SmoothHidden = false
  SmoothVisible = true
  Source = -> [Connect004001]
  Type = 0
  X = 0
  XDirection = (0.988008,0.0175681,0.004)
  Y = 0
FEATURE [TechDraw::DrawProjGroup] ProjGroup001
  Anchor = -> ProjItem001
  AutoDistribute = true
  LockPosition = false
  ProjectionType = 0
  Rotation = 0
  ScaleType = 0
  Source = -> [Connect004001]
  Views = -> [ProjItem001]
  X = 53.2556
  Y = 50.7772
  spacingX = 15
  spacingY = 15
FEATURE [TechDraw::DrawViewDimension] Dimension005
  Arbitrary = false
  ArbitraryTolerances = false
  EqualTolerance = true
  FormatSpec = %.2f
  FormatSpecOverTolerance = %+.2f
  FormatSpecUnderTolerance = %+.2f
  Inverted = false
  LockPosition = false
  MeasureType = 1
  OverTolerance = 0
  References2D = -> [ProjItem001]
  Rotation = 0
  ScaleType = 0
  TheoreticalExact = false
  Type = 0
  UnderTolerance = 0
  X = 2.31225
  Y = 31.0699
FEATURE [TechDraw::DrawViewDimension] Dimension006
  Arbitrary = false
  ArbitraryTolerances = false
  EqualTolerance = true
  FormatSpec = %.2f
  FormatSpecOverTolerance = %+.2f
  FormatSpecUnderTolerance = %+.2f
  Inverted = false
  LockPosition = false
  MeasureType = 1
  OverTolerance = 0
  References2D = -> [ProjItem001]
  Rotation = 0
  ScaleType = 0
  TheoreticalExact = false
  Type = 0
  UnderTolerance = 0
  X = 2.42458
  Y = 20.6461
FEATURE [TechDraw::DrawViewDimension] Dimension007
  Arbitrary = false
  ArbitraryTolerances = false
  EqualTolerance = true
  FormatSpec = %.2f
  FormatSpecOverTolerance = %+.2f
  FormatSpecUnderTolerance = %+.2f
  Inverted = false
  LockPosition = false
  MeasureType = 1
  OverTolerance = 0
  References2D = -> [ProjItem001]
  Rotation = 0
  ScaleType = 0
  TheoreticalExact = false
  Type = 0
  UnderTolerance = 0
  X = 13.9327
  Y = 20.451
FEATURE [TechDraw::DrawViewDimension] Dimension008
  Arbitrary = false
  ArbitraryTolerances = false
  EqualTolerance = true
  FormatSpec = %.2f
  FormatSpecOverTolerance = %+.2f
  FormatSpecUnderTolerance = %+.2f
  Inverted = false
  LockPosition = false
  MeasureType = 1
  OverTolerance = 0
  References2D = -> [ProjItem001]
  Rotation = 0
  ScaleType = 0
  TheoreticalExact = false
  Type = 0
  UnderTolerance = 0
  X = 15.7282
  Y = 6.95713
FEATURE [TechDraw::DrawViewDimension] Dimension009
  Arbitrary = false
  ArbitraryTolerances = false
  EqualTolerance = true
  FormatSpec = %.2f
  FormatSpecOverTolerance = %+.2f
  FormatSpecUnderTolerance = %+.2f
  Inverted = false
  LockPosition = false
  MeasureType = 1
  OverTolerance = 0
  References2D = -> [ProjItem001]
  Rotation = 0
  ScaleType = 0
  TheoreticalExact = false
  Type = 2
  UnderTolerance = 0
  X = 30.4489
  Y = -11.6365
FEATURE [TechDraw::DrawViewDimension] Dimension010
  Arbitrary = false
  ArbitraryTolerances = false
  EqualTolerance = true
  FormatSpec = %.2f
  FormatSpecOverTolerance = %+.2f
  FormatSpecUnderTolerance = %+.2f
  Inverted = false
  LockPosition = false
  MeasureType = 1
  OverTolerance = 0
  References2D = -> [ProjItem001]
  Rotation = 0
  ScaleType = 0
  TheoreticalExact = false
  Type = 2
  UnderTolerance = 0
  X = 31.1045
  Y = 3.76854
FEATURE [TechDraw::DrawViewDimension] Dimension011
  Arbitrary = false
  ArbitraryTolerances = false
  EqualTolerance = true
  FormatSpec = %.2f
  FormatSpecOverTolerance = %+.2f
  FormatSpecUnderTolerance = %+.2f
  Inverted = false
  LockPosition = false
  MeasureType = 1
  OverTolerance = 0
  References2D = -> [ProjItem001]
  Rotation = 0
  ScaleType = 0
  TheoreticalExact = false
  Type = 2
  UnderTolerance = 0
  X = 30.7583
  Y = -26.2662
FEATURE [TechDraw::DrawViewDimension] Dimension012
  Arbitrary = false
  ArbitraryTolerances = false
  EqualTolerance = true
  FormatSpec = %.2f
  FormatSpecOverTolerance = %+.2f
  FormatSpecUnderTolerance = %+.2f
  Inverted = false
  LockPosition = false
  MeasureType = 1
  OverTolerance = 0
  References2D = -> [ProjItem001]
  Rotation = 0
  ScaleType = 0
  TheoreticalExact = false
  Type = 1
  UnderTolerance = 0
  X = 17.5323
  Y = -28.5795
FEATURE [TechDraw::DrawViewDimension] Dimension013
  Arbitrary = false
  ArbitraryTolerances = false
  EqualTolerance = true
  FormatSpec = %.2f
  FormatSpecOverTolerance = %+.2f
  FormatSpecUnderTolerance = %+.2f
  Inverted = false
  LockPosition = false
  MeasureType = 1
  OverTolerance = 0
  References2D = -> [ProjItem001]
  Rotation = 0
  ScaleType = 0
  TheoreticalExact = false
  Type = 0
  UnderTolerance = 0
  X = 4.77159
  Y = -22.6593
FEATURE [TechDraw::DrawViewDimension] Dimension014
  Arbitrary = false
  ArbitraryTolerances = false
  EqualTolerance = true
  FormatSpec = %.2f
  FormatSpecOverTolerance = %+.2f
  FormatSpecUnderTolerance = %+.2f
  Inverted = false
  LockPosition = false
  MeasureType = 1
  OverTolerance = 0
  References2D = -> [ProjItem001]
  Rotation = 0
  ScaleType = 0
  TheoreticalExact = false
  Type = 2
  UnderTolerance = 0
  X = -19.1735
  Y = -19.6034
FEATURE [TechDraw::DrawViewDimension] Dimension015
  Arbitrary = false
  ArbitraryTolerances = false
  EqualTolerance = true
  FormatSpec = %.2f
  FormatSpecOverTolerance = %+.2f
  FormatSpecUnderTolerance = %+.2f
  Inverted = false
  LockPosition = false
  MeasureType = 1
  OverTolerance = 0
  References2D = -> [ProjItem001]
  Rotation = 0
  ScaleType = 0
  TheoreticalExact = false
  Type = 0
  UnderTolerance = 0
  X = -29.9783
  Y = 30.8618
FEATURE [TechDraw::DrawProjGroupItem] ProjItem002  label="Front002"
  CoarseView = false
  Direction = (0.0013606,0.152267,-0.988338)
  Focus = 100
  HardHidden = false
  IsoCount = 0
  IsoHidden = false
  IsoVisible = false
  LockPosition = true
  Perspective = false
  Rotation = 0
  RotationVector = (0.999,0.043,0.008)
  ScaleType = 2
  SeamHidden = false
  SeamVisible = true
  SmoothHidden = false
  SmoothVisible = true
  Source = -> [Connect005]
  Type = 0
  X = 0
  XDirection = (-0.99903,-0.0432972,-0.00804583)
  Y = 0
FEATURE [TechDraw::DrawProjGroup] ProjGroup002
  Anchor = -> ProjItem002
  AutoDistribute = true
  LockPosition = false
  ProjectionType = 0
  Rotation = 0
  ScaleType = 0
  Source = -> [Connect005]
  Views = -> [ProjItem002]
  X = 44.4002
  Y = 108.888
  spacingX = 15
  spacingY = 15
FEATURE [TechDraw::DrawProjGroupItem] ProjItem003  label="Front003"
  CoarseView = false
  Direction = (-0.99903,-0.0432972,-0.00804583)
  Focus = 100
  HardHidden = false
  IsoCount = 0
  IsoHidden = false
  IsoVisible = false
  LockPosition = true
  Perspective = false
  Rotation = 0
  RotationVector = (0.999,0.043,0.008)
  ScaleType = 2
  SeamHidden = false
  SeamVisible = true
  SmoothHidden = false
  SmoothVisible = true
  Source = -> [Connect_solid]
  Type = 0
  X = 0
  XDirection = (0.0440174,-0.987391,-0.15206)
  Y = 0
FEATURE [TechDraw::DrawProjGroup] ProjGroup003
  Anchor = -> ProjItem003
  AutoDistribute = true
  LockPosition = false
  ProjectionType = 0
  Rotation = 0
  ScaleType = 0
  Source = -> [Connect_solid]
  Views = -> [ProjItem003]
  X = 71.0119
  Y = 162.866
  spacingX = 15
  spacingY = 15
FEATURE [TechDraw::DrawViewDimension] Dimension016
  Arbitrary = false
  ArbitraryTolerances = false
  EqualTolerance = true
  FormatSpec = %.2f
  FormatSpecOverTolerance = %+.2f
  FormatSpecUnderTolerance = %+.2f
  Inverted = false
  LockPosition = false
  MeasureType = 1
  OverTolerance = 0
  References2D = -> [ProjItem003]
  Rotation = 0
  ScaleType = 0
  TheoreticalExact = false
  Type = 0
  UnderTolerance = 0
  X = 18.774
  Y = 23.0347
FEATURE [TechDraw::DrawViewDimension] Dimension017
  Arbitrary = false
  ArbitraryTolerances = false
  EqualTolerance = true
  FormatSpec = %.2f
  FormatSpecOverTolerance = %+.2f
  FormatSpecUnderTolerance = %+.2f
  Inverted = false
  LockPosition = false
  MeasureType = 1
  OverTolerance = 0
  References2D = -> [ProjItem003]
  Rotation = 0
  ScaleType = 0
  TheoreticalExact = false
  Type = 0
  UnderTolerance = 0
  X = 22.1163
  Y = 2.28609
FEATURE [TechDraw::DrawViewDimension] Dimension018
  Arbitrary = false
  ArbitraryTolerances = false
  EqualTolerance = true
  FormatSpec = %.2f
  FormatSpecOverTolerance = %+.2f
  FormatSpecUnderTolerance = %+.2f
  Inverted = false
  LockPosition = false
  MeasureType = 1
  OverTolerance = 0
  References2D = -> [ProjItem002]
  Rotation = 0
  ScaleType = 0
  TheoreticalExact = false
  Type = 0
  UnderTolerance = 0
  X = -10.757
  Y = 5.55514
FEATURE [TechDraw::DrawViewDimension] Dimension019
  Arbitrary = false
  ArbitraryTolerances = false
  EqualTolerance = true
  FormatSpec = %.2f
  FormatSpecOverTolerance = %+.2f
  FormatSpecUnderTolerance = %+.2f
  Inverted = false
  LockPosition = false
  MeasureType = 1
  OverTolerance = 0
  References2D = -> [ProjItem002]
  Rotation = 0
  ScaleType = 0
  TheoreticalExact = false
  Type = 1
  UnderTolerance = 0
  X = -0.29522
  Y = 18.2353
FEATURE [TechDraw::DrawViewDimension] Dimension020
  Arbitrary = false
  ArbitraryTolerances = false
  EqualTolerance = true
  FormatSpec = %.2f
  FormatSpecOverTolerance = %+.2f
  FormatSpecUnderTolerance = %+.2f
  Inverted = false
  LockPosition = false
  MeasureType = 1
  OverTolerance = 0
  References2D = -> [ProjItem002]
  Rotation = 0
  ScaleType = 0
  TheoreticalExact = false
  Type = 1
  UnderTolerance = 0
  X = 7.13904
  Y = -7.53032
FEATURE [TechDraw::DrawProjGroupItem] ProjItem004  label="Front004"
  CoarseView = false
  Direction = (0.99983,0.0179969,0.00404788)
  Focus = 100
  HardHidden = false
  IsoCount = 0
  IsoHidden = false
  IsoVisible = false
  LockPosition = true
  Perspective = false
  Rotation = 0
  RotationVector = (-0.988,-0.018,-0.004)
  ScaleType = 2
  SeamHidden = false
  SeamVisible = true
  SmoothHidden = false
  SmoothVisible = true
  Source = -> [Connect004001]
  Type = 0
  X = 0
  XDirection = (-0.0179971,0.999838,0)
  Y = 0
FEATURE [TechDraw::DrawProjGroup] ProjGroup004
  Anchor = -> ProjItem004
  AutoDistribute = true
  LockPosition = false
  ProjectionType = 0
  Rotation = 0
  ScaleType = 0
  Source = -> [Connect004001]
  Views = -> [ProjItem004]
  X = 109.977
  Y = 59.0292
  spacingX = 15
  spacingY = 15
FEATURE [TechDraw::DrawViewDimension] Dimension021
  Arbitrary = false
  ArbitraryTolerances = false
  EqualTolerance = true
  FormatSpec = %.2f
  FormatSpecOverTolerance = %+.2f
  FormatSpecUnderTolerance = %+.2f
  Inverted = false
  LockPosition = false
  MeasureType = 1
  OverTolerance = 0
  References2D = -> [ProjItem004]
  Rotation = 0
  ScaleType = 0
  TheoreticalExact = false
  Type = 1
  UnderTolerance = 0
  X = 3.45805
  Y = -26.0606
FEATURE [TechDraw::DrawViewDimension] Dimension022
  Arbitrary = false
  ArbitraryTolerances = false
  EqualTolerance = true
  FormatSpec = %.2f
  FormatSpecOverTolerance = %+.2f
  FormatSpecUnderTolerance = %+.2f
  Inverted = false
  LockPosition = false
  MeasureType = 1
  OverTolerance = 0
  References2D = -> [ProjItem004]
  Rotation = 0
  ScaleType = 0
  TheoreticalExact = false
  Type = 1
  UnderTolerance = 0
  X = 0.085692
  Y = -35.5265
FEATURE [TechDraw::DrawViewDimension] Dimension023
  Arbitrary = false
  ArbitraryTolerances = false
  EqualTolerance = true
  FormatSpec = %.2f
  FormatSpecOverTolerance = %+.2f
  FormatSpecUnderTolerance = %+.2f
  Inverted = false
  LockPosition = false
  MeasureType = 1
  OverTolerance = 0
  References2D = -> [ProjItem004]
  Rotation = 0
  ScaleType = 0
  TheoreticalExact = false
  Type = 2
  UnderTolerance = 0
  X = 22.1867
  Y = -11.1602
FEATURE [TechDraw::DrawViewDimension] Dimension024
  Arbitrary = false
  ArbitraryTolerances = false
  EqualTolerance = true
  FormatSpec = %.2f
  FormatSpecOverTolerance = %+.2f
  FormatSpecUnderTolerance = %+.2f
  Inverted = false
  LockPosition = false
  MeasureType = 1
  OverTolerance = 0
  References2D = -> [ProjItem004]
  Rotation = 0
  ScaleType = 0
  TheoreticalExact = false
  Type = 2
  UnderTolerance = 0
  X = -13.283
  Y = -17.3119
FEATURE [TechDraw::DrawViewDimension] Dimension025
  Arbitrary = false
  ArbitraryTolerances = false
  EqualTolerance = true
  FormatSpec = %.2f
  FormatSpecOverTolerance = %+.2f
  FormatSpecUnderTolerance = %+.2f
  Inverted = false
  LockPosition = false
  MeasureType = 1
  OverTolerance = 0
  References2D = -> [ProjItem004]
  Rotation = 0
  ScaleType = 0
  TheoreticalExact = false
  Type = 2
  UnderTolerance = 0
  X = 10.5182
  Y = 3.8399
FEATURE [TechDraw::DrawViewDimension] Dimension026
  Arbitrary = false
  ArbitraryTolerances = false
  EqualTolerance = true
  FormatSpec = %.2f
  FormatSpecOverTolerance = %+.2f
  FormatSpecUnderTolerance = %+.2f
  Inverted = false
  LockPosition = false
  MeasureType = 1
  OverTolerance = 0
  References2D = -> [ProjItem004]
  Rotation = 0
  ScaleType = 0
  TheoreticalExact = false
  Type = 2
  UnderTolerance = 0
  X = -10.2952
  Y = -0.331316
FEATURE [TechDraw::DrawViewDimension] Dimension027
  Arbitrary = false
  ArbitraryTolerances = false
  EqualTolerance = true
  FormatSpec = %.2f
  FormatSpecOverTolerance = %+.2f
  FormatSpecUnderTolerance = %+.2f
  Inverted = false
  LockPosition = false
  MeasureType = 1
  OverTolerance = 0
  References2D = -> [ProjItem004]
  Rotation = 0
  ScaleType = 0
  TheoreticalExact = false
  Type = 2
  UnderTolerance = 0
  X = 15.9751
  Y = -26.1602
FEATURE [TechDraw::DrawProjGroupItem] ProjItem005  label="Front005"
  CoarseView = false
  Direction = (0.044,-0.987,-0.152)
  Focus = 100
  HardHidden = false
  IsoCount = 0
  IsoHidden = false
  IsoVisible = false
  LockPosition = true
  Perspective = false
  Rotation = 0
  RotationVector = (0.999,0.043,0.008)
  ScaleType = 2
  SeamHidden = false
  SeamVisible = true
  SmoothHidden = false
  SmoothVisible = true
  Source = -> [Cut204006069001]
  Type = 0
  X = 0
  XDirection = (0.999,0.043,0.008)
  Y = 0
FEATURE [TechDraw::DrawProjGroup] ProjGroup005
  Anchor = -> ProjItem005
  AutoDistribute = true
  LockPosition = false
  ProjectionType = 0
  Rotation = 0
  ScaleType = 0
  Source = -> [Cut204006069001]
  Views = -> [ProjItem005]
  X = 262.519
  Y = 150.128
  spacingX = 15
  spacingY = 15
FEATURE [TechDraw::DrawProjGroupItem] ProjItem006  label="Front006"
  CoarseView = false
  Direction = (0.99903,0.0432972,0.00804583)
  Focus = 100
  HardHidden = false
  IsoCount = 0
  IsoHidden = false
  IsoVisible = false
  LockPosition = true
  Perspective = false
  Rotation = 0
  RotationVector = (0.999,0.043,0.008)
  ScaleType = 2
  SeamHidden = false
  SeamVisible = true
  SmoothHidden = false
  SmoothVisible = true
  Source = -> [Cut204006069001]
  Type = 0
  X = 0
  XDirection = (-0.0440174,0.987391,0.15206)
  Y = 0
FEATURE [TechDraw::DrawProjGroup] ProjGroup006
  Anchor = -> ProjItem006
  AutoDistribute = true
  LockPosition = false
  ProjectionType = 0
  Rotation = 0
  ScaleType = 0
  Source = -> [Cut204006069001]
  Views = -> [ProjItem006]
  X = 225.584
  Y = 95.5532
  spacingX = 15
  spacingY = 15
FEATURE [TechDraw::DrawViewDimension] Dimension028
  Arbitrary = false
  ArbitraryTolerances = false
  EqualTolerance = true
  FormatSpec = %.2f
  FormatSpecOverTolerance = %+.2f
  FormatSpecUnderTolerance = %+.2f
  Inverted = false
  LockPosition = false
  MeasureType = 1
  OverTolerance = 0
  References2D = -> [ProjItem005]
  Rotation = 0
  ScaleType = 0
  TheoreticalExact = false
  Type = 0
  UnderTolerance = 0
  X = 12.0876
  Y = -31.3792
FEATURE [TechDraw::DrawViewDimension] Dimension029
  Arbitrary = false
  ArbitraryTolerances = false
  EqualTolerance = true
  FormatSpec = %.2f
  FormatSpecOverTolerance = %+.2f
  FormatSpecUnderTolerance = %+.2f
  Inverted = false
  LockPosition = false
  MeasureType = 1
  OverTolerance = 0
  References2D = -> [ProjItem005]
  Rotation = 0
  ScaleType = 0
  TheoreticalExact = false
  Type = 2
  UnderTolerance = 0
  X = 16.2361
  Y = 3.18704
FEATURE [TechDraw::DrawViewDimension] Dimension030
  Arbitrary = false
  ArbitraryTolerances = false
  EqualTolerance = true
  FormatSpec = %.2f
  FormatSpecOverTolerance = %+.2f
  FormatSpecUnderTolerance = %+.2f
  Inverted = false
  LockPosition = false
  MeasureType = 1
  OverTolerance = 0
  References2D = -> [ProjItem005]
  Rotation = 0
  ScaleType = 0
  TheoreticalExact = false
  Type = 2
  UnderTolerance = 0
  X = -11.6121
  Y = 10.7233
FEATURE [TechDraw::DrawViewDimension] Dimension031
  Arbitrary = false
  ArbitraryTolerances = false
  EqualTolerance = true
  FormatSpec = %.2f
  FormatSpecOverTolerance = %+.2f
  FormatSpecUnderTolerance = %+.2f
  Inverted = false
  LockPosition = false
  MeasureType = 1
  OverTolerance = 0
  References2D = -> [ProjItem005]
  Rotation = 0
  ScaleType = 0
  TheoreticalExact = false
  Type = 0
  UnderTolerance = 0
  X = -21.8653
  Y = -1.88949
FEATURE [TechDraw::DrawViewDimension] Dimension032
  Arbitrary = false
  ArbitraryTolerances = false
  EqualTolerance = true
  FormatSpec = %.2f
  FormatSpecOverTolerance = %+.2f
  FormatSpecUnderTolerance = %+.2f
  Inverted = false
  LockPosition = false
  MeasureType = 1
  OverTolerance = 0
  References2D = -> [ProjItem005]
  Rotation = 0
  ScaleType = 0
  TheoreticalExact = false
  Type = 0
  UnderTolerance = 0
  X = -10.2288
  Y = -14.9214
FEATURE [TechDraw::DrawViewDimension] Dimension033
  Arbitrary = false
  ArbitraryTolerances = false
  EqualTolerance = true
  FormatSpec = %.2f
  FormatSpecOverTolerance = %+.2f
  FormatSpecUnderTolerance = %+.2f
  Inverted = false
  LockPosition = false
  MeasureType = 1
  OverTolerance = 0
  References2D = -> [ProjItem005]
  Rotation = 0
  ScaleType = 0
  TheoreticalExact = false
  Type = 1
  UnderTolerance = 0
  X = 4.0793
  Y = 48.7491
FEATURE [TechDraw::DrawViewDimension] Dimension034
  Arbitrary = false
  ArbitraryTolerances = false
  EqualTolerance = true
  FormatSpec = %.2f
  FormatSpecOverTolerance = %+.2f
  FormatSpecUnderTolerance = %+.2f
  Inverted = false
  LockPosition = false
  MeasureType = 1
  OverTolerance = 0
  References2D = -> [ProjItem005]
  Rotation = 0
  ScaleType = 0
  TheoreticalExact = false
  Type = 1
  UnderTolerance = 0
  X = -7.37026
  Y = 43.8386
FEATURE [TechDraw::DrawViewDimension] Dimension035
  Arbitrary = false
  ArbitraryTolerances = false
  EqualTolerance = true
  FormatSpec = %.2f
  FormatSpecOverTolerance = %+.2f
  FormatSpecUnderTolerance = %+.2f
  Inverted = false
  LockPosition = false
  MeasureType = 1
  OverTolerance = 0
  References2D = -> [ProjItem005]
  Rotation = 0
  ScaleType = 0
  TheoreticalExact = false
  Type = 1
  UnderTolerance = 0
  X = 13.0311
  Y = 33.1323
FEATURE [TechDraw::DrawViewDimension] Dimension036
  Arbitrary = false
  ArbitraryTolerances = false
  EqualTolerance = true
  FormatSpec = %.2f
  FormatSpecOverTolerance = %+.2f
  FormatSpecUnderTolerance = %+.2f
  Inverted = false
  LockPosition = false
  MeasureType = 1
  OverTolerance = 0
  References2D = -> [ProjItem005]
  Rotation = 0
  ScaleType = 0
  TheoreticalExact = false
  Type = 2
  UnderTolerance = 0
  X = -7.84438
  Y = 26.5478
FEATURE [TechDraw::DrawViewDimension] Dimension037
  Arbitrary = false
  ArbitraryTolerances = false
  EqualTolerance = true
  FormatSpec = %.2f
  FormatSpecOverTolerance = %+.2f
  FormatSpecUnderTolerance = %+.2f
  Inverted = false
  LockPosition = false
  MeasureType = 1
  OverTolerance = 0
  References2D = -> [ProjItem006]
  Rotation = 0
  ScaleType = 0
  TheoreticalExact = false
  Type = 0
  UnderTolerance = 0
  X = 13.0622
  Y = 28.233
FEATURE [TechDraw::DrawViewDimension] Dimension038
  Arbitrary = false
  ArbitraryTolerances = false
  EqualTolerance = true
  FormatSpec = %.2f
  FormatSpecOverTolerance = %+.2f
  FormatSpecUnderTolerance = %+.2f
  Inverted = false
  LockPosition = false
  MeasureType = 1
  OverTolerance = 0
  References2D = -> [ProjItem006]
  Rotation = 0
  ScaleType = 0
  TheoreticalExact = false
  Type = 0
  UnderTolerance = 0
  X = -3.29869
  Y = 33.8892
FEATURE [TechDraw::DrawViewDimension] Dimension039
  Arbitrary = false
  ArbitraryTolerances = false
  EqualTolerance = true
  FormatSpec = %.2f
  FormatSpecOverTolerance = %+.2f
  FormatSpecUnderTolerance = %+.2f
  Inverted = false
  LockPosition = false
  MeasureType = 1
  OverTolerance = 0
  References2D = -> [ProjItem006]
  Rotation = 0
  ScaleType = 0
  TheoreticalExact = false
  Type = 0
  UnderTolerance = 0
  X = -4.60411
  Y = -25.8478
FEATURE [TechDraw::DrawViewDimension] Dimension040
  Arbitrary = false
  ArbitraryTolerances = false
  EqualTolerance = true
  FormatSpec = %.2f
  FormatSpecOverTolerance = %+.2f
  FormatSpecUnderTolerance = %+.2f
  Inverted = false
  LockPosition = false
  MeasureType = 1
  OverTolerance = 0
  References2D = -> [ProjItem006]
  Rotation = 0
  ScaleType = 0
  TheoreticalExact = false
  Type = 0
  UnderTolerance = 0
  X = 15.8861
  Y = 1.16854
FEATURE [TechDraw::DrawViewDimension] Dimension041
  Arbitrary = false
  ArbitraryTolerances = false
  EqualTolerance = true
  FormatSpec = %.2f
  FormatSpecOverTolerance = %+.2f
  FormatSpecUnderTolerance = %+.2f
  Inverted = false
  LockPosition = false
  MeasureType = 1
  OverTolerance = 0
  References2D = -> [ProjItem006]
  Rotation = 0
  ScaleType = 0
  TheoreticalExact = false
  Type = 0
  UnderTolerance = 0
  X = 9.15409
  Y = 0.563739
FEATURE [TechDraw::DrawViewDimension] Dimension042
  Arbitrary = false
  ArbitraryTolerances = false
  EqualTolerance = true
  FormatSpec = %.2f
  FormatSpecOverTolerance = %+.2f
  FormatSpecUnderTolerance = %+.2f
  Inverted = false
  LockPosition = false
  MeasureType = 1
  OverTolerance = 0
  References2D = -> [ProjItem006]
  Rotation = 0
  ScaleType = 0
  TheoreticalExact = false
  Type = 0
  UnderTolerance = 0
  X = 24.333
  Y = -17.0843
FEATURE [TechDraw::DrawViewDimension] Dimension043
  Arbitrary = false
  ArbitraryTolerances = false
  EqualTolerance = true
  FormatSpec = %.2f
  FormatSpecOverTolerance = %+.2f
  FormatSpecUnderTolerance = %+.2f
  Inverted = false
  LockPosition = false
  MeasureType = 1
  OverTolerance = 0
  References2D = -> [ProjItem006]
  Rotation = 0
  ScaleType = 0
  TheoreticalExact = false
  Type = 0
  UnderTolerance = 0
  X = 27.1264
  Y = 4.12978
FEATURE [TechDraw::DrawProjGroupItem] ProjItem007  label="Front007"
  CoarseView = false
  Direction = (0.044,-0.987,-0.152)
  Focus = 100
  HardHidden = false
  IsoCount = 0
  IsoHidden = false
  IsoVisible = false
  LockPosition = true
  Perspective = false
  Rotation = 0
  RotationVector = (0.999,0.043,0.008)
  ScaleType = 2
  SeamHidden = false
  SeamVisible = true
  SmoothHidden = false
  SmoothVisible = true
  Source = -> [Cut204006068001]
  Type = 0
  X = 0
  XDirection = (0.999,0.043,0.008)
  Y = 0
FEATURE [TechDraw::DrawProjGroup] ProjGroup007
  Anchor = -> ProjItem007
  AutoDistribute = true
  LockPosition = false
  ProjectionType = 0
  Rotation = 0
  ScaleType = 0
  Source = -> [Cut204006068001]
  Views = -> [ProjItem007]
  X = 179.651
  Y = 96.3311
  spacingX = 15
  spacingY = 15
FEATURE [TechDraw::DrawProjGroupItem] ProjItem008  label="Front008"
  CoarseView = false
  Direction = (-0.99903,-0.0432972,-0.00804583)
  Focus = 100
  HardHidden = false
  IsoCount = 0
  IsoHidden = false
  IsoVisible = false
  LockPosition = true
  Perspective = false
  Rotation = 0
  RotationVector = (0.999,0.043,0.008)
  ScaleType = 2
  SeamHidden = false
  SeamVisible = true
  SmoothHidden = false
  SmoothVisible = true
  Source = -> [Cut204006068001]
  Type = 0
  X = 0
  XDirection = (0.0440174,-0.987391,-0.15206)
  Y = 0
FEATURE [TechDraw::DrawProjGroup] ProjGroup008
  Anchor = -> ProjItem008
  AutoDistribute = true
  LockPosition = false
  ProjectionType = 0
  Rotation = 0
  ScaleType = 0
  Source = -> [Cut204006068001]
  Views = -> [ProjItem008]
  X = 206.403
  Y = 169.223
  spacingX = 15
  spacingY = 15
FEATURE [TechDraw::DrawViewDimension] Dimension044
  Arbitrary = false
  ArbitraryTolerances = false
  EqualTolerance = true
  FormatSpec = %.2f
  FormatSpecOverTolerance = %+.2f
  FormatSpecUnderTolerance = %+.2f
  Inverted = false
  LockPosition = false
  MeasureType = 1
  OverTolerance = 0
  References2D = -> [ProjItem007]
  Rotation = 0
  ScaleType = 0
  TheoreticalExact = false
  Type = 2
  UnderTolerance = 0
  X = 14.7969
  Y = -0.394092
FEATURE [TechDraw::DrawViewDimension] Dimension045
  Arbitrary = false
  ArbitraryTolerances = false
  EqualTolerance = true
  FormatSpec = %.2f
  FormatSpecOverTolerance = %+.2f
  FormatSpecUnderTolerance = %+.2f
  Inverted = false
  LockPosition = false
  MeasureType = 1
  OverTolerance = 0
  References2D = -> [ProjItem007]
  Rotation = 0
  ScaleType = 0
  TheoreticalExact = false
  Type = 0
  UnderTolerance = 0
  X = 18.6402
  Y = -15.42
FEATURE [TechDraw::DrawViewDimension] Dimension046
  Arbitrary = false
  ArbitraryTolerances = false
  EqualTolerance = true
  FormatSpec = %.2f
  FormatSpecOverTolerance = %+.2f
  FormatSpecUnderTolerance = %+.2f
  Inverted = false
  LockPosition = false
  MeasureType = 1
  OverTolerance = 0
  References2D = -> [ProjItem007]
  Rotation = 0
  ScaleType = 0
  TheoreticalExact = false
  Type = 0
  UnderTolerance = 0
  X = -7.41704
  Y = -9.29545
FEATURE [TechDraw::DrawViewDimension] Dimension047
  Arbitrary = false
  ArbitraryTolerances = false
  EqualTolerance = true
  FormatSpec = %.2f
  FormatSpecOverTolerance = %+.2f
  FormatSpecUnderTolerance = %+.2f
  Inverted = false
  LockPosition = false
  MeasureType = 1
  OverTolerance = 0
  References2D = -> [ProjItem007]
  Rotation = 0
  ScaleType = 0
  TheoreticalExact = false
  Type = 0
  UnderTolerance = 0
  X = -15.5069
  Y = 2.49368
FEATURE [TechDraw::DrawViewDimension] Dimension048
  Arbitrary = false
  ArbitraryTolerances = false
  EqualTolerance = true
  FormatSpec = %.2f
  FormatSpecOverTolerance = %+.2f
  FormatSpecUnderTolerance = %+.2f
  Inverted = false
  LockPosition = false
  MeasureType = 1
  OverTolerance = 0
  References2D = -> [ProjItem007]
  Rotation = 0
  ScaleType = 0
  TheoreticalExact = false
  Type = 0
  UnderTolerance = 0
  X = -9.00773
  Y = 9.13046
FEATURE [TechDraw::DrawViewDimension] Dimension049
  Arbitrary = false
  ArbitraryTolerances = false
  EqualTolerance = true
  FormatSpec = %.2f
  FormatSpecOverTolerance = %+.2f
  FormatSpecUnderTolerance = %+.2f
  Inverted = false
  LockPosition = false
  MeasureType = 1
  OverTolerance = 0
  References2D = -> [ProjItem007]
  Rotation = 0
  ScaleType = 0
  TheoreticalExact = false
  Type = 1
  UnderTolerance = 0
  X = 12.1701
  Y = 25.5418
FEATURE [TechDraw::DrawViewDimension] Dimension050
  Arbitrary = false
  ArbitraryTolerances = false
  EqualTolerance = true
  FormatSpec = %.2f
  FormatSpecOverTolerance = %+.2f
  FormatSpecUnderTolerance = %+.2f
  Inverted = false
  LockPosition = false
  MeasureType = 1
  OverTolerance = 0
  References2D = -> [ProjItem007]
  Rotation = 0
  ScaleType = 0
  TheoreticalExact = false
  Type = 1
  UnderTolerance = 0
  X = 2.4975
  Y = 31.558
FEATURE [TechDraw::DrawViewDimension] Dimension051
  Arbitrary = false
  ArbitraryTolerances = false
  EqualTolerance = true
  FormatSpec = %.2f
  FormatSpecOverTolerance = %+.2f
  FormatSpecUnderTolerance = %+.2f
  Inverted = false
  LockPosition = false
  MeasureType = 1
  OverTolerance = 0
  References2D = -> [ProjItem008]
  Rotation = 0
  ScaleType = 0
  TheoreticalExact = false
  Type = 0
  UnderTolerance = 0
  X = 25.1709
  Y = -14.7338
FEATURE [TechDraw::DrawViewDimension] Dimension052
  Arbitrary = false
  ArbitraryTolerances = false
  EqualTolerance = true
  FormatSpec = %.2f
  FormatSpecOverTolerance = %+.2f
  FormatSpecUnderTolerance = %+.2f
  Inverted = false
  LockPosition = false
  MeasureType = 1
  OverTolerance = 0
  References2D = -> [ProjItem008]
  Rotation = 0
  ScaleType = 0
  TheoreticalExact = false
  Type = 0
  UnderTolerance = 0
  X = 15.7672
  Y = 1.87763
FEATURE [TechDraw::DrawViewDimension] Dimension053
  Arbitrary = false
  ArbitraryTolerances = false
  EqualTolerance = true
  FormatSpec = %.2f
  FormatSpecOverTolerance = %+.2f
  FormatSpecUnderTolerance = %+.2f
  Inverted = false
  LockPosition = false
  MeasureType = 1
  OverTolerance = 0
  References2D = -> [ProjItem008]
  Rotation = 0
  ScaleType = 0
  TheoreticalExact = false
  Type = 0
  UnderTolerance = 0
  X = -8.94646
  Y = -5.82119
FEATURE [TechDraw::DrawViewDimension] Dimension054
  Arbitrary = false
  ArbitraryTolerances = false
  EqualTolerance = true
  FormatSpec = %.2f
  FormatSpecOverTolerance = %+.2f
  FormatSpecUnderTolerance = %+.2f
  Inverted = false
  LockPosition = false
  MeasureType = 1
  OverTolerance = 0
  References2D = -> [ProjItem008]
  Rotation = 0
  ScaleType = 0
  TheoreticalExact = false
  Type = 0
  UnderTolerance = 0
  X = 2.88285
  Y = -22.0563
FEATURE [TechDraw::DrawViewDimension] Dimension055
  Arbitrary = false
  ArbitraryTolerances = false
  EqualTolerance = true
  FormatSpec = %.2f
  FormatSpecOverTolerance = %+.2f
  FormatSpecUnderTolerance = %+.2f
  Inverted = false
  LockPosition = false
  MeasureType = 1
  OverTolerance = 0
  References2D = -> [ProjItem008]
  Rotation = 0
  ScaleType = 0
  TheoreticalExact = false
  Type = 0
  UnderTolerance = 0
  X = 4.45176
  Y = 24.9595
FEATURE [TechDraw::DrawViewDimension] Dimension056
  Arbitrary = false
  ArbitraryTolerances = false
  EqualTolerance = true
  FormatSpec = %.2f
  FormatSpecOverTolerance = %+.2f
  FormatSpecUnderTolerance = %+.2f
  Inverted = false
  LockPosition = false
  MeasureType = 1
  OverTolerance = 0
  References2D = -> [ProjItem008]
  Rotation = 0
  ScaleType = 0
  TheoreticalExact = false
  Type = 0
  UnderTolerance = 0
  X = -12.0974
  Y = 10.592
FEATURE [TechDraw::DrawViewDimension] Dimension057
  Arbitrary = false
  ArbitraryTolerances = false
  EqualTolerance = true
  FormatSpec = %.2f
  FormatSpecOverTolerance = %+.2f
  FormatSpecUnderTolerance = %+.2f
  Inverted = false
  LockPosition = false
  MeasureType = 1
  OverTolerance = 0
  References2D = -> [ProjItem008]
  Rotation = 0
  ScaleType = 0
  TheoreticalExact = false
  Type = 0
  UnderTolerance = 0
  X = 23.2988
  Y = 14.0393
FEATURE [TechDraw::DrawProjGroupItem] ProjItem009  label="Front009"
  CoarseView = false
  Direction = (0,-1,0)
  Focus = 100
  HardHidden = false
  IsoCount = 0
  IsoHidden = false
  IsoVisible = false
  LockPosition = true
  Perspective = false
  Rotation = 0
  RotationVector = (0.988,0,0.001)
  ScaleType = 2
  SeamHidden = false
  SeamVisible = true
  SmoothHidden = false
  SmoothVisible = true
  Source = -> [Cut162]
  Type = 0
  X = 0
  XDirection = (0.988,0,0.001)
  Y = 0
FEATURE [TechDraw::DrawProjGroup] ProjGroup009
  Anchor = -> ProjItem009
  AutoDistribute = true
  LockPosition = false
  ProjectionType = 0
  Rotation = 0
  ScaleType = 0
  Source = -> [Cut162]
  Views = -> [ProjItem009]
  X = 132.838
  Y = 161.639
  spacingX = 15
  spacingY = 15
FEATURE [TechDraw::DrawProjGroupItem] ProjItem010  label="Front010"
  CoarseView = false
  Direction = (0.99903,0.0432972,0.00804583)
  Focus = 100
  HardHidden = false
  IsoCount = 0
  IsoHidden = false
  IsoVisible = false
  LockPosition = true
  Perspective = false
  Rotation = 0
  RotationVector = (0.999,0.043,0.008)
  ScaleType = 2
  SeamHidden = false
  SeamVisible = true
  SmoothHidden = false
  SmoothVisible = true
  Source = -> [Cut162]
  Type = 0
  X = 0
  XDirection = (0.0013606,0.152267,-0.988338)
  Y = 0
FEATURE [TechDraw::DrawProjGroup] ProjGroup010
  Anchor = -> ProjItem010
  AutoDistribute = true
  LockPosition = false
  ProjectionType = 0
  Rotation = 0
  ScaleType = 0
  Source = -> [Cut162]
  Views = -> [ProjItem010]
  X = 106.166
  Y = 108.32
  spacingX = 15
  spacingY = 15
FEATURE [TechDraw::DrawViewDimension] Dimension058
  Arbitrary = false
  ArbitraryTolerances = false
  EqualTolerance = true
  FormatSpec = %.2f
  FormatSpecOverTolerance = %+.2f
  FormatSpecUnderTolerance = %+.2f
  Inverted = false
  LockPosition = false
  MeasureType = 1
  OverTolerance = 0
  References2D = -> [ProjItem009]
  Rotation = 0
  ScaleType = 0
  TheoreticalExact = false
  Type = 0
  UnderTolerance = 0
  X = 22.5436
  Y = 2.88617
FEATURE [TechDraw::DrawViewDimension] Dimension059
  Arbitrary = false
  ArbitraryTolerances = false
  EqualTolerance = true
  FormatSpec = %.2f
  FormatSpecOverTolerance = %+.2f
  FormatSpecUnderTolerance = %+.2f
  Inverted = false
  LockPosition = false
  MeasureType = 1
  OverTolerance = 0
  References2D = -> [ProjItem009]
  Rotation = 0
  ScaleType = 0
  TheoreticalExact = false
  Type = 0
  UnderTolerance = 0
  X = 29.3166
  Y = 20.2227
FEATURE [TechDraw::DrawViewDimension] Dimension060
  Arbitrary = false
  ArbitraryTolerances = false
  EqualTolerance = true
  FormatSpec = %.2f
  FormatSpecOverTolerance = %+.2f
  FormatSpecUnderTolerance = %+.2f
  Inverted = false
  LockPosition = false
  MeasureType = 1
  OverTolerance = 0
  References2D = -> [ProjItem009]
  Rotation = 0
  ScaleType = 0
  TheoreticalExact = false
  Type = 1
  UnderTolerance = 0
  X = -0.0033308
  Y = -27.498
FEATURE [TechDraw::DrawViewDimension] Dimension061
  Arbitrary = false
  ArbitraryTolerances = false
  EqualTolerance = true
  FormatSpec = %.2f
  FormatSpecOverTolerance = %+.2f
  FormatSpecUnderTolerance = %+.2f
  Inverted = false
  LockPosition = false
  MeasureType = 1
  OverTolerance = 0
  References2D = -> [ProjItem009]
  Rotation = 0
  ScaleType = 0
  TheoreticalExact = false
  Type = 0
  UnderTolerance = 0
  X = 37.7573
  Y = -22.2934
FEATURE [TechDraw::DrawViewDimension] Dimension062
  Arbitrary = false
  ArbitraryTolerances = false
  EqualTolerance = true
  FormatSpec = %.2f
  FormatSpecOverTolerance = %+.2f
  FormatSpecUnderTolerance = %+.2f
  Inverted = false
  LockPosition = false
  MeasureType = 1
  OverTolerance = 0
  References2D = -> [ProjItem009]
  Rotation = 0
  ScaleType = 0
  TheoreticalExact = false
  Type = 2
  UnderTolerance = 0
  X = -30.8957
  Y = -16.8405
FEATURE [TechDraw::DrawViewDimension] Dimension063
  Arbitrary = false
  ArbitraryTolerances = false
  EqualTolerance = true
  FormatSpec = %.2f
  FormatSpecOverTolerance = %+.2f
  FormatSpecUnderTolerance = %+.2f
  Inverted = false
  LockPosition = false
  MeasureType = 1
  OverTolerance = 0
  References2D = -> [ProjItem009]
  Rotation = 0
  ScaleType = 0
  TheoreticalExact = false
  Type = 2
  UnderTolerance = 0
  X = -5.23001
  Y = 0.621925
FEATURE [TechDraw::DrawViewDimension] Dimension064
  Arbitrary = false
  ArbitraryTolerances = false
  EqualTolerance = true
  FormatSpec = %.2f
  FormatSpecOverTolerance = %+.2f
  FormatSpecUnderTolerance = %+.2f
  Inverted = false
  LockPosition = false
  MeasureType = 1
  OverTolerance = 0
  References2D = -> [ProjItem009]
  Rotation = 0
  ScaleType = 0
  TheoreticalExact = false
  Type = 1
  UnderTolerance = 0
  X = -15.1797
  Y = -3.75341
FEATURE [TechDraw::DrawViewDimension] Dimension065
  Arbitrary = false
  ArbitraryTolerances = false
  EqualTolerance = true
  FormatSpec = %.2f
  FormatSpecOverTolerance = %+.2f
  FormatSpecUnderTolerance = %+.2f
  Inverted = false
  LockPosition = false
  MeasureType = 1
  OverTolerance = 0
  References2D = -> [ProjItem009]
  Rotation = 0
  ScaleType = 0
  TheoreticalExact = false
  Type = 0
  UnderTolerance = 0
  X = -29.6296
  Y = 17.2804
FEATURE [TechDraw::DrawViewDimension] Dimension066
  Arbitrary = false
  ArbitraryTolerances = false
  EqualTolerance = true
  FormatSpec = %.2f
  FormatSpecOverTolerance = %+.2f
  FormatSpecUnderTolerance = %+.2f
  Inverted = false
  LockPosition = false
  MeasureType = 1
  OverTolerance = 0
  References2D = -> [ProjItem009]
  Rotation = 0
  ScaleType = 0
  TheoreticalExact = false
  Type = 1
  UnderTolerance = 0
  X = -6.27691
  Y = 21.9811
FEATURE [TechDraw::DrawViewDimension] Dimension067
  Arbitrary = false
  ArbitraryTolerances = false
  EqualTolerance = true
  FormatSpec = %.2f
  FormatSpecOverTolerance = %+.2f
  FormatSpecUnderTolerance = %+.2f
  Inverted = false
  LockPosition = false
  MeasureType = 1
  OverTolerance = 0
  References2D = -> [ProjItem009]
  Rotation = 0
  ScaleType = 0
  TheoreticalExact = false
  Type = 0
  UnderTolerance = 0
  X = 5.70285
  Y = 36.1717
FEATURE [TechDraw::DrawViewDimension] Dimension068
  Arbitrary = false
  ArbitraryTolerances = false
  EqualTolerance = true
  FormatSpec = %.2f
  FormatSpecOverTolerance = %+.2f
  FormatSpecUnderTolerance = %+.2f
  Inverted = false
  LockPosition = false
  MeasureType = 1
  OverTolerance = 0
  References2D = -> [ProjItem009]
  Rotation = 0
  ScaleType = 0
  TheoreticalExact = false
  Type = 1
  UnderTolerance = 0
  X = -15.9897
  Y = 36.1935
FEATURE [TechDraw::DrawViewDimension] Dimension069
  Arbitrary = false
  ArbitraryTolerances = false
  EqualTolerance = true
  FormatSpec = %.2f
  FormatSpecOverTolerance = %+.2f
  FormatSpecUnderTolerance = %+.2f
  Inverted = false
  LockPosition = false
  MeasureType = 1
  OverTolerance = 0
  References2D = -> [ProjItem010]
  Rotation = 0
  ScaleType = 0
  TheoreticalExact = false
  Type = 0
  UnderTolerance = 0
  X = 1.7321
  Y = -13.8912
FEATURE [TechDraw::DrawViewDimension] Dimension070
  Arbitrary = false
  ArbitraryTolerances = false
  EqualTolerance = true
  FormatSpec = %.2f
  FormatSpecOverTolerance = %+.2f
  FormatSpecUnderTolerance = %+.2f
  Inverted = false
  LockPosition = false
  MeasureType = 1
  OverTolerance = 0
  References2D = -> [ProjItem010]
  Rotation = 0
  ScaleType = 0
  TheoreticalExact = false
  Type = 0
  UnderTolerance = 0
  X = 39.2542
  Y = -5.28121
FEATURE [TechDraw::DrawViewDimension] Dimension071
  Arbitrary = false
  ArbitraryTolerances = false
  EqualTolerance = true
  FormatSpec = %.2f
  FormatSpecOverTolerance = %+.2f
  FormatSpecUnderTolerance = %+.2f
  Inverted = false
  LockPosition = false
  MeasureType = 1
  OverTolerance = 0
  References2D = -> [ProjItem010]
  Rotation = 0
  ScaleType = 0
  TheoreticalExact = false
  Type = 0
  UnderTolerance = 0
  X = 31.1959
  Y = -15.4956
FEATURE [TechDraw::DrawViewDimension] Dimension072
  Arbitrary = false
  ArbitraryTolerances = false
  EqualTolerance = true
  FormatSpec = %.2f
  FormatSpecOverTolerance = %+.2f
  FormatSpecUnderTolerance = %+.2f
  Inverted = false
  LockPosition = false
  MeasureType = 1
  OverTolerance = 0
  References2D = -> [ProjItem010]
  Rotation = 0
  ScaleType = 0
  TheoreticalExact = false
  Type = 0
  UnderTolerance = 0
  X = 20.5355
  Y = 12.3082
FEATURE [TechDraw::DrawViewDimension] Dimension073
  Arbitrary = false
  ArbitraryTolerances = false
  EqualTolerance = true
  FormatSpec = %.2f
  FormatSpecOverTolerance = %+.2f
  FormatSpecUnderTolerance = %+.2f
  Inverted = false
  LockPosition = false
  MeasureType = 1
  OverTolerance = 0
  References2D = -> [ProjItem010]
  Rotation = 0
  ScaleType = 0
  TheoreticalExact = false
  Type = 0
  UnderTolerance = 0
  X = -12.956
  Y = 17.8046
FEATURE [TechDraw::DrawViewDimension] Dimension074
  Arbitrary = false
  ArbitraryTolerances = false
  EqualTolerance = true
  FormatSpec = %.2f
  FormatSpecOverTolerance = %+.2f
  FormatSpecUnderTolerance = %+.2f
  Inverted = false
  LockPosition = false
  MeasureType = 1
  OverTolerance = 0
  References2D = -> [ProjItem010]
  Rotation = 0
  ScaleType = 0
  TheoreticalExact = false
  Type = 0
  UnderTolerance = 0
  X = 4.99658
  Y = 14.9431
FEATURE [TechDraw::DrawViewDimension] Dimension075
  Arbitrary = false
  ArbitraryTolerances = false
  EqualTolerance = true
  FormatSpec = %.2f
  FormatSpecOverTolerance = %+.2f
  FormatSpecUnderTolerance = %+.2f
  Inverted = false
  LockPosition = false
  MeasureType = 1
  OverTolerance = 0
  References2D = -> [ProjItem010]
  Rotation = 0
  ScaleType = 0
  TheoreticalExact = false
  Type = 0
  UnderTolerance = 0
  X = 13.608
  Y = -7.70904
FEATURE [TechDraw::DrawViewDimension] Dimension076
  Arbitrary = false
  ArbitraryTolerances = false
  EqualTolerance = true
  FormatSpec = %.2f
  FormatSpecOverTolerance = %+.2f
  FormatSpecUnderTolerance = %+.2f
  Inverted = false
  LockPosition = false
  MeasureType = 1
  OverTolerance = 0
  References2D = -> [ProjItem010]
  Rotation = 0
  ScaleType = 0
  TheoreticalExact = false
  Type = 0
  UnderTolerance = 0
  X = -21.845
  Y = -14.0168
FEATURE [TechDraw::DrawViewDimension] Dimension077
  Arbitrary = false
  ArbitraryTolerances = false
  EqualTolerance = true
  FormatSpec = %.2f
  FormatSpecOverTolerance = %+.2f
  FormatSpecUnderTolerance = %+.2f
  Inverted = false
  LockPosition = false
  MeasureType = 1
  OverTolerance = 0
  References2D = -> [ProjItem010]
  Rotation = 0
  ScaleType = 0
  TheoreticalExact = false
  Type = 0
  UnderTolerance = 0
  X = -19.4982
  Y = -1.89061
FEATURE [TechDraw::DrawPage] Page
  KeepUpdated = false
  NextBalloonIndex = 1
  ProjectionType = 0
  Template = -> Template
  Views = -> [ProjGroup,Dimension,Dimension001,Dimension002,Dimension003,Dimension004,ProjGroup001,Dimension005,Dimension006,Dimension007,Dimension008,Dimension009,Dimension010,Dimension011,Dimension012,Dimension013,Dimension014,Dimension015,ProjGroup002,ProjGroup003,Dimension016,Dimension017,Dimension018,Dimension019,Dimension020,ProjGroup004,Dimension021,Dimension022,Dimension023,Dimension024,Dimension025,+58 more]
